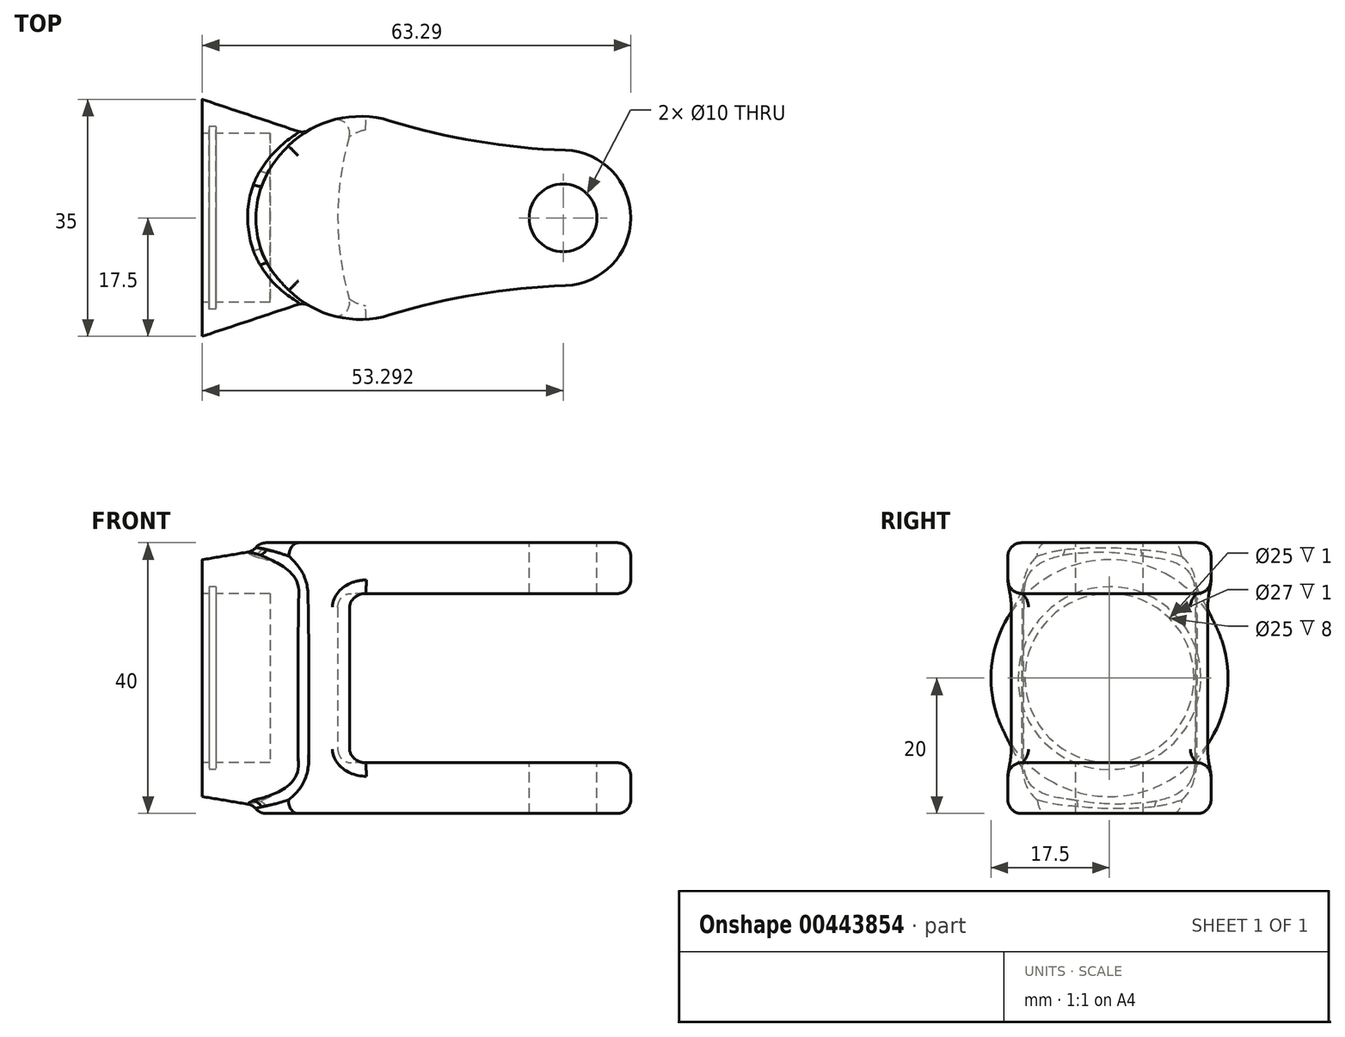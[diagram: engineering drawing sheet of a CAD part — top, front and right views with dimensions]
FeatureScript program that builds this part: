
annotation { "Feature Type Name" : "Feature", "Feature Type Description" : "" }
export const myFeature = defineFeature(function(context is Context, id is Id, definition is map)
    precondition{}
    {
        {
            var Q0;
            Q0=qCreatedBy(makeId("Right.planeOp"),FACE);
            var sketch = newSketch(context, id + "F0", { "sketchPlane" : qUnion([Q0])});
            skCircle(sketch, "E0", {"center": v(0, 0) * mm, "radius": 17.5 * mm});
            skSolve(sketch);
        }
        {
            var Q0;
            Q0=qCreatedBy(makeId("Right.planeOp"),FACE);
            cPlane(context, id + "F1", {"entities" : qUnion([Q0]), "cplaneType" : CPlaneType.OFFSET, "offset" : 15 * mm, "width" : 150 * mm, "height" : 150 * mm});
        }
        {
            var Q0;
            Q0=qCreatedBy(id+"F1.planeOp",FACE);
            var sketch = newSketch(context, id + "F2", { "sketchPlane" : qUnion([Q0])});
            skLineSegment(sketch, "E1.bottom", {"start": v(5, -20) * mm, "end": v(-5, -20) * mm});
            skLineSegment(sketch, "E1.top", {"start": v(5, 20) * mm, "end": v(-5, 20) * mm});
            skLineSegment(sketch, "E1.left", {"start": v(12.5, -12.5) * mm, "end": v(12.5, 12.5) * mm});
            skLineSegment(sketch, "E1.right", {"start": v(-12.5, -12.5) * mm, "end": v(-12.5, 12.5) * mm});
            skPoint(sketch, "E1.middle", {"position": v(0, 0) * mm});
            skPoint(sketch, "E2.visualSharp", {"position": v(-12.5, 20) * mm});
            skArc(sketch, "E2.filletArc", {"start": v(-5, 20) * mm, "mid": v(-10.3, 17.8) * mm, "end": v(-12.5, 12.5) * mm});
            skPoint(sketch, "E3.visualSharp", {"position": v(12.5, 20) * mm});
            skArc(sketch, "E3.filletArc", {"start": v(12.5, 12.5) * mm, "mid": v(10.3, 17.8) * mm, "end": v(5, 20) * mm});
            skPoint(sketch, "E4.visualSharp", {"position": v(12.5, -20) * mm});
            skArc(sketch, "E4.filletArc", {"start": v(5, -20) * mm, "mid": v(10.3, -17.8) * mm, "end": v(12.5, -12.5) * mm});
            skPoint(sketch, "E5.visualSharp", {"position": v(-12.5, -20) * mm});
            skArc(sketch, "E5.filletArc", {"start": v(-12.5, -12.5) * mm, "mid": v(-10.3, -17.8) * mm, "end": v(-5, -20) * mm});
            skSolve(sketch);
        }
        {
            var Q0;
            Q0 = qSketchRegion(id + "F2", true);
            var Q1;
            Q1=makeQuery(id+"F0.imprint","IMPRINT",FACE,{"disambiguationData":[TD([[makeQuery(id+"F0.imprint","IMPRINT",EDGE,{"derivedFrom":sQuery(id+"F0.wireOp",EDGE,"E0")}),1.0]])]});
            loft(context, id + "F3", {"sheetProfilesArray" : [{ "sheetProfileEntities" : qUnion([Q0]) }, { "sheetProfileEntities" : qUnion([Q1]) }]});
        }
        {
            var Q0;
            Q0=qCreatedBy(makeId("Top.planeOp"),FACE);
            var sketch = newSketch(context, id + "F4", { "sketchPlane" : qUnion([Q0])});
            skCircle(sketch, "E6", {"center": v(23.3, 0) * mm, "radius": 15 * mm});
            skCircle(sketch, "E7", {"center": v(53.3, 0) * mm, "radius": 10 * mm});
            skArc(sketch, "E8", {"start": v(27.7, 14.34) * mm, "mid": v(40.52, 11.31) * mm, "end": v(53.63, 10) * mm});
            skArc(sketch, "E9", {"start": v(53.63, -10) * mm, "mid": v(40.52, -11.31) * mm, "end": v(27.7, -14.34) * mm});
            skSolve(sketch);
        }
        {
            var Q0;
            Q0 = qSketchRegion(id + "F4", true);
            extrude(context, id + "F5", {"entities" : qUnion([Q0]), "operationType" : NewBodyOperationType.ADD, "endBound" : BoundingType.SYMMETRIC, "depth" : 40 * mm});
        }
        {
            var Q0;
            Q0=qCreatedBy(makeId("Front.planeOp"),FACE);
            var sketch = newSketch(context, id + "F6", { "sketchPlane" : qUnion([Q0])});
            skLineSegment(sketch, "E10", {"start": v(63.3, -12.5) * mm, "end": v(20, -12.5) * mm});
            skLineSegment(sketch, "E11", {"start": v(20, -12.5) * mm, "end": v(20, 12.5) * mm});
            skLineSegment(sketch, "E12", {"start": v(20, 12.5) * mm, "end": v(63.3, 12.5) * mm});
            skLineSegment(sketch, "E13", {"start": v(63.3, 12.5) * mm, "end": v(63.3, -12.5) * mm});
            skSolve(sketch);
        }
        {
            var Q0;
            Q0 = qSketchRegion(id + "F6", true);
            var Q1;
            Q1=sQuery(id+"F6.wireOp",EDGE,"E13");
            revolve(context, id + "F7", {"operationType" : NewBodyOperationType.REMOVE, "entities" : qUnion([Q0]), "axis" : qUnion([Q1]), "revolveType" : RevolveType.FULL, "oppositeDirection" : true});
        }
        {
            var Q0;
            Q0=makeQuery(id+"F3.opLoft","CAP_FACE",FACE,{"disambiguationData":[OSD([makeQuery(id+"F0.imprint","IMPRINT",FACE,{"disambiguationData":[TD([[makeQuery(id+"F0.imprint","IMPRINT",EDGE,{"derivedFrom":sQuery(id+"F0.wireOp",EDGE,"E0")}),1.0]])]})])],"isStart":true});
            var sketch = newSketch(context, id + "F8", { "sketchPlane" : qUnion([Q0])});
            skCircle(sketch, "E14", {"center": v(0, 0) * mm, "radius": 12.5 * mm});
            skSolve(sketch);
        }
        {
            var Q0;
            Q0 = qSketchRegion(id + "F8", true);
            extrude(context, id + "F9", {"entities" : qUnion([Q0]), "operationType" : NewBodyOperationType.REMOVE, "oppositeDirection" : true, "depth" : 10 * mm});
        }
        {
            var Q0;
            Q0=makeQuery(id+"F3.opLoft","CAP_FACE",FACE,{"disambiguationData":[OSD([makeQuery(id+"F0.imprint","IMPRINT",FACE,{"disambiguationData":[TD([[makeQuery(id+"F0.imprint","IMPRINT",EDGE,{"derivedFrom":sQuery(id+"F0.wireOp",EDGE,"E0")}),1.0]])]})])],"isStart":true});
            cPlane(context, id + "F10", {"entities" : qUnion([Q0]), "cplaneType" : CPlaneType.OFFSET, "offset" : 1 * mm, "oppositeDirection" : true, "width" : 150 * mm, "height" : 150 * mm});
        }
        {
            var Q0;
            Q0=qCreatedBy(id+"F10.planeOp",FACE);
            var sketch = newSketch(context, id + "F11", { "sketchPlane" : qUnion([Q0])});
            skCircle(sketch, "E15.0", {"center": v(0, 0) * mm, "radius": 12.5 * mm});
            skCircle(sketch, "E16.0", {"center": v(0, 0) * mm, "radius": 13.5 * mm});
            skSolve(sketch);
        }
        {
            var Q0;
            Q0 = qSketchRegion(id + "F11", true);
            extrude(context, id + "F12", {"entities" : qUnion([Q0]), "operationType" : NewBodyOperationType.REMOVE, "oppositeDirection" : true, "depth" : 1 * mm});
        }
        {
            var Q0;
            Q0=makeQuery(id+"F5.opExtrude","CAP_FACE",FACE,{"disambiguationData":[OSD([sQuery(id+"F4.wireOp",EDGE,"E6"),sQuery(id+"F4.wireOp",EDGE,"E7"),sQuery(id+"F4.wireOp",EDGE,"E8"),sQuery(id+"F4.wireOp",EDGE,"E9")])],"isStart":false});
            var sketch = newSketch(context, id + "F13", { "sketchPlane" : qUnion([Q0])});
            skCircle(sketch, "E17", {"center": v(53.3, 0) * mm, "radius": 5 * mm});
            skSolve(sketch);
        }
        {
            var Q0;
            Q0=makeQuery(id+"F13.imprint","IMPRINT",FACE,{"disambiguationData":[TD([[makeQuery(id+"F13.imprint","IMPRINT",EDGE,{"derivedFrom":sQuery(id+"F13.wireOp",EDGE,"E17")}),1.0]])]});
            var Q1;
            Q1=sQuery(id+"F13.wireOp",EDGE,"E17");
            extrude(context, id + "F14", {"entities" : qUnion([Q0]), "operationType" : NewBodyOperationType.REMOVE, "surfaceEntities" : qUnion([Q1]), "endBound" : BoundingType.THROUGH_ALL, "oppositeDirection" : true, "depth" : 25 * mm});
        }
        {
            var Q0;
            Q0=makeQuery(id+"F7.boolean.opBoolean","COPY",EDGE,{"derivedFrom":makeQuery(id+"F7.opRevolve","SWEPT_EDGE",EDGE,{"disambiguationData":[OSD([sQuery(id+"F6.wireOp",EDGE,"E11"),sQuery(id+"F6.wireOp",EDGE,"E12")])]})});
            var Q1;
            Q1=makeQuery(id+"F7.boolean.opBoolean","COPY",EDGE,{"derivedFrom":makeQuery(id+"F7.opRevolve","SWEPT_EDGE",EDGE,{"disambiguationData":[OSD([sQuery(id+"F6.wireOp",EDGE,"E10"),sQuery(id+"F6.wireOp",EDGE,"E11")])]})});
            fillet(context, id + "F15", {"entities" : qUnion([Q0, Q1]), "radius" : 2 * mm, "tangentPropagation" : true, "allowEdgeOverflow" : false});
        }
        {
            var Q0;
            Q0=makeQuery(id+"F5.boolean.opBoolean","INTERSECT",EDGE,{"disambiguationData":[OD(0.0)],"derivedFrom":[makeQuery(id+"F3.opLoft","SWEPT_FACE",FACE,{"disambiguationData":[OSD([sQuery(id+"F0.wireOp",EDGE,"E0"),sQuery(id+"F2.wireOp",EDGE,"E1.bottom"),sQuery(id+"F2.wireOp",EDGE,"E4.filletArc"),sQuery(id+"F2.wireOp",EDGE,"E5.filletArc")])]}),makeQuery(id+"F5.opExtrude","SWEPT_FACE",FACE,{"disambiguationData":[OSD([sQuery(id+"F4.wireOp",EDGE,"E6")])]})]});
            var Q1;
            Q1=makeQuery(id+"F5.boolean.opBoolean","INTERSECT",EDGE,{"disambiguationData":[OD(1.0)],"derivedFrom":[makeQuery(id+"F3.opLoft","SWEPT_FACE",FACE,{"disambiguationData":[OSD([sQuery(id+"F0.wireOp",EDGE,"E0"),sQuery(id+"F2.wireOp",EDGE,"E1.bottom"),sQuery(id+"F2.wireOp",EDGE,"E4.filletArc"),sQuery(id+"F2.wireOp",EDGE,"E5.filletArc")])]}),makeQuery(id+"F5.opExtrude","SWEPT_FACE",FACE,{"disambiguationData":[OSD([sQuery(id+"F4.wireOp",EDGE,"E6")])]})]});
            fillet(context, id + "F16", {"entities" : qUnion([Q0, Q1]), "radius" : 2 * mm, "tangentPropagation" : true, "allowEdgeOverflow" : false});
        }
        {
            var Q0;
            Q0=makeQuery(id+"F5.opExtrude","CAP_EDGE",EDGE,{"disambiguationData":[OSD([sQuery(id+"F4.wireOp",EDGE,"E6")])],"isStart":true});
            var Q1;
            Q1=makeQuery(id+"F5.opExtrude","CAP_EDGE",EDGE,{"disambiguationData":[OSD([sQuery(id+"F4.wireOp",EDGE,"E6")])],"isStart":true});
            var Q2;
            Q2=makeQuery(id+"F5.opExtrude","CAP_EDGE",EDGE,{"disambiguationData":[OSD([sQuery(id+"F4.wireOp",EDGE,"E6")])],"isStart":true});
            var Q3;
            Q3=makeQuery(id+"F5.opExtrude","CAP_EDGE",EDGE,{"disambiguationData":[OSD([sQuery(id+"F4.wireOp",EDGE,"E6")])],"isStart":true});
            var Q4;
            Q4=makeQuery(id+"F5.opExtrude","CAP_EDGE",EDGE,{"disambiguationData":[OSD([sQuery(id+"F4.wireOp",EDGE,"E6")])],"isStart":true});
            var Q5;
            Q5=makeQuery(id+"F5.opExtrude","CAP_EDGE",EDGE,{"disambiguationData":[OSD([sQuery(id+"F4.wireOp",EDGE,"E6")])],"isStart":true});
            var Q6;
            Q6=makeQuery(id+"F5.opExtrude","CAP_EDGE",EDGE,{"disambiguationData":[OSD([sQuery(id+"F4.wireOp",EDGE,"E6")])],"isStart":true});
            var Q7;
            Q7=makeQuery(id+"F5.opExtrude","CAP_EDGE",EDGE,{"disambiguationData":[OSD([sQuery(id+"F4.wireOp",EDGE,"E6")])],"isStart":true});
            var Q8;
            Q8=makeQuery(id+"F5.opExtrude","CAP_EDGE",EDGE,{"disambiguationData":[OSD([sQuery(id+"F4.wireOp",EDGE,"E6")])],"isStart":true});
            var Q9;
            Q9=makeQuery(id+"F5.opExtrude","CAP_EDGE",EDGE,{"disambiguationData":[OSD([sQuery(id+"F4.wireOp",EDGE,"E6")])],"isStart":true});
            var Q10;
            Q10=makeQuery(id+"F5.opExtrude","CAP_EDGE",EDGE,{"disambiguationData":[OSD([sQuery(id+"F4.wireOp",EDGE,"E6")])],"isStart":true});
            var Q11;
            Q11=makeQuery(id+"F5.opExtrude","CAP_EDGE",EDGE,{"disambiguationData":[OSD([sQuery(id+"F4.wireOp",EDGE,"E6")])],"isStart":true});
            var Q12;
            Q12=makeQuery(id+"F5.opExtrude","CAP_EDGE",EDGE,{"disambiguationData":[OSD([sQuery(id+"F4.wireOp",EDGE,"E6")])],"isStart":true});
            var Q13;
            Q13=makeQuery(id+"F5.opExtrude","CAP_EDGE",EDGE,{"disambiguationData":[OSD([sQuery(id+"F4.wireOp",EDGE,"E6")])],"isStart":true});
            var Q14;
            Q14=makeQuery(id+"F5.opExtrude","CAP_EDGE",EDGE,{"disambiguationData":[OSD([sQuery(id+"F4.wireOp",EDGE,"E6")])],"isStart":true});
            var Q15;
            Q15=makeQuery(id+"F5.opExtrude","CAP_EDGE",EDGE,{"disambiguationData":[OSD([sQuery(id+"F4.wireOp",EDGE,"E6")])],"isStart":true});
            var Q16;
            Q16=makeQuery(id+"F5.opExtrude","CAP_EDGE",EDGE,{"disambiguationData":[OSD([sQuery(id+"F4.wireOp",EDGE,"E6")])],"isStart":true});
            var Q17;
            Q17=makeQuery(id+"F5.opExtrude","CAP_EDGE",EDGE,{"disambiguationData":[OSD([sQuery(id+"F4.wireOp",EDGE,"E6")])],"isStart":true});
            var Q18;
            Q18=makeQuery(id+"F5.opExtrude","CAP_EDGE",EDGE,{"disambiguationData":[OSD([sQuery(id+"F4.wireOp",EDGE,"E6")])],"isStart":true});
            var Q19;
            Q19=makeQuery(id+"F5.opExtrude","CAP_EDGE",EDGE,{"disambiguationData":[OSD([sQuery(id+"F4.wireOp",EDGE,"E6")])],"isStart":true});
            var Q20;
            Q20=makeQuery(id+"F5.opExtrude","CAP_EDGE",EDGE,{"disambiguationData":[OSD([sQuery(id+"F4.wireOp",EDGE,"E6")])],"isStart":true});
            var Q21;
            Q21=makeQuery(id+"F5.opExtrude","CAP_EDGE",EDGE,{"disambiguationData":[OSD([sQuery(id+"F4.wireOp",EDGE,"E6")])],"isStart":true});
            var Q22;
            Q22=makeQuery(id+"F5.opExtrude","CAP_EDGE",EDGE,{"disambiguationData":[OSD([sQuery(id+"F4.wireOp",EDGE,"E6")])],"isStart":true});
            var Q23;
            Q23=makeQuery(id+"F5.opExtrude","CAP_EDGE",EDGE,{"disambiguationData":[OSD([sQuery(id+"F4.wireOp",EDGE,"E6")])],"isStart":true});
            var Q24;
            Q24=makeQuery(id+"F5.opExtrude","CAP_EDGE",EDGE,{"disambiguationData":[OSD([sQuery(id+"F4.wireOp",EDGE,"E6")])],"isStart":true});
            var Q25;
            Q25=makeQuery(id+"F5.opExtrude","CAP_EDGE",EDGE,{"disambiguationData":[OSD([sQuery(id+"F4.wireOp",EDGE,"E6")])],"isStart":true});
            var Q26;
            Q26=makeQuery(id+"F5.opExtrude","CAP_EDGE",EDGE,{"disambiguationData":[OSD([sQuery(id+"F4.wireOp",EDGE,"E6")])],"isStart":true});
            var Q27;
            Q27=makeQuery(id+"F5.opExtrude","CAP_EDGE",EDGE,{"disambiguationData":[OSD([sQuery(id+"F4.wireOp",EDGE,"E6")])],"isStart":true});
            var Q28;
            Q28=makeQuery(id+"F5.opExtrude","CAP_EDGE",EDGE,{"disambiguationData":[OSD([sQuery(id+"F4.wireOp",EDGE,"E6")])],"isStart":true});
            var Q29;
            Q29=makeQuery(id+"F5.opExtrude","CAP_EDGE",EDGE,{"disambiguationData":[OSD([sQuery(id+"F4.wireOp",EDGE,"E6")])],"isStart":true});
            var Q30;
            Q30=makeQuery(id+"F5.opExtrude","CAP_EDGE",EDGE,{"disambiguationData":[OSD([sQuery(id+"F4.wireOp",EDGE,"E6")])],"isStart":true});
            var Q31;
            Q31=makeQuery(id+"F5.opExtrude","CAP_EDGE",EDGE,{"disambiguationData":[OSD([sQuery(id+"F4.wireOp",EDGE,"E6")])],"isStart":true});
            var Q32;
            Q32=makeQuery(id+"F5.opExtrude","CAP_EDGE",EDGE,{"disambiguationData":[OSD([sQuery(id+"F4.wireOp",EDGE,"E6")])],"isStart":true});
            var Q33;
            Q33=makeQuery(id+"F5.opExtrude","CAP_EDGE",EDGE,{"disambiguationData":[OSD([sQuery(id+"F4.wireOp",EDGE,"E6")])],"isStart":true});
            var Q34;
            Q34=makeQuery(id+"F5.opExtrude","CAP_EDGE",EDGE,{"disambiguationData":[OSD([sQuery(id+"F4.wireOp",EDGE,"E6")])],"isStart":true});
            var Q35;
            Q35=makeQuery(id+"F5.opExtrude","CAP_EDGE",EDGE,{"disambiguationData":[OSD([sQuery(id+"F4.wireOp",EDGE,"E6")])],"isStart":true});
            var Q36;
            Q36=makeQuery(id+"F5.opExtrude","CAP_EDGE",EDGE,{"disambiguationData":[OSD([sQuery(id+"F4.wireOp",EDGE,"E6")])],"isStart":true});
            var Q37;
            Q37=makeQuery(id+"F5.opExtrude","CAP_EDGE",EDGE,{"disambiguationData":[OSD([sQuery(id+"F4.wireOp",EDGE,"E6")])],"isStart":true});
            var Q38;
            Q38=makeQuery(id+"F5.opExtrude","CAP_EDGE",EDGE,{"disambiguationData":[OSD([sQuery(id+"F4.wireOp",EDGE,"E6")])],"isStart":true});
            var Q39;
            Q39=makeQuery(id+"F5.opExtrude","CAP_EDGE",EDGE,{"disambiguationData":[OSD([sQuery(id+"F4.wireOp",EDGE,"E6")])],"isStart":true});
            var Q40;
            Q40=makeQuery(id+"F5.opExtrude","CAP_EDGE",EDGE,{"disambiguationData":[OSD([sQuery(id+"F4.wireOp",EDGE,"E6")])],"isStart":true});
            var Q41;
            Q41=makeQuery(id+"F5.opExtrude","CAP_EDGE",EDGE,{"disambiguationData":[OSD([sQuery(id+"F4.wireOp",EDGE,"E6")])],"isStart":true});
            var Q42;
            Q42=makeQuery(id+"F5.opExtrude","CAP_EDGE",EDGE,{"disambiguationData":[OSD([sQuery(id+"F4.wireOp",EDGE,"E6")])],"isStart":true});
            var Q43;
            Q43=makeQuery(id+"F5.opExtrude","CAP_EDGE",EDGE,{"disambiguationData":[OSD([sQuery(id+"F4.wireOp",EDGE,"E6")])],"isStart":true});
            var Q44;
            Q44=makeQuery(id+"F5.opExtrude","CAP_EDGE",EDGE,{"disambiguationData":[OSD([sQuery(id+"F4.wireOp",EDGE,"E6")])],"isStart":true});
            var Q45;
            Q45=makeQuery(id+"F5.opExtrude","CAP_EDGE",EDGE,{"disambiguationData":[OSD([sQuery(id+"F4.wireOp",EDGE,"E6")])],"isStart":true});
            var Q46;
            Q46=makeQuery(id+"F5.opExtrude","CAP_EDGE",EDGE,{"disambiguationData":[OSD([sQuery(id+"F4.wireOp",EDGE,"E6")])],"isStart":true});
            var Q47;
            Q47=makeQuery(id+"F5.opExtrude","CAP_EDGE",EDGE,{"disambiguationData":[OSD([sQuery(id+"F4.wireOp",EDGE,"E6")])],"isStart":true});
            var Q48;
            Q48=makeQuery(id+"F5.opExtrude","CAP_EDGE",EDGE,{"disambiguationData":[OSD([sQuery(id+"F4.wireOp",EDGE,"E6")])],"isStart":true});
            var Q49;
            Q49=makeQuery(id+"F5.opExtrude","CAP_EDGE",EDGE,{"disambiguationData":[OSD([sQuery(id+"F4.wireOp",EDGE,"E6")])],"isStart":true});
            var Q50;
            Q50=makeQuery(id+"F5.opExtrude","CAP_EDGE",EDGE,{"disambiguationData":[OSD([sQuery(id+"F4.wireOp",EDGE,"E6")])],"isStart":true});
            var Q51;
            Q51=makeQuery(id+"F5.opExtrude","CAP_EDGE",EDGE,{"disambiguationData":[OSD([sQuery(id+"F4.wireOp",EDGE,"E6")])],"isStart":true});
            var Q52;
            Q52=makeQuery(id+"F5.opExtrude","CAP_EDGE",EDGE,{"disambiguationData":[OSD([sQuery(id+"F4.wireOp",EDGE,"E6")])],"isStart":true});
            var Q53;
            Q53=makeQuery(id+"F5.opExtrude","CAP_EDGE",EDGE,{"disambiguationData":[OSD([sQuery(id+"F4.wireOp",EDGE,"E6")])],"isStart":true});
            var Q54;
            Q54=makeQuery(id+"F5.opExtrude","CAP_EDGE",EDGE,{"disambiguationData":[OSD([sQuery(id+"F4.wireOp",EDGE,"E6")])],"isStart":true});
            var Q55;
            Q55=makeQuery(id+"F5.opExtrude","CAP_EDGE",EDGE,{"disambiguationData":[OSD([sQuery(id+"F4.wireOp",EDGE,"E6")])],"isStart":true});
            var Q56;
            Q56=makeQuery(id+"F5.opExtrude","CAP_EDGE",EDGE,{"disambiguationData":[OSD([sQuery(id+"F4.wireOp",EDGE,"E6")])],"isStart":true});
            var Q57;
            Q57=makeQuery(id+"F5.opExtrude","CAP_EDGE",EDGE,{"disambiguationData":[OSD([sQuery(id+"F4.wireOp",EDGE,"E6")])],"isStart":true});
            var Q58;
            Q58=makeQuery(id+"F5.opExtrude","CAP_EDGE",EDGE,{"disambiguationData":[OSD([sQuery(id+"F4.wireOp",EDGE,"E6")])],"isStart":true});
            var Q59;
            Q59=makeQuery(id+"F5.opExtrude","CAP_EDGE",EDGE,{"disambiguationData":[OSD([sQuery(id+"F4.wireOp",EDGE,"E6")])],"isStart":true});
            var Q60;
            Q60=makeQuery(id+"F5.opExtrude","CAP_EDGE",EDGE,{"disambiguationData":[OSD([sQuery(id+"F4.wireOp",EDGE,"E6")])],"isStart":true});
            var Q61;
            Q61=makeQuery(id+"F5.opExtrude","CAP_EDGE",EDGE,{"disambiguationData":[OSD([sQuery(id+"F4.wireOp",EDGE,"E6")])],"isStart":true});
            var Q62;
            Q62=makeQuery(id+"F5.opExtrude","CAP_EDGE",EDGE,{"disambiguationData":[OSD([sQuery(id+"F4.wireOp",EDGE,"E6")])],"isStart":true});
            var Q63;
            Q63=makeQuery(id+"F5.opExtrude","CAP_EDGE",EDGE,{"disambiguationData":[OSD([sQuery(id+"F4.wireOp",EDGE,"E6")])],"isStart":true});
            var Q64;
            Q64=makeQuery(id+"F5.opExtrude","CAP_EDGE",EDGE,{"disambiguationData":[OSD([sQuery(id+"F4.wireOp",EDGE,"E6")])],"isStart":true});
            var Q65;
            Q65=makeQuery(id+"F5.opExtrude","CAP_EDGE",EDGE,{"disambiguationData":[OSD([sQuery(id+"F4.wireOp",EDGE,"E6")])],"isStart":true});
            var Q66;
            Q66=makeQuery(id+"F5.opExtrude","CAP_EDGE",EDGE,{"disambiguationData":[OSD([sQuery(id+"F4.wireOp",EDGE,"E6")])],"isStart":true});
            var Q67;
            Q67=makeQuery(id+"F5.opExtrude","CAP_EDGE",EDGE,{"disambiguationData":[OSD([sQuery(id+"F4.wireOp",EDGE,"E6")])],"isStart":true});
            var Q68;
            Q68=makeQuery(id+"F5.opExtrude","CAP_EDGE",EDGE,{"disambiguationData":[OSD([sQuery(id+"F4.wireOp",EDGE,"E6")])],"isStart":true});
            var Q69;
            Q69=makeQuery(id+"F5.opExtrude","CAP_EDGE",EDGE,{"disambiguationData":[OSD([sQuery(id+"F4.wireOp",EDGE,"E6")])],"isStart":true});
            var Q70;
            Q70=makeQuery(id+"F5.opExtrude","CAP_EDGE",EDGE,{"disambiguationData":[OSD([sQuery(id+"F4.wireOp",EDGE,"E6")])],"isStart":true});
            var Q71;
            Q71=makeQuery(id+"F5.opExtrude","CAP_EDGE",EDGE,{"disambiguationData":[OSD([sQuery(id+"F4.wireOp",EDGE,"E6")])],"isStart":true});
            var Q72;
            Q72=makeQuery(id+"F5.opExtrude","CAP_EDGE",EDGE,{"disambiguationData":[OSD([sQuery(id+"F4.wireOp",EDGE,"E6")])],"isStart":true});
            var Q73;
            Q73=makeQuery(id+"F5.opExtrude","CAP_EDGE",EDGE,{"disambiguationData":[OSD([sQuery(id+"F4.wireOp",EDGE,"E6")])],"isStart":true});
            var Q74;
            Q74=makeQuery(id+"F5.opExtrude","CAP_EDGE",EDGE,{"disambiguationData":[OSD([sQuery(id+"F4.wireOp",EDGE,"E6")])],"isStart":true});
            var Q75;
            Q75=makeQuery(id+"F5.opExtrude","CAP_EDGE",EDGE,{"disambiguationData":[OSD([sQuery(id+"F4.wireOp",EDGE,"E6")])],"isStart":true});
            var Q76;
            Q76=makeQuery(id+"F5.opExtrude","CAP_EDGE",EDGE,{"disambiguationData":[OSD([sQuery(id+"F4.wireOp",EDGE,"E6")])],"isStart":true});
            var Q77;
            Q77=makeQuery(id+"F5.opExtrude","CAP_EDGE",EDGE,{"disambiguationData":[OSD([sQuery(id+"F4.wireOp",EDGE,"E6")])],"isStart":true});
            var Q78;
            Q78=makeQuery(id+"F5.opExtrude","CAP_EDGE",EDGE,{"disambiguationData":[OSD([sQuery(id+"F4.wireOp",EDGE,"E6")])],"isStart":true});
            var Q79;
            Q79=makeQuery(id+"F5.opExtrude","CAP_EDGE",EDGE,{"disambiguationData":[OSD([sQuery(id+"F4.wireOp",EDGE,"E6")])],"isStart":true});
            var Q80;
            Q80=makeQuery(id+"F5.opExtrude","CAP_EDGE",EDGE,{"disambiguationData":[OSD([sQuery(id+"F4.wireOp",EDGE,"E6")])],"isStart":true});
            var Q81;
            Q81=makeQuery(id+"F5.opExtrude","CAP_EDGE",EDGE,{"disambiguationData":[OSD([sQuery(id+"F4.wireOp",EDGE,"E6")])],"isStart":true});
            var Q82;
            Q82=makeQuery(id+"F5.opExtrude","CAP_EDGE",EDGE,{"disambiguationData":[OSD([sQuery(id+"F4.wireOp",EDGE,"E6")])],"isStart":true});
            var Q83;
            Q83=makeQuery(id+"F5.opExtrude","CAP_EDGE",EDGE,{"disambiguationData":[OSD([sQuery(id+"F4.wireOp",EDGE,"E6")])],"isStart":true});
            var Q84;
            Q84=makeQuery(id+"F5.opExtrude","CAP_EDGE",EDGE,{"disambiguationData":[OSD([sQuery(id+"F4.wireOp",EDGE,"E6")])],"isStart":true});
            var Q85;
            Q85=makeQuery(id+"F5.opExtrude","CAP_EDGE",EDGE,{"disambiguationData":[OSD([sQuery(id+"F4.wireOp",EDGE,"E6")])],"isStart":true});
            var Q86;
            Q86=makeQuery(id+"F5.opExtrude","CAP_EDGE",EDGE,{"disambiguationData":[OSD([sQuery(id+"F4.wireOp",EDGE,"E6")])],"isStart":true});
            var Q87;
            Q87=makeQuery(id+"F5.opExtrude","CAP_EDGE",EDGE,{"disambiguationData":[OSD([sQuery(id+"F4.wireOp",EDGE,"E6")])],"isStart":true});
            var Q88;
            Q88=makeQuery(id+"F5.opExtrude","CAP_EDGE",EDGE,{"disambiguationData":[OSD([sQuery(id+"F4.wireOp",EDGE,"E6")])],"isStart":true});
            var Q89;
            Q89=makeQuery(id+"F5.opExtrude","CAP_EDGE",EDGE,{"disambiguationData":[OSD([sQuery(id+"F4.wireOp",EDGE,"E6")])],"isStart":true});
            var Q90;
            Q90=makeQuery(id+"F5.opExtrude","CAP_EDGE",EDGE,{"disambiguationData":[OSD([sQuery(id+"F4.wireOp",EDGE,"E6")])],"isStart":true});
            var Q91;
            Q91=makeQuery(id+"F5.opExtrude","CAP_EDGE",EDGE,{"disambiguationData":[OSD([sQuery(id+"F4.wireOp",EDGE,"E6")])],"isStart":true});
            var Q92;
            Q92=makeQuery(id+"F5.opExtrude","CAP_EDGE",EDGE,{"disambiguationData":[OSD([sQuery(id+"F4.wireOp",EDGE,"E6")])],"isStart":true});
            var Q93;
            Q93=makeQuery(id+"F5.opExtrude","CAP_EDGE",EDGE,{"disambiguationData":[OSD([sQuery(id+"F4.wireOp",EDGE,"E6")])],"isStart":true});
            var Q94;
            Q94=makeQuery(id+"F5.opExtrude","CAP_EDGE",EDGE,{"disambiguationData":[OSD([sQuery(id+"F4.wireOp",EDGE,"E6")])],"isStart":true});
            var Q95;
            Q95=makeQuery(id+"F5.opExtrude","CAP_EDGE",EDGE,{"disambiguationData":[OSD([sQuery(id+"F4.wireOp",EDGE,"E6")])],"isStart":true});
            var Q96;
            Q96=makeQuery(id+"F5.opExtrude","CAP_EDGE",EDGE,{"disambiguationData":[OSD([sQuery(id+"F4.wireOp",EDGE,"E6")])],"isStart":true});
            var Q97;
            Q97=makeQuery(id+"F5.opExtrude","CAP_EDGE",EDGE,{"disambiguationData":[OSD([sQuery(id+"F4.wireOp",EDGE,"E6")])],"isStart":true});
            var Q98;
            Q98=makeQuery(id+"F5.opExtrude","CAP_EDGE",EDGE,{"disambiguationData":[OSD([sQuery(id+"F4.wireOp",EDGE,"E6")])],"isStart":true});
            var Q99;
            Q99=makeQuery(id+"F5.opExtrude","CAP_EDGE",EDGE,{"disambiguationData":[OSD([sQuery(id+"F4.wireOp",EDGE,"E6")])],"isStart":true});
            var Q100;
            Q100=makeQuery(id+"F5.opExtrude","CAP_EDGE",EDGE,{"disambiguationData":[OSD([sQuery(id+"F4.wireOp",EDGE,"E6")])],"isStart":true});
            var Q101;
            Q101=makeQuery(id+"F5.opExtrude","CAP_EDGE",EDGE,{"disambiguationData":[OSD([sQuery(id+"F4.wireOp",EDGE,"E6")])],"isStart":true});
            var Q102;
            Q102=makeQuery(id+"F5.opExtrude","CAP_EDGE",EDGE,{"disambiguationData":[OSD([sQuery(id+"F4.wireOp",EDGE,"E6")])],"isStart":true});
            var Q103;
            Q103=makeQuery(id+"F5.opExtrude","CAP_EDGE",EDGE,{"disambiguationData":[OSD([sQuery(id+"F4.wireOp",EDGE,"E6")])],"isStart":true});
            var Q104;
            Q104=makeQuery(id+"F5.opExtrude","CAP_EDGE",EDGE,{"disambiguationData":[OSD([sQuery(id+"F4.wireOp",EDGE,"E6")])],"isStart":true});
            var Q105;
            Q105=makeQuery(id+"F5.opExtrude","CAP_EDGE",EDGE,{"disambiguationData":[OSD([sQuery(id+"F4.wireOp",EDGE,"E6")])],"isStart":true});
            var Q106;
            Q106=makeQuery(id+"F5.opExtrude","CAP_EDGE",EDGE,{"disambiguationData":[OSD([sQuery(id+"F4.wireOp",EDGE,"E6")])],"isStart":true});
            var Q107;
            Q107=makeQuery(id+"F5.opExtrude","CAP_EDGE",EDGE,{"disambiguationData":[OSD([sQuery(id+"F4.wireOp",EDGE,"E6")])],"isStart":true});
            var Q108;
            Q108=makeQuery(id+"F5.opExtrude","CAP_EDGE",EDGE,{"disambiguationData":[OSD([sQuery(id+"F4.wireOp",EDGE,"E6")])],"isStart":true});
            var Q109;
            Q109=makeQuery(id+"F5.opExtrude","CAP_EDGE",EDGE,{"disambiguationData":[OSD([sQuery(id+"F4.wireOp",EDGE,"E6")])],"isStart":true});
            var Q110;
            Q110=makeQuery(id+"F5.opExtrude","CAP_EDGE",EDGE,{"disambiguationData":[OSD([sQuery(id+"F4.wireOp",EDGE,"E6")])],"isStart":true});
            var Q111;
            Q111=makeQuery(id+"F5.opExtrude","CAP_EDGE",EDGE,{"disambiguationData":[OSD([sQuery(id+"F4.wireOp",EDGE,"E6")])],"isStart":true});
            var Q112;
            Q112=makeQuery(id+"F5.opExtrude","CAP_EDGE",EDGE,{"disambiguationData":[OSD([sQuery(id+"F4.wireOp",EDGE,"E6")])],"isStart":true});
            var Q113;
            Q113=makeQuery(id+"F5.opExtrude","CAP_EDGE",EDGE,{"disambiguationData":[OSD([sQuery(id+"F4.wireOp",EDGE,"E6")])],"isStart":true});
            var Q114;
            Q114=makeQuery(id+"F5.opExtrude","CAP_EDGE",EDGE,{"disambiguationData":[OSD([sQuery(id+"F4.wireOp",EDGE,"E6")])],"isStart":true});
            var Q115;
            Q115=makeQuery(id+"F5.opExtrude","CAP_EDGE",EDGE,{"disambiguationData":[OSD([sQuery(id+"F4.wireOp",EDGE,"E6")])],"isStart":true});
            var Q116;
            Q116=makeQuery(id+"F5.opExtrude","CAP_EDGE",EDGE,{"disambiguationData":[OSD([sQuery(id+"F4.wireOp",EDGE,"E6")])],"isStart":true});
            var Q117;
            Q117=makeQuery(id+"F5.opExtrude","CAP_EDGE",EDGE,{"disambiguationData":[OSD([sQuery(id+"F4.wireOp",EDGE,"E6")])],"isStart":true});
            var Q118;
            Q118=makeQuery(id+"F5.opExtrude","CAP_EDGE",EDGE,{"disambiguationData":[OSD([sQuery(id+"F4.wireOp",EDGE,"E6")])],"isStart":true});
            var Q119;
            Q119=makeQuery(id+"F5.opExtrude","CAP_EDGE",EDGE,{"disambiguationData":[OSD([sQuery(id+"F4.wireOp",EDGE,"E6")])],"isStart":true});
            var Q120;
            Q120=makeQuery(id+"F5.opExtrude","CAP_EDGE",EDGE,{"disambiguationData":[OSD([sQuery(id+"F4.wireOp",EDGE,"E6")])],"isStart":true});
            var Q121;
            Q121=makeQuery(id+"F5.opExtrude","CAP_EDGE",EDGE,{"disambiguationData":[OSD([sQuery(id+"F4.wireOp",EDGE,"E6")])],"isStart":true});
            var Q122;
            Q122=makeQuery(id+"F5.opExtrude","CAP_EDGE",EDGE,{"disambiguationData":[OSD([sQuery(id+"F4.wireOp",EDGE,"E6")])],"isStart":true});
            var Q123;
            Q123=makeQuery(id+"F5.opExtrude","CAP_EDGE",EDGE,{"disambiguationData":[OSD([sQuery(id+"F4.wireOp",EDGE,"E6")])],"isStart":true});
            var Q124;
            Q124=makeQuery(id+"F5.opExtrude","CAP_EDGE",EDGE,{"disambiguationData":[OSD([sQuery(id+"F4.wireOp",EDGE,"E6")])],"isStart":true});
            var Q125;
            Q125=makeQuery(id+"F5.opExtrude","CAP_EDGE",EDGE,{"disambiguationData":[OSD([sQuery(id+"F4.wireOp",EDGE,"E6")])],"isStart":true});
            var Q126;
            Q126=makeQuery(id+"F5.opExtrude","CAP_EDGE",EDGE,{"disambiguationData":[OSD([sQuery(id+"F4.wireOp",EDGE,"E6")])],"isStart":true});
            var Q127;
            Q127=makeQuery(id+"F5.opExtrude","CAP_EDGE",EDGE,{"disambiguationData":[OSD([sQuery(id+"F4.wireOp",EDGE,"E6")])],"isStart":true});
            var Q128;
            Q128=makeQuery(id+"F5.opExtrude","CAP_EDGE",EDGE,{"disambiguationData":[OSD([sQuery(id+"F4.wireOp",EDGE,"E6")])],"isStart":true});
            var Q129;
            Q129=makeQuery(id+"F5.opExtrude","CAP_EDGE",EDGE,{"disambiguationData":[OSD([sQuery(id+"F4.wireOp",EDGE,"E6")])],"isStart":true});
            var Q130;
            Q130=makeQuery(id+"F5.opExtrude","CAP_EDGE",EDGE,{"disambiguationData":[OSD([sQuery(id+"F4.wireOp",EDGE,"E6")])],"isStart":true});
            var Q131;
            Q131=makeQuery(id+"F5.opExtrude","CAP_EDGE",EDGE,{"disambiguationData":[OSD([sQuery(id+"F4.wireOp",EDGE,"E6")])],"isStart":true});
            var Q132;
            Q132=makeQuery(id+"F5.opExtrude","CAP_EDGE",EDGE,{"disambiguationData":[OSD([sQuery(id+"F4.wireOp",EDGE,"E6")])],"isStart":true});
            var Q133;
            Q133=makeQuery(id+"F5.opExtrude","CAP_EDGE",EDGE,{"disambiguationData":[OSD([sQuery(id+"F4.wireOp",EDGE,"E6")])],"isStart":true});
            var Q134;
            Q134=makeQuery(id+"F5.opExtrude","CAP_EDGE",EDGE,{"disambiguationData":[OSD([sQuery(id+"F4.wireOp",EDGE,"E6")])],"isStart":true});
            var Q135;
            Q135=makeQuery(id+"F5.opExtrude","CAP_EDGE",EDGE,{"disambiguationData":[OSD([sQuery(id+"F4.wireOp",EDGE,"E6")])],"isStart":true});
            var Q136;
            Q136=makeQuery(id+"F5.opExtrude","CAP_EDGE",EDGE,{"disambiguationData":[OSD([sQuery(id+"F4.wireOp",EDGE,"E6")])],"isStart":true});
            var Q137;
            Q137=makeQuery(id+"F5.opExtrude","CAP_EDGE",EDGE,{"disambiguationData":[OSD([sQuery(id+"F4.wireOp",EDGE,"E6")])],"isStart":true});
            var Q138;
            Q138=makeQuery(id+"F5.opExtrude","CAP_EDGE",EDGE,{"disambiguationData":[OSD([sQuery(id+"F4.wireOp",EDGE,"E6")])],"isStart":true});
            var Q139;
            Q139=makeQuery(id+"F5.opExtrude","CAP_EDGE",EDGE,{"disambiguationData":[OSD([sQuery(id+"F4.wireOp",EDGE,"E6")])],"isStart":true});
            var Q140;
            Q140=makeQuery(id+"F5.opExtrude","CAP_EDGE",EDGE,{"disambiguationData":[OSD([sQuery(id+"F4.wireOp",EDGE,"E6")])],"isStart":true});
            var Q141;
            Q141=makeQuery(id+"F5.opExtrude","CAP_EDGE",EDGE,{"disambiguationData":[OSD([sQuery(id+"F4.wireOp",EDGE,"E6")])],"isStart":true});
            var Q142;
            Q142=makeQuery(id+"F5.opExtrude","CAP_EDGE",EDGE,{"disambiguationData":[OSD([sQuery(id+"F4.wireOp",EDGE,"E6")])],"isStart":true});
            var Q143;
            Q143=makeQuery(id+"F5.opExtrude","CAP_EDGE",EDGE,{"disambiguationData":[OSD([sQuery(id+"F4.wireOp",EDGE,"E6")])],"isStart":true});
            var Q144;
            Q144=makeQuery(id+"F5.opExtrude","CAP_EDGE",EDGE,{"disambiguationData":[OSD([sQuery(id+"F4.wireOp",EDGE,"E6")])],"isStart":true});
            var Q145;
            Q145=makeQuery(id+"F5.opExtrude","CAP_EDGE",EDGE,{"disambiguationData":[OSD([sQuery(id+"F4.wireOp",EDGE,"E6")])],"isStart":true});
            var Q146;
            Q146=makeQuery(id+"F5.opExtrude","CAP_EDGE",EDGE,{"disambiguationData":[OSD([sQuery(id+"F4.wireOp",EDGE,"E6")])],"isStart":true});
            var Q147;
            Q147=makeQuery(id+"F5.opExtrude","CAP_EDGE",EDGE,{"disambiguationData":[OSD([sQuery(id+"F4.wireOp",EDGE,"E6")])],"isStart":true});
            var Q148;
            Q148=makeQuery(id+"F5.opExtrude","CAP_EDGE",EDGE,{"disambiguationData":[OSD([sQuery(id+"F4.wireOp",EDGE,"E6")])],"isStart":true});
            var Q149;
            Q149=makeQuery(id+"F5.opExtrude","CAP_EDGE",EDGE,{"disambiguationData":[OSD([sQuery(id+"F4.wireOp",EDGE,"E6")])],"isStart":true});
            var Q150;
            Q150=makeQuery(id+"F5.opExtrude","CAP_EDGE",EDGE,{"disambiguationData":[OSD([sQuery(id+"F4.wireOp",EDGE,"E6")])],"isStart":true});
            var Q151;
            Q151=makeQuery(id+"F5.opExtrude","CAP_EDGE",EDGE,{"disambiguationData":[OSD([sQuery(id+"F4.wireOp",EDGE,"E6")])],"isStart":true});
            var Q152;
            Q152=makeQuery(id+"F5.opExtrude","CAP_EDGE",EDGE,{"disambiguationData":[OSD([sQuery(id+"F4.wireOp",EDGE,"E6")])],"isStart":true});
            var Q153;
            Q153=makeQuery(id+"F5.opExtrude","CAP_EDGE",EDGE,{"disambiguationData":[OSD([sQuery(id+"F4.wireOp",EDGE,"E6")])],"isStart":true});
            var Q154;
            Q154=makeQuery(id+"F5.opExtrude","CAP_EDGE",EDGE,{"disambiguationData":[OSD([sQuery(id+"F4.wireOp",EDGE,"E6")])],"isStart":true});
            var Q155;
            Q155=makeQuery(id+"F5.opExtrude","CAP_EDGE",EDGE,{"disambiguationData":[OSD([sQuery(id+"F4.wireOp",EDGE,"E6")])],"isStart":true});
            var Q156;
            Q156=makeQuery(id+"F5.opExtrude","CAP_EDGE",EDGE,{"disambiguationData":[OSD([sQuery(id+"F4.wireOp",EDGE,"E6")])],"isStart":true});
            var Q157;
            Q157=makeQuery(id+"F5.opExtrude","CAP_EDGE",EDGE,{"disambiguationData":[OSD([sQuery(id+"F4.wireOp",EDGE,"E6")])],"isStart":true});
            var Q158;
            Q158=makeQuery(id+"F5.opExtrude","CAP_EDGE",EDGE,{"disambiguationData":[OSD([sQuery(id+"F4.wireOp",EDGE,"E6")])],"isStart":true});
            var Q159;
            Q159=makeQuery(id+"F5.opExtrude","CAP_EDGE",EDGE,{"disambiguationData":[OSD([sQuery(id+"F4.wireOp",EDGE,"E6")])],"isStart":true});
            var Q160;
            Q160=makeQuery(id+"F5.opExtrude","CAP_EDGE",EDGE,{"disambiguationData":[OSD([sQuery(id+"F4.wireOp",EDGE,"E6")])],"isStart":true});
            var Q161;
            Q161=makeQuery(id+"F5.opExtrude","CAP_EDGE",EDGE,{"disambiguationData":[OSD([sQuery(id+"F4.wireOp",EDGE,"E6")])],"isStart":true});
            var Q162;
            Q162=makeQuery(id+"F5.opExtrude","CAP_EDGE",EDGE,{"disambiguationData":[OSD([sQuery(id+"F4.wireOp",EDGE,"E6")])],"isStart":true});
            var Q163;
            Q163=makeQuery(id+"F5.opExtrude","CAP_EDGE",EDGE,{"disambiguationData":[OSD([sQuery(id+"F4.wireOp",EDGE,"E6")])],"isStart":true});
            var Q164;
            Q164=makeQuery(id+"F5.opExtrude","CAP_EDGE",EDGE,{"disambiguationData":[OSD([sQuery(id+"F4.wireOp",EDGE,"E6")])],"isStart":true});
            var Q165;
            Q165=makeQuery(id+"F5.opExtrude","CAP_EDGE",EDGE,{"disambiguationData":[OSD([sQuery(id+"F4.wireOp",EDGE,"E6")])],"isStart":true});
            var Q166;
            Q166=makeQuery(id+"F5.opExtrude","CAP_EDGE",EDGE,{"disambiguationData":[OSD([sQuery(id+"F4.wireOp",EDGE,"E6")])],"isStart":true});
            var Q167;
            Q167=makeQuery(id+"F5.opExtrude","CAP_EDGE",EDGE,{"disambiguationData":[OSD([sQuery(id+"F4.wireOp",EDGE,"E6")])],"isStart":true});
            var Q168;
            Q168=makeQuery(id+"F5.opExtrude","CAP_EDGE",EDGE,{"disambiguationData":[OSD([sQuery(id+"F4.wireOp",EDGE,"E6")])],"isStart":true});
            var Q169;
            Q169=makeQuery(id+"F5.opExtrude","CAP_EDGE",EDGE,{"disambiguationData":[OSD([sQuery(id+"F4.wireOp",EDGE,"E6")])],"isStart":true});
            var Q170;
            Q170=makeQuery(id+"F5.opExtrude","CAP_EDGE",EDGE,{"disambiguationData":[OSD([sQuery(id+"F4.wireOp",EDGE,"E6")])],"isStart":true});
            var Q171;
            Q171=makeQuery(id+"F5.opExtrude","CAP_EDGE",EDGE,{"disambiguationData":[OSD([sQuery(id+"F4.wireOp",EDGE,"E6")])],"isStart":true});
            var Q172;
            Q172=makeQuery(id+"F5.opExtrude","CAP_EDGE",EDGE,{"disambiguationData":[OSD([sQuery(id+"F4.wireOp",EDGE,"E6")])],"isStart":true});
            var Q173;
            Q173=makeQuery(id+"F5.opExtrude","CAP_EDGE",EDGE,{"disambiguationData":[OSD([sQuery(id+"F4.wireOp",EDGE,"E6")])],"isStart":true});
            var Q174;
            Q174=makeQuery(id+"F5.opExtrude","CAP_EDGE",EDGE,{"disambiguationData":[OSD([sQuery(id+"F4.wireOp",EDGE,"E6")])],"isStart":true});
            var Q175;
            Q175=makeQuery(id+"F5.opExtrude","CAP_EDGE",EDGE,{"disambiguationData":[OSD([sQuery(id+"F4.wireOp",EDGE,"E6")])],"isStart":true});
            var Q176;
            Q176=makeQuery(id+"F5.opExtrude","CAP_EDGE",EDGE,{"disambiguationData":[OSD([sQuery(id+"F4.wireOp",EDGE,"E6")])],"isStart":true});
            var Q177;
            Q177=makeQuery(id+"F5.opExtrude","CAP_EDGE",EDGE,{"disambiguationData":[OSD([sQuery(id+"F4.wireOp",EDGE,"E6")])],"isStart":true});
            var Q178;
            Q178=makeQuery(id+"F5.opExtrude","CAP_EDGE",EDGE,{"disambiguationData":[OSD([sQuery(id+"F4.wireOp",EDGE,"E6")])],"isStart":true});
            var Q179;
            Q179=makeQuery(id+"F5.opExtrude","CAP_EDGE",EDGE,{"disambiguationData":[OSD([sQuery(id+"F4.wireOp",EDGE,"E6")])],"isStart":true});
            var Q180;
            Q180=makeQuery(id+"F5.opExtrude","CAP_EDGE",EDGE,{"disambiguationData":[OSD([sQuery(id+"F4.wireOp",EDGE,"E6")])],"isStart":true});
            var Q181;
            Q181=makeQuery(id+"F5.opExtrude","CAP_EDGE",EDGE,{"disambiguationData":[OSD([sQuery(id+"F4.wireOp",EDGE,"E6")])],"isStart":true});
            var Q182;
            Q182=makeQuery(id+"F5.opExtrude","CAP_EDGE",EDGE,{"disambiguationData":[OSD([sQuery(id+"F4.wireOp",EDGE,"E6")])],"isStart":true});
            var Q183;
            Q183=makeQuery(id+"F5.opExtrude","CAP_EDGE",EDGE,{"disambiguationData":[OSD([sQuery(id+"F4.wireOp",EDGE,"E6")])],"isStart":true});
            var Q184;
            Q184=makeQuery(id+"F5.opExtrude","CAP_EDGE",EDGE,{"disambiguationData":[OSD([sQuery(id+"F4.wireOp",EDGE,"E6")])],"isStart":true});
            var Q185;
            Q185=makeQuery(id+"F5.opExtrude","CAP_EDGE",EDGE,{"disambiguationData":[OSD([sQuery(id+"F4.wireOp",EDGE,"E6")])],"isStart":true});
            var Q186;
            Q186=makeQuery(id+"F5.opExtrude","CAP_EDGE",EDGE,{"disambiguationData":[OSD([sQuery(id+"F4.wireOp",EDGE,"E6")])],"isStart":true});
            var Q187;
            Q187=makeQuery(id+"F5.opExtrude","CAP_EDGE",EDGE,{"disambiguationData":[OSD([sQuery(id+"F4.wireOp",EDGE,"E6")])],"isStart":true});
            var Q188;
            Q188=makeQuery(id+"F5.opExtrude","CAP_EDGE",EDGE,{"disambiguationData":[OSD([sQuery(id+"F4.wireOp",EDGE,"E6")])],"isStart":true});
            var Q189;
            Q189=makeQuery(id+"F5.opExtrude","CAP_EDGE",EDGE,{"disambiguationData":[OSD([sQuery(id+"F4.wireOp",EDGE,"E6")])],"isStart":true});
            var Q190;
            Q190=makeQuery(id+"F5.opExtrude","CAP_EDGE",EDGE,{"disambiguationData":[OSD([sQuery(id+"F4.wireOp",EDGE,"E6")])],"isStart":true});
            var Q191;
            Q191=makeQuery(id+"F5.opExtrude","CAP_EDGE",EDGE,{"disambiguationData":[OSD([sQuery(id+"F4.wireOp",EDGE,"E6")])],"isStart":true});
            var Q192;
            Q192=makeQuery(id+"F5.opExtrude","CAP_EDGE",EDGE,{"disambiguationData":[OSD([sQuery(id+"F4.wireOp",EDGE,"E6")])],"isStart":true});
            var Q193;
            Q193=makeQuery(id+"F5.opExtrude","CAP_EDGE",EDGE,{"disambiguationData":[OSD([sQuery(id+"F4.wireOp",EDGE,"E6")])],"isStart":true});
            var Q194;
            Q194=makeQuery(id+"F5.opExtrude","CAP_EDGE",EDGE,{"disambiguationData":[OSD([sQuery(id+"F4.wireOp",EDGE,"E6")])],"isStart":true});
            var Q195;
            Q195=makeQuery(id+"F5.opExtrude","CAP_EDGE",EDGE,{"disambiguationData":[OSD([sQuery(id+"F4.wireOp",EDGE,"E6")])],"isStart":true});
            var Q196;
            Q196=makeQuery(id+"F5.opExtrude","CAP_EDGE",EDGE,{"disambiguationData":[OSD([sQuery(id+"F4.wireOp",EDGE,"E6")])],"isStart":true});
            var Q197;
            Q197=makeQuery(id+"F5.opExtrude","CAP_EDGE",EDGE,{"disambiguationData":[OSD([sQuery(id+"F4.wireOp",EDGE,"E6")])],"isStart":true});
            var Q198;
            Q198=makeQuery(id+"F5.opExtrude","CAP_EDGE",EDGE,{"disambiguationData":[OSD([sQuery(id+"F4.wireOp",EDGE,"E6")])],"isStart":true});
            var Q199;
            Q199=makeQuery(id+"F5.opExtrude","CAP_EDGE",EDGE,{"disambiguationData":[OSD([sQuery(id+"F4.wireOp",EDGE,"E6")])],"isStart":true});
            var Q200;
            Q200=makeQuery(id+"F5.opExtrude","CAP_EDGE",EDGE,{"disambiguationData":[OSD([sQuery(id+"F4.wireOp",EDGE,"E6")])],"isStart":true});
            var Q201;
            Q201=makeQuery(id+"F5.opExtrude","CAP_EDGE",EDGE,{"disambiguationData":[OSD([sQuery(id+"F4.wireOp",EDGE,"E6")])],"isStart":true});
            var Q202;
            Q202=makeQuery(id+"F5.opExtrude","CAP_EDGE",EDGE,{"disambiguationData":[OSD([sQuery(id+"F4.wireOp",EDGE,"E6")])],"isStart":true});
            var Q203;
            Q203=makeQuery(id+"F5.opExtrude","CAP_EDGE",EDGE,{"disambiguationData":[OSD([sQuery(id+"F4.wireOp",EDGE,"E6")])],"isStart":true});
            var Q204;
            Q204=makeQuery(id+"F5.opExtrude","CAP_EDGE",EDGE,{"disambiguationData":[OSD([sQuery(id+"F4.wireOp",EDGE,"E6")])],"isStart":true});
            var Q205;
            Q205=makeQuery(id+"F5.opExtrude","CAP_EDGE",EDGE,{"disambiguationData":[OSD([sQuery(id+"F4.wireOp",EDGE,"E6")])],"isStart":true});
            var Q206;
            Q206=makeQuery(id+"F5.opExtrude","CAP_EDGE",EDGE,{"disambiguationData":[OSD([sQuery(id+"F4.wireOp",EDGE,"E6")])],"isStart":true});
            var Q207;
            Q207=makeQuery(id+"F5.opExtrude","CAP_EDGE",EDGE,{"disambiguationData":[OSD([sQuery(id+"F4.wireOp",EDGE,"E6")])],"isStart":true});
            var Q208;
            Q208=makeQuery(id+"F5.opExtrude","CAP_EDGE",EDGE,{"disambiguationData":[OSD([sQuery(id+"F4.wireOp",EDGE,"E6")])],"isStart":true});
            var Q209;
            Q209=makeQuery(id+"F5.opExtrude","CAP_EDGE",EDGE,{"disambiguationData":[OSD([sQuery(id+"F4.wireOp",EDGE,"E6")])],"isStart":true});
            var Q210;
            Q210=makeQuery(id+"F5.opExtrude","CAP_EDGE",EDGE,{"disambiguationData":[OSD([sQuery(id+"F4.wireOp",EDGE,"E6")])],"isStart":true});
            var Q211;
            Q211=makeQuery(id+"F5.opExtrude","CAP_EDGE",EDGE,{"disambiguationData":[OSD([sQuery(id+"F4.wireOp",EDGE,"E6")])],"isStart":true});
            var Q212;
            Q212=makeQuery(id+"F5.opExtrude","CAP_EDGE",EDGE,{"disambiguationData":[OSD([sQuery(id+"F4.wireOp",EDGE,"E6")])],"isStart":true});
            var Q213;
            Q213=makeQuery(id+"F5.opExtrude","CAP_EDGE",EDGE,{"disambiguationData":[OSD([sQuery(id+"F4.wireOp",EDGE,"E6")])],"isStart":true});
            var Q214;
            Q214=makeQuery(id+"F5.opExtrude","CAP_EDGE",EDGE,{"disambiguationData":[OSD([sQuery(id+"F4.wireOp",EDGE,"E6")])],"isStart":true});
            var Q215;
            Q215=makeQuery(id+"F5.opExtrude","CAP_EDGE",EDGE,{"disambiguationData":[OSD([sQuery(id+"F4.wireOp",EDGE,"E6")])],"isStart":true});
            var Q216;
            Q216=makeQuery(id+"F5.opExtrude","CAP_EDGE",EDGE,{"disambiguationData":[OSD([sQuery(id+"F4.wireOp",EDGE,"E6")])],"isStart":true});
            var Q217;
            Q217=makeQuery(id+"F5.opExtrude","CAP_EDGE",EDGE,{"disambiguationData":[OSD([sQuery(id+"F4.wireOp",EDGE,"E6")])],"isStart":true});
            var Q218;
            Q218=makeQuery(id+"F5.opExtrude","CAP_EDGE",EDGE,{"disambiguationData":[OSD([sQuery(id+"F4.wireOp",EDGE,"E6")])],"isStart":true});
            var Q219;
            Q219=makeQuery(id+"F5.opExtrude","CAP_EDGE",EDGE,{"disambiguationData":[OSD([sQuery(id+"F4.wireOp",EDGE,"E6")])],"isStart":true});
            var Q220;
            Q220=makeQuery(id+"F5.opExtrude","CAP_EDGE",EDGE,{"disambiguationData":[OSD([sQuery(id+"F4.wireOp",EDGE,"E6")])],"isStart":true});
            var Q221;
            Q221=makeQuery(id+"F5.opExtrude","CAP_EDGE",EDGE,{"disambiguationData":[OSD([sQuery(id+"F4.wireOp",EDGE,"E6")])],"isStart":true});
            var Q222;
            Q222=makeQuery(id+"F5.opExtrude","CAP_EDGE",EDGE,{"disambiguationData":[OSD([sQuery(id+"F4.wireOp",EDGE,"E6")])],"isStart":true});
            var Q223;
            Q223=makeQuery(id+"F5.opExtrude","CAP_EDGE",EDGE,{"disambiguationData":[OSD([sQuery(id+"F4.wireOp",EDGE,"E6")])],"isStart":true});
            var Q224;
            Q224=makeQuery(id+"F5.opExtrude","CAP_EDGE",EDGE,{"disambiguationData":[OSD([sQuery(id+"F4.wireOp",EDGE,"E6")])],"isStart":true});
            var Q225;
            Q225=makeQuery(id+"F5.opExtrude","CAP_EDGE",EDGE,{"disambiguationData":[OSD([sQuery(id+"F4.wireOp",EDGE,"E6")])],"isStart":true});
            var Q226;
            Q226=makeQuery(id+"F5.opExtrude","CAP_EDGE",EDGE,{"disambiguationData":[OSD([sQuery(id+"F4.wireOp",EDGE,"E6")])],"isStart":true});
            var Q227;
            Q227=makeQuery(id+"F5.opExtrude","CAP_EDGE",EDGE,{"disambiguationData":[OSD([sQuery(id+"F4.wireOp",EDGE,"E6")])],"isStart":true});
            var Q228;
            Q228=makeQuery(id+"F5.opExtrude","CAP_EDGE",EDGE,{"disambiguationData":[OSD([sQuery(id+"F4.wireOp",EDGE,"E6")])],"isStart":true});
            var Q229;
            Q229=makeQuery(id+"F5.opExtrude","CAP_EDGE",EDGE,{"disambiguationData":[OSD([sQuery(id+"F4.wireOp",EDGE,"E6")])],"isStart":true});
            var Q230;
            Q230=makeQuery(id+"F5.opExtrude","CAP_EDGE",EDGE,{"disambiguationData":[OSD([sQuery(id+"F4.wireOp",EDGE,"E6")])],"isStart":true});
            var Q231;
            Q231=makeQuery(id+"F5.opExtrude","CAP_EDGE",EDGE,{"disambiguationData":[OSD([sQuery(id+"F4.wireOp",EDGE,"E6")])],"isStart":true});
            var Q232;
            Q232=makeQuery(id+"F5.opExtrude","CAP_EDGE",EDGE,{"disambiguationData":[OSD([sQuery(id+"F4.wireOp",EDGE,"E6")])],"isStart":true});
            var Q233;
            Q233=makeQuery(id+"F5.opExtrude","CAP_EDGE",EDGE,{"disambiguationData":[OSD([sQuery(id+"F4.wireOp",EDGE,"E6")])],"isStart":true});
            var Q234;
            Q234=makeQuery(id+"F5.opExtrude","CAP_EDGE",EDGE,{"disambiguationData":[OSD([sQuery(id+"F4.wireOp",EDGE,"E6")])],"isStart":true});
            var Q235;
            Q235=makeQuery(id+"F5.opExtrude","CAP_EDGE",EDGE,{"disambiguationData":[OSD([sQuery(id+"F4.wireOp",EDGE,"E6")])],"isStart":true});
            var Q236;
            Q236=makeQuery(id+"F5.opExtrude","CAP_EDGE",EDGE,{"disambiguationData":[OSD([sQuery(id+"F4.wireOp",EDGE,"E6")])],"isStart":true});
            var Q237;
            Q237=makeQuery(id+"F5.opExtrude","CAP_EDGE",EDGE,{"disambiguationData":[OSD([sQuery(id+"F4.wireOp",EDGE,"E6")])],"isStart":true});
            var Q238;
            Q238=makeQuery(id+"F5.opExtrude","CAP_EDGE",EDGE,{"disambiguationData":[OSD([sQuery(id+"F4.wireOp",EDGE,"E6")])],"isStart":true});
            var Q239;
            Q239=makeQuery(id+"F5.opExtrude","CAP_EDGE",EDGE,{"disambiguationData":[OSD([sQuery(id+"F4.wireOp",EDGE,"E6")])],"isStart":true});
            var Q240;
            Q240=makeQuery(id+"F5.opExtrude","CAP_EDGE",EDGE,{"disambiguationData":[OSD([sQuery(id+"F4.wireOp",EDGE,"E6")])],"isStart":true});
            var Q241;
            Q241=makeQuery(id+"F5.opExtrude","CAP_EDGE",EDGE,{"disambiguationData":[OSD([sQuery(id+"F4.wireOp",EDGE,"E6")])],"isStart":true});
            var Q242;
            Q242=makeQuery(id+"F5.opExtrude","CAP_EDGE",EDGE,{"disambiguationData":[OSD([sQuery(id+"F4.wireOp",EDGE,"E6")])],"isStart":true});
            var Q243;
            Q243=makeQuery(id+"F5.opExtrude","CAP_EDGE",EDGE,{"disambiguationData":[OSD([sQuery(id+"F4.wireOp",EDGE,"E6")])],"isStart":true});
            var Q244;
            Q244=makeQuery(id+"F5.opExtrude","CAP_EDGE",EDGE,{"disambiguationData":[OSD([sQuery(id+"F4.wireOp",EDGE,"E6")])],"isStart":true});
            var Q245;
            Q245=makeQuery(id+"F5.opExtrude","CAP_EDGE",EDGE,{"disambiguationData":[OSD([sQuery(id+"F4.wireOp",EDGE,"E6")])],"isStart":true});
            var Q246;
            Q246=makeQuery(id+"F5.opExtrude","CAP_EDGE",EDGE,{"disambiguationData":[OSD([sQuery(id+"F4.wireOp",EDGE,"E6")])],"isStart":true});
            var Q247;
            Q247=makeQuery(id+"F5.opExtrude","CAP_EDGE",EDGE,{"disambiguationData":[OSD([sQuery(id+"F4.wireOp",EDGE,"E6")])],"isStart":true});
            var Q248;
            Q248=makeQuery(id+"F5.opExtrude","CAP_EDGE",EDGE,{"disambiguationData":[OSD([sQuery(id+"F4.wireOp",EDGE,"E6")])],"isStart":true});
            var Q249;
            Q249=makeQuery(id+"F5.opExtrude","CAP_EDGE",EDGE,{"disambiguationData":[OSD([sQuery(id+"F4.wireOp",EDGE,"E6")])],"isStart":true});
            var Q250;
            Q250=makeQuery(id+"F5.opExtrude","CAP_EDGE",EDGE,{"disambiguationData":[OSD([sQuery(id+"F4.wireOp",EDGE,"E6")])],"isStart":true});
            var Q251;
            Q251=makeQuery(id+"F5.opExtrude","CAP_EDGE",EDGE,{"disambiguationData":[OSD([sQuery(id+"F4.wireOp",EDGE,"E6")])],"isStart":true});
            var Q252;
            Q252=makeQuery(id+"F5.opExtrude","CAP_EDGE",EDGE,{"disambiguationData":[OSD([sQuery(id+"F4.wireOp",EDGE,"E6")])],"isStart":true});
            var Q253;
            Q253=makeQuery(id+"F5.opExtrude","CAP_EDGE",EDGE,{"disambiguationData":[OSD([sQuery(id+"F4.wireOp",EDGE,"E6")])],"isStart":true});
            var Q254;
            Q254=makeQuery(id+"F5.opExtrude","CAP_EDGE",EDGE,{"disambiguationData":[OSD([sQuery(id+"F4.wireOp",EDGE,"E6")])],"isStart":true});
            var Q255;
            Q255=makeQuery(id+"F5.opExtrude","CAP_EDGE",EDGE,{"disambiguationData":[OSD([sQuery(id+"F4.wireOp",EDGE,"E6")])],"isStart":true});
            var Q256;
            Q256=makeQuery(id+"F5.opExtrude","CAP_EDGE",EDGE,{"disambiguationData":[OSD([sQuery(id+"F4.wireOp",EDGE,"E6")])],"isStart":true});
            var Q257;
            Q257=makeQuery(id+"F5.opExtrude","CAP_EDGE",EDGE,{"disambiguationData":[OSD([sQuery(id+"F4.wireOp",EDGE,"E6")])],"isStart":true});
            var Q258;
            Q258=makeQuery(id+"F5.opExtrude","CAP_EDGE",EDGE,{"disambiguationData":[OSD([sQuery(id+"F4.wireOp",EDGE,"E6")])],"isStart":true});
            var Q259;
            Q259=makeQuery(id+"F5.opExtrude","CAP_EDGE",EDGE,{"disambiguationData":[OSD([sQuery(id+"F4.wireOp",EDGE,"E6")])],"isStart":true});
            var Q260;
            Q260=makeQuery(id+"F5.opExtrude","CAP_EDGE",EDGE,{"disambiguationData":[OSD([sQuery(id+"F4.wireOp",EDGE,"E6")])],"isStart":true});
            var Q261;
            Q261=makeQuery(id+"F5.opExtrude","CAP_EDGE",EDGE,{"disambiguationData":[OSD([sQuery(id+"F4.wireOp",EDGE,"E6")])],"isStart":true});
            var Q262;
            Q262=makeQuery(id+"F5.opExtrude","CAP_EDGE",EDGE,{"disambiguationData":[OSD([sQuery(id+"F4.wireOp",EDGE,"E6")])],"isStart":true});
            var Q263;
            Q263=makeQuery(id+"F5.opExtrude","CAP_EDGE",EDGE,{"disambiguationData":[OSD([sQuery(id+"F4.wireOp",EDGE,"E6")])],"isStart":true});
            var Q264;
            Q264=makeQuery(id+"F5.opExtrude","CAP_EDGE",EDGE,{"disambiguationData":[OSD([sQuery(id+"F4.wireOp",EDGE,"E6")])],"isStart":true});
            var Q265;
            Q265=makeQuery(id+"F5.opExtrude","CAP_EDGE",EDGE,{"disambiguationData":[OSD([sQuery(id+"F4.wireOp",EDGE,"E6")])],"isStart":true});
            var Q266;
            Q266=makeQuery(id+"F5.opExtrude","CAP_EDGE",EDGE,{"disambiguationData":[OSD([sQuery(id+"F4.wireOp",EDGE,"E6")])],"isStart":true});
            var Q267;
            Q267=makeQuery(id+"F5.opExtrude","CAP_EDGE",EDGE,{"disambiguationData":[OSD([sQuery(id+"F4.wireOp",EDGE,"E6")])],"isStart":true});
            var Q268;
            Q268=makeQuery(id+"F5.opExtrude","CAP_EDGE",EDGE,{"disambiguationData":[OSD([sQuery(id+"F4.wireOp",EDGE,"E6")])],"isStart":true});
            var Q269;
            Q269=makeQuery(id+"F5.opExtrude","CAP_EDGE",EDGE,{"disambiguationData":[OSD([sQuery(id+"F4.wireOp",EDGE,"E6")])],"isStart":true});
            var Q270;
            Q270=makeQuery(id+"F5.opExtrude","CAP_EDGE",EDGE,{"disambiguationData":[OSD([sQuery(id+"F4.wireOp",EDGE,"E6")])],"isStart":true});
            var Q271;
            Q271=makeQuery(id+"F5.opExtrude","CAP_EDGE",EDGE,{"disambiguationData":[OSD([sQuery(id+"F4.wireOp",EDGE,"E6")])],"isStart":true});
            var Q272;
            Q272=makeQuery(id+"F5.opExtrude","CAP_EDGE",EDGE,{"disambiguationData":[OSD([sQuery(id+"F4.wireOp",EDGE,"E6")])],"isStart":true});
            var Q273;
            Q273=makeQuery(id+"F5.opExtrude","CAP_EDGE",EDGE,{"disambiguationData":[OSD([sQuery(id+"F4.wireOp",EDGE,"E6")])],"isStart":true});
            var Q274;
            Q274=makeQuery(id+"F5.opExtrude","CAP_EDGE",EDGE,{"disambiguationData":[OSD([sQuery(id+"F4.wireOp",EDGE,"E6")])],"isStart":true});
            var Q275;
            Q275=makeQuery(id+"F5.opExtrude","CAP_EDGE",EDGE,{"disambiguationData":[OSD([sQuery(id+"F4.wireOp",EDGE,"E6")])],"isStart":true});
            var Q276;
            Q276=makeQuery(id+"F5.opExtrude","CAP_EDGE",EDGE,{"disambiguationData":[OSD([sQuery(id+"F4.wireOp",EDGE,"E6")])],"isStart":true});
            var Q277;
            Q277=makeQuery(id+"F5.opExtrude","CAP_EDGE",EDGE,{"disambiguationData":[OSD([sQuery(id+"F4.wireOp",EDGE,"E6")])],"isStart":true});
            var Q278;
            Q278=makeQuery(id+"F5.opExtrude","CAP_EDGE",EDGE,{"disambiguationData":[OSD([sQuery(id+"F4.wireOp",EDGE,"E6")])],"isStart":true});
            var Q279;
            Q279=makeQuery(id+"F5.opExtrude","CAP_EDGE",EDGE,{"disambiguationData":[OSD([sQuery(id+"F4.wireOp",EDGE,"E6")])],"isStart":true});
            var Q280;
            Q280=makeQuery(id+"F5.opExtrude","CAP_EDGE",EDGE,{"disambiguationData":[OSD([sQuery(id+"F4.wireOp",EDGE,"E6")])],"isStart":true});
            var Q281;
            Q281=makeQuery(id+"F5.opExtrude","CAP_EDGE",EDGE,{"disambiguationData":[OSD([sQuery(id+"F4.wireOp",EDGE,"E6")])],"isStart":true});
            var Q282;
            Q282=makeQuery(id+"F5.opExtrude","CAP_EDGE",EDGE,{"disambiguationData":[OSD([sQuery(id+"F4.wireOp",EDGE,"E6")])],"isStart":true});
            var Q283;
            Q283=makeQuery(id+"F5.opExtrude","CAP_EDGE",EDGE,{"disambiguationData":[OSD([sQuery(id+"F4.wireOp",EDGE,"E6")])],"isStart":true});
            var Q284;
            Q284=makeQuery(id+"F5.opExtrude","CAP_EDGE",EDGE,{"disambiguationData":[OSD([sQuery(id+"F4.wireOp",EDGE,"E6")])],"isStart":true});
            var Q285;
            Q285=makeQuery(id+"F5.opExtrude","CAP_EDGE",EDGE,{"disambiguationData":[OSD([sQuery(id+"F4.wireOp",EDGE,"E6")])],"isStart":true});
            var Q286;
            Q286=makeQuery(id+"F5.opExtrude","CAP_EDGE",EDGE,{"disambiguationData":[OSD([sQuery(id+"F4.wireOp",EDGE,"E6")])],"isStart":true});
            var Q287;
            Q287=makeQuery(id+"F5.opExtrude","CAP_EDGE",EDGE,{"disambiguationData":[OSD([sQuery(id+"F4.wireOp",EDGE,"E6")])],"isStart":true});
            var Q288;
            Q288=makeQuery(id+"F5.opExtrude","CAP_EDGE",EDGE,{"disambiguationData":[OSD([sQuery(id+"F4.wireOp",EDGE,"E6")])],"isStart":true});
            var Q289;
            Q289=makeQuery(id+"F5.opExtrude","CAP_EDGE",EDGE,{"disambiguationData":[OSD([sQuery(id+"F4.wireOp",EDGE,"E6")])],"isStart":true});
            var Q290;
            Q290=makeQuery(id+"F5.opExtrude","CAP_EDGE",EDGE,{"disambiguationData":[OSD([sQuery(id+"F4.wireOp",EDGE,"E6")])],"isStart":true});
            var Q291;
            Q291=makeQuery(id+"F5.opExtrude","CAP_EDGE",EDGE,{"disambiguationData":[OSD([sQuery(id+"F4.wireOp",EDGE,"E6")])],"isStart":true});
            var Q292;
            Q292=makeQuery(id+"F5.opExtrude","CAP_EDGE",EDGE,{"disambiguationData":[OSD([sQuery(id+"F4.wireOp",EDGE,"E6")])],"isStart":true});
            var Q293;
            Q293=makeQuery(id+"F5.opExtrude","CAP_EDGE",EDGE,{"disambiguationData":[OSD([sQuery(id+"F4.wireOp",EDGE,"E6")])],"isStart":true});
            var Q294;
            Q294=makeQuery(id+"F5.opExtrude","CAP_EDGE",EDGE,{"disambiguationData":[OSD([sQuery(id+"F4.wireOp",EDGE,"E6")])],"isStart":true});
            var Q295;
            Q295=makeQuery(id+"F5.opExtrude","CAP_EDGE",EDGE,{"disambiguationData":[OSD([sQuery(id+"F4.wireOp",EDGE,"E6")])],"isStart":true});
            var Q296;
            Q296=makeQuery(id+"F5.opExtrude","CAP_EDGE",EDGE,{"disambiguationData":[OSD([sQuery(id+"F4.wireOp",EDGE,"E6")])],"isStart":true});
            var Q297;
            Q297=makeQuery(id+"F5.opExtrude","CAP_EDGE",EDGE,{"disambiguationData":[OSD([sQuery(id+"F4.wireOp",EDGE,"E6")])],"isStart":true});
            var Q298;
            Q298=makeQuery(id+"F5.opExtrude","CAP_EDGE",EDGE,{"disambiguationData":[OSD([sQuery(id+"F4.wireOp",EDGE,"E6")])],"isStart":true});
            var Q299;
            Q299=makeQuery(id+"F5.opExtrude","CAP_EDGE",EDGE,{"disambiguationData":[OSD([sQuery(id+"F4.wireOp",EDGE,"E6")])],"isStart":true});
            var Q300;
            Q300=makeQuery(id+"F5.opExtrude","CAP_EDGE",EDGE,{"disambiguationData":[OSD([sQuery(id+"F4.wireOp",EDGE,"E6")])],"isStart":true});
            var Q301;
            Q301=makeQuery(id+"F5.opExtrude","CAP_EDGE",EDGE,{"disambiguationData":[OSD([sQuery(id+"F4.wireOp",EDGE,"E6")])],"isStart":true});
            var Q302;
            Q302=makeQuery(id+"F5.opExtrude","CAP_EDGE",EDGE,{"disambiguationData":[OSD([sQuery(id+"F4.wireOp",EDGE,"E6")])],"isStart":true});
            var Q303;
            Q303=makeQuery(id+"F5.opExtrude","CAP_EDGE",EDGE,{"disambiguationData":[OSD([sQuery(id+"F4.wireOp",EDGE,"E6")])],"isStart":true});
            var Q304;
            Q304=makeQuery(id+"F5.opExtrude","CAP_EDGE",EDGE,{"disambiguationData":[OSD([sQuery(id+"F4.wireOp",EDGE,"E6")])],"isStart":true});
            var Q305;
            Q305=makeQuery(id+"F5.opExtrude","CAP_EDGE",EDGE,{"disambiguationData":[OSD([sQuery(id+"F4.wireOp",EDGE,"E6")])],"isStart":true});
            var Q306;
            Q306=makeQuery(id+"F5.opExtrude","CAP_EDGE",EDGE,{"disambiguationData":[OSD([sQuery(id+"F4.wireOp",EDGE,"E6")])],"isStart":true});
            var Q307;
            Q307=makeQuery(id+"F5.opExtrude","CAP_EDGE",EDGE,{"disambiguationData":[OSD([sQuery(id+"F4.wireOp",EDGE,"E6")])],"isStart":true});
            var Q308;
            Q308=makeQuery(id+"F5.opExtrude","CAP_EDGE",EDGE,{"disambiguationData":[OSD([sQuery(id+"F4.wireOp",EDGE,"E6")])],"isStart":true});
            var Q309;
            Q309=makeQuery(id+"F5.opExtrude","CAP_EDGE",EDGE,{"disambiguationData":[OSD([sQuery(id+"F4.wireOp",EDGE,"E6")])],"isStart":true});
            var Q310;
            Q310=makeQuery(id+"F5.opExtrude","CAP_EDGE",EDGE,{"disambiguationData":[OSD([sQuery(id+"F4.wireOp",EDGE,"E6")])],"isStart":true});
            var Q311;
            Q311=makeQuery(id+"F5.opExtrude","CAP_EDGE",EDGE,{"disambiguationData":[OSD([sQuery(id+"F4.wireOp",EDGE,"E6")])],"isStart":true});
            var Q312;
            Q312=makeQuery(id+"F5.opExtrude","CAP_EDGE",EDGE,{"disambiguationData":[OSD([sQuery(id+"F4.wireOp",EDGE,"E6")])],"isStart":true});
            var Q313;
            Q313=makeQuery(id+"F5.opExtrude","CAP_EDGE",EDGE,{"disambiguationData":[OSD([sQuery(id+"F4.wireOp",EDGE,"E6")])],"isStart":true});
            var Q314;
            Q314=makeQuery(id+"F5.opExtrude","CAP_EDGE",EDGE,{"disambiguationData":[OSD([sQuery(id+"F4.wireOp",EDGE,"E6")])],"isStart":true});
            var Q315;
            Q315=makeQuery(id+"F5.opExtrude","CAP_EDGE",EDGE,{"disambiguationData":[OSD([sQuery(id+"F4.wireOp",EDGE,"E6")])],"isStart":true});
            var Q316;
            Q316=makeQuery(id+"F5.opExtrude","CAP_EDGE",EDGE,{"disambiguationData":[OSD([sQuery(id+"F4.wireOp",EDGE,"E6")])],"isStart":true});
            var Q317;
            Q317=makeQuery(id+"F5.opExtrude","CAP_EDGE",EDGE,{"disambiguationData":[OSD([sQuery(id+"F4.wireOp",EDGE,"E6")])],"isStart":true});
            var Q318;
            Q318=makeQuery(id+"F5.opExtrude","CAP_EDGE",EDGE,{"disambiguationData":[OSD([sQuery(id+"F4.wireOp",EDGE,"E6")])],"isStart":true});
            var Q319;
            Q319=makeQuery(id+"F5.opExtrude","CAP_EDGE",EDGE,{"disambiguationData":[OSD([sQuery(id+"F4.wireOp",EDGE,"E6")])],"isStart":true});
            var Q320;
            Q320=makeQuery(id+"F5.opExtrude","CAP_EDGE",EDGE,{"disambiguationData":[OSD([sQuery(id+"F4.wireOp",EDGE,"E6")])],"isStart":true});
            var Q321;
            Q321=makeQuery(id+"F5.opExtrude","CAP_EDGE",EDGE,{"disambiguationData":[OSD([sQuery(id+"F4.wireOp",EDGE,"E6")])],"isStart":true});
            var Q322;
            Q322=makeQuery(id+"F5.opExtrude","CAP_EDGE",EDGE,{"disambiguationData":[OSD([sQuery(id+"F4.wireOp",EDGE,"E6")])],"isStart":true});
            var Q323;
            Q323=makeQuery(id+"F5.opExtrude","CAP_EDGE",EDGE,{"disambiguationData":[OSD([sQuery(id+"F4.wireOp",EDGE,"E6")])],"isStart":true});
            var Q324;
            Q324=makeQuery(id+"F5.opExtrude","CAP_EDGE",EDGE,{"disambiguationData":[OSD([sQuery(id+"F4.wireOp",EDGE,"E6")])],"isStart":true});
            var Q325;
            Q325=makeQuery(id+"F5.opExtrude","CAP_EDGE",EDGE,{"disambiguationData":[OSD([sQuery(id+"F4.wireOp",EDGE,"E6")])],"isStart":true});
            var Q326;
            Q326=makeQuery(id+"F5.opExtrude","CAP_EDGE",EDGE,{"disambiguationData":[OSD([sQuery(id+"F4.wireOp",EDGE,"E6")])],"isStart":true});
            var Q327;
            Q327=makeQuery(id+"F5.opExtrude","CAP_EDGE",EDGE,{"disambiguationData":[OSD([sQuery(id+"F4.wireOp",EDGE,"E6")])],"isStart":true});
            var Q328;
            Q328=makeQuery(id+"F5.opExtrude","CAP_EDGE",EDGE,{"disambiguationData":[OSD([sQuery(id+"F4.wireOp",EDGE,"E6")])],"isStart":true});
            var Q329;
            Q329=makeQuery(id+"F5.opExtrude","CAP_EDGE",EDGE,{"disambiguationData":[OSD([sQuery(id+"F4.wireOp",EDGE,"E6")])],"isStart":true});
            var Q330;
            Q330=makeQuery(id+"F5.opExtrude","CAP_EDGE",EDGE,{"disambiguationData":[OSD([sQuery(id+"F4.wireOp",EDGE,"E6")])],"isStart":true});
            var Q331;
            Q331=makeQuery(id+"F5.opExtrude","CAP_EDGE",EDGE,{"disambiguationData":[OSD([sQuery(id+"F4.wireOp",EDGE,"E6")])],"isStart":true});
            var Q332;
            Q332=makeQuery(id+"F5.opExtrude","CAP_EDGE",EDGE,{"disambiguationData":[OSD([sQuery(id+"F4.wireOp",EDGE,"E6")])],"isStart":true});
            var Q333;
            Q333=makeQuery(id+"F5.opExtrude","CAP_EDGE",EDGE,{"disambiguationData":[OSD([sQuery(id+"F4.wireOp",EDGE,"E6")])],"isStart":true});
            var Q334;
            Q334=makeQuery(id+"F5.opExtrude","CAP_EDGE",EDGE,{"disambiguationData":[OSD([sQuery(id+"F4.wireOp",EDGE,"E6")])],"isStart":true});
            var Q335;
            Q335=makeQuery(id+"F5.opExtrude","CAP_EDGE",EDGE,{"disambiguationData":[OSD([sQuery(id+"F4.wireOp",EDGE,"E6")])],"isStart":true});
            var Q336;
            Q336=makeQuery(id+"F5.opExtrude","CAP_EDGE",EDGE,{"disambiguationData":[OSD([sQuery(id+"F4.wireOp",EDGE,"E6")])],"isStart":true});
            var Q337;
            Q337=makeQuery(id+"F5.opExtrude","CAP_EDGE",EDGE,{"disambiguationData":[OSD([sQuery(id+"F4.wireOp",EDGE,"E6")])],"isStart":true});
            var Q338;
            Q338=makeQuery(id+"F5.opExtrude","CAP_EDGE",EDGE,{"disambiguationData":[OSD([sQuery(id+"F4.wireOp",EDGE,"E6")])],"isStart":true});
            var Q339;
            Q339=makeQuery(id+"F5.opExtrude","CAP_EDGE",EDGE,{"disambiguationData":[OSD([sQuery(id+"F4.wireOp",EDGE,"E6")])],"isStart":true});
            var Q340;
            Q340=makeQuery(id+"F5.opExtrude","CAP_EDGE",EDGE,{"disambiguationData":[OSD([sQuery(id+"F4.wireOp",EDGE,"E6")])],"isStart":true});
            var Q341;
            Q341=makeQuery(id+"F5.opExtrude","CAP_EDGE",EDGE,{"disambiguationData":[OSD([sQuery(id+"F4.wireOp",EDGE,"E6")])],"isStart":true});
            var Q342;
            Q342=makeQuery(id+"F5.opExtrude","CAP_EDGE",EDGE,{"disambiguationData":[OSD([sQuery(id+"F4.wireOp",EDGE,"E6")])],"isStart":true});
            var Q343;
            Q343=makeQuery(id+"F5.opExtrude","CAP_EDGE",EDGE,{"disambiguationData":[OSD([sQuery(id+"F4.wireOp",EDGE,"E6")])],"isStart":true});
            var Q344;
            Q344=makeQuery(id+"F5.opExtrude","CAP_EDGE",EDGE,{"disambiguationData":[OSD([sQuery(id+"F4.wireOp",EDGE,"E6")])],"isStart":true});
            var Q345;
            Q345=makeQuery(id+"F5.opExtrude","CAP_EDGE",EDGE,{"disambiguationData":[OSD([sQuery(id+"F4.wireOp",EDGE,"E6")])],"isStart":true});
            var Q346;
            Q346=makeQuery(id+"F5.opExtrude","CAP_EDGE",EDGE,{"disambiguationData":[OSD([sQuery(id+"F4.wireOp",EDGE,"E6")])],"isStart":true});
            var Q347;
            Q347=makeQuery(id+"F5.opExtrude","CAP_EDGE",EDGE,{"disambiguationData":[OSD([sQuery(id+"F4.wireOp",EDGE,"E6")])],"isStart":true});
            var Q348;
            Q348=makeQuery(id+"F5.opExtrude","CAP_EDGE",EDGE,{"disambiguationData":[OSD([sQuery(id+"F4.wireOp",EDGE,"E6")])],"isStart":true});
            var Q349;
            Q349=makeQuery(id+"F5.opExtrude","CAP_EDGE",EDGE,{"disambiguationData":[OSD([sQuery(id+"F4.wireOp",EDGE,"E6")])],"isStart":true});
            var Q350;
            Q350=makeQuery(id+"F5.opExtrude","CAP_EDGE",EDGE,{"disambiguationData":[OSD([sQuery(id+"F4.wireOp",EDGE,"E6")])],"isStart":true});
            var Q351;
            Q351=makeQuery(id+"F5.opExtrude","CAP_EDGE",EDGE,{"disambiguationData":[OSD([sQuery(id+"F4.wireOp",EDGE,"E6")])],"isStart":true});
            var Q352;
            Q352=makeQuery(id+"F5.opExtrude","CAP_EDGE",EDGE,{"disambiguationData":[OSD([sQuery(id+"F4.wireOp",EDGE,"E6")])],"isStart":true});
            var Q353;
            Q353=makeQuery(id+"F5.opExtrude","CAP_EDGE",EDGE,{"disambiguationData":[OSD([sQuery(id+"F4.wireOp",EDGE,"E6")])],"isStart":true});
            var Q354;
            Q354=makeQuery(id+"F5.opExtrude","CAP_EDGE",EDGE,{"disambiguationData":[OSD([sQuery(id+"F4.wireOp",EDGE,"E6")])],"isStart":true});
            var Q355;
            Q355=makeQuery(id+"F5.opExtrude","CAP_EDGE",EDGE,{"disambiguationData":[OSD([sQuery(id+"F4.wireOp",EDGE,"E6")])],"isStart":true});
            var Q356;
            Q356=makeQuery(id+"F5.opExtrude","CAP_EDGE",EDGE,{"disambiguationData":[OSD([sQuery(id+"F4.wireOp",EDGE,"E6")])],"isStart":true});
            var Q357;
            Q357=makeQuery(id+"F5.opExtrude","CAP_EDGE",EDGE,{"disambiguationData":[OSD([sQuery(id+"F4.wireOp",EDGE,"E6")])],"isStart":true});
            var Q358;
            Q358=makeQuery(id+"F5.opExtrude","CAP_EDGE",EDGE,{"disambiguationData":[OSD([sQuery(id+"F4.wireOp",EDGE,"E6")])],"isStart":true});
            var Q359;
            Q359=makeQuery(id+"F5.opExtrude","CAP_EDGE",EDGE,{"disambiguationData":[OSD([sQuery(id+"F4.wireOp",EDGE,"E6")])],"isStart":true});
            var Q360;
            Q360=makeQuery(id+"F5.opExtrude","CAP_EDGE",EDGE,{"disambiguationData":[OSD([sQuery(id+"F4.wireOp",EDGE,"E6")])],"isStart":true});
            var Q361;
            Q361=makeQuery(id+"F5.opExtrude","CAP_EDGE",EDGE,{"disambiguationData":[OSD([sQuery(id+"F4.wireOp",EDGE,"E6")])],"isStart":true});
            var Q362;
            Q362=makeQuery(id+"F5.opExtrude","CAP_EDGE",EDGE,{"disambiguationData":[OSD([sQuery(id+"F4.wireOp",EDGE,"E6")])],"isStart":true});
            var Q363;
            Q363=makeQuery(id+"F5.opExtrude","CAP_EDGE",EDGE,{"disambiguationData":[OSD([sQuery(id+"F4.wireOp",EDGE,"E6")])],"isStart":true});
            var Q364;
            Q364=makeQuery(id+"F5.opExtrude","CAP_EDGE",EDGE,{"disambiguationData":[OSD([sQuery(id+"F4.wireOp",EDGE,"E6")])],"isStart":true});
            var Q365;
            Q365=makeQuery(id+"F5.opExtrude","CAP_EDGE",EDGE,{"disambiguationData":[OSD([sQuery(id+"F4.wireOp",EDGE,"E6")])],"isStart":true});
            var Q366;
            Q366=makeQuery(id+"F5.opExtrude","CAP_EDGE",EDGE,{"disambiguationData":[OSD([sQuery(id+"F4.wireOp",EDGE,"E6")])],"isStart":true});
            var Q367;
            Q367=makeQuery(id+"F5.opExtrude","CAP_EDGE",EDGE,{"disambiguationData":[OSD([sQuery(id+"F4.wireOp",EDGE,"E6")])],"isStart":true});
            var Q368;
            Q368=makeQuery(id+"F5.opExtrude","CAP_EDGE",EDGE,{"disambiguationData":[OSD([sQuery(id+"F4.wireOp",EDGE,"E6")])],"isStart":true});
            var Q369;
            Q369=makeQuery(id+"F5.opExtrude","CAP_EDGE",EDGE,{"disambiguationData":[OSD([sQuery(id+"F4.wireOp",EDGE,"E6")])],"isStart":true});
            var Q370;
            Q370=makeQuery(id+"F5.opExtrude","CAP_EDGE",EDGE,{"disambiguationData":[OSD([sQuery(id+"F4.wireOp",EDGE,"E6")])],"isStart":true});
            var Q371;
            Q371=makeQuery(id+"F5.opExtrude","CAP_EDGE",EDGE,{"disambiguationData":[OSD([sQuery(id+"F4.wireOp",EDGE,"E6")])],"isStart":true});
            var Q372;
            Q372=makeQuery(id+"F5.opExtrude","CAP_EDGE",EDGE,{"disambiguationData":[OSD([sQuery(id+"F4.wireOp",EDGE,"E6")])],"isStart":true});
            var Q373;
            Q373=makeQuery(id+"F5.opExtrude","CAP_EDGE",EDGE,{"disambiguationData":[OSD([sQuery(id+"F4.wireOp",EDGE,"E6")])],"isStart":true});
            var Q374;
            Q374=makeQuery(id+"F5.opExtrude","CAP_EDGE",EDGE,{"disambiguationData":[OSD([sQuery(id+"F4.wireOp",EDGE,"E6")])],"isStart":true});
            var Q375;
            Q375=makeQuery(id+"F5.opExtrude","CAP_EDGE",EDGE,{"disambiguationData":[OSD([sQuery(id+"F4.wireOp",EDGE,"E6")])],"isStart":true});
            var Q376;
            Q376=makeQuery(id+"F5.opExtrude","CAP_EDGE",EDGE,{"disambiguationData":[OSD([sQuery(id+"F4.wireOp",EDGE,"E6")])],"isStart":true});
            var Q377;
            Q377=makeQuery(id+"F5.opExtrude","CAP_EDGE",EDGE,{"disambiguationData":[OSD([sQuery(id+"F4.wireOp",EDGE,"E6")])],"isStart":true});
            var Q378;
            Q378=makeQuery(id+"F5.opExtrude","CAP_EDGE",EDGE,{"disambiguationData":[OSD([sQuery(id+"F4.wireOp",EDGE,"E6")])],"isStart":true});
            var Q379;
            Q379=makeQuery(id+"F5.opExtrude","CAP_EDGE",EDGE,{"disambiguationData":[OSD([sQuery(id+"F4.wireOp",EDGE,"E6")])],"isStart":true});
            var Q380;
            Q380=makeQuery(id+"F5.opExtrude","CAP_EDGE",EDGE,{"disambiguationData":[OSD([sQuery(id+"F4.wireOp",EDGE,"E6")])],"isStart":true});
            var Q381;
            Q381=makeQuery(id+"F5.opExtrude","CAP_EDGE",EDGE,{"disambiguationData":[OSD([sQuery(id+"F4.wireOp",EDGE,"E6")])],"isStart":true});
            var Q382;
            Q382=makeQuery(id+"F5.opExtrude","CAP_EDGE",EDGE,{"disambiguationData":[OSD([sQuery(id+"F4.wireOp",EDGE,"E6")])],"isStart":true});
            var Q383;
            Q383=makeQuery(id+"F5.opExtrude","CAP_EDGE",EDGE,{"disambiguationData":[OSD([sQuery(id+"F4.wireOp",EDGE,"E6")])],"isStart":true});
            var Q384;
            Q384=makeQuery(id+"F5.opExtrude","CAP_EDGE",EDGE,{"disambiguationData":[OSD([sQuery(id+"F4.wireOp",EDGE,"E6")])],"isStart":true});
            var Q385;
            Q385=makeQuery(id+"F5.opExtrude","CAP_EDGE",EDGE,{"disambiguationData":[OSD([sQuery(id+"F4.wireOp",EDGE,"E6")])],"isStart":true});
            var Q386;
            Q386=makeQuery(id+"F5.opExtrude","CAP_EDGE",EDGE,{"disambiguationData":[OSD([sQuery(id+"F4.wireOp",EDGE,"E6")])],"isStart":true});
            var Q387;
            Q387=makeQuery(id+"F5.opExtrude","CAP_EDGE",EDGE,{"disambiguationData":[OSD([sQuery(id+"F4.wireOp",EDGE,"E6")])],"isStart":true});
            var Q388;
            Q388=makeQuery(id+"F5.opExtrude","CAP_EDGE",EDGE,{"disambiguationData":[OSD([sQuery(id+"F4.wireOp",EDGE,"E6")])],"isStart":true});
            var Q389;
            Q389=makeQuery(id+"F5.opExtrude","CAP_EDGE",EDGE,{"disambiguationData":[OSD([sQuery(id+"F4.wireOp",EDGE,"E6")])],"isStart":true});
            var Q390;
            Q390=makeQuery(id+"F5.opExtrude","CAP_EDGE",EDGE,{"disambiguationData":[OSD([sQuery(id+"F4.wireOp",EDGE,"E6")])],"isStart":true});
            var Q391;
            Q391=makeQuery(id+"F5.opExtrude","CAP_EDGE",EDGE,{"disambiguationData":[OSD([sQuery(id+"F4.wireOp",EDGE,"E6")])],"isStart":true});
            var Q392;
            Q392=makeQuery(id+"F5.opExtrude","CAP_EDGE",EDGE,{"disambiguationData":[OSD([sQuery(id+"F4.wireOp",EDGE,"E6")])],"isStart":true});
            var Q393;
            Q393=makeQuery(id+"F5.opExtrude","CAP_EDGE",EDGE,{"disambiguationData":[OSD([sQuery(id+"F4.wireOp",EDGE,"E6")])],"isStart":true});
            var Q394;
            Q394=makeQuery(id+"F5.opExtrude","CAP_EDGE",EDGE,{"disambiguationData":[OSD([sQuery(id+"F4.wireOp",EDGE,"E6")])],"isStart":true});
            var Q395;
            Q395=makeQuery(id+"F5.opExtrude","CAP_EDGE",EDGE,{"disambiguationData":[OSD([sQuery(id+"F4.wireOp",EDGE,"E6")])],"isStart":true});
            var Q396;
            Q396=makeQuery(id+"F5.opExtrude","CAP_EDGE",EDGE,{"disambiguationData":[OSD([sQuery(id+"F4.wireOp",EDGE,"E6")])],"isStart":true});
            var Q397;
            Q397=makeQuery(id+"F5.opExtrude","CAP_EDGE",EDGE,{"disambiguationData":[OSD([sQuery(id+"F4.wireOp",EDGE,"E6")])],"isStart":true});
            var Q398;
            Q398=makeQuery(id+"F5.opExtrude","CAP_EDGE",EDGE,{"disambiguationData":[OSD([sQuery(id+"F4.wireOp",EDGE,"E6")])],"isStart":true});
            var Q399;
            Q399=makeQuery(id+"F5.opExtrude","CAP_EDGE",EDGE,{"disambiguationData":[OSD([sQuery(id+"F4.wireOp",EDGE,"E6")])],"isStart":true});
            var Q400;
            Q400=makeQuery(id+"F5.opExtrude","CAP_EDGE",EDGE,{"disambiguationData":[OSD([sQuery(id+"F4.wireOp",EDGE,"E6")])],"isStart":true});
            var Q401;
            Q401=makeQuery(id+"F5.opExtrude","CAP_EDGE",EDGE,{"disambiguationData":[OSD([sQuery(id+"F4.wireOp",EDGE,"E6")])],"isStart":true});
            var Q402;
            Q402=makeQuery(id+"F5.opExtrude","CAP_EDGE",EDGE,{"disambiguationData":[OSD([sQuery(id+"F4.wireOp",EDGE,"E6")])],"isStart":true});
            var Q403;
            Q403=makeQuery(id+"F5.opExtrude","CAP_EDGE",EDGE,{"disambiguationData":[OSD([sQuery(id+"F4.wireOp",EDGE,"E6")])],"isStart":true});
            var Q404;
            Q404=makeQuery(id+"F5.opExtrude","CAP_EDGE",EDGE,{"disambiguationData":[OSD([sQuery(id+"F4.wireOp",EDGE,"E6")])],"isStart":true});
            var Q405;
            Q405=makeQuery(id+"F5.opExtrude","CAP_EDGE",EDGE,{"disambiguationData":[OSD([sQuery(id+"F4.wireOp",EDGE,"E6")])],"isStart":true});
            var Q406;
            Q406=makeQuery(id+"F5.opExtrude","CAP_EDGE",EDGE,{"disambiguationData":[OSD([sQuery(id+"F4.wireOp",EDGE,"E6")])],"isStart":true});
            var Q407;
            Q407=makeQuery(id+"F5.opExtrude","CAP_EDGE",EDGE,{"disambiguationData":[OSD([sQuery(id+"F4.wireOp",EDGE,"E6")])],"isStart":true});
            var Q408;
            Q408=makeQuery(id+"F5.opExtrude","CAP_EDGE",EDGE,{"disambiguationData":[OSD([sQuery(id+"F4.wireOp",EDGE,"E6")])],"isStart":true});
            var Q409;
            Q409=makeQuery(id+"F5.opExtrude","CAP_EDGE",EDGE,{"disambiguationData":[OSD([sQuery(id+"F4.wireOp",EDGE,"E6")])],"isStart":true});
            var Q410;
            Q410=makeQuery(id+"F5.opExtrude","CAP_EDGE",EDGE,{"disambiguationData":[OSD([sQuery(id+"F4.wireOp",EDGE,"E6")])],"isStart":true});
            var Q411;
            Q411=makeQuery(id+"F5.opExtrude","CAP_EDGE",EDGE,{"disambiguationData":[OSD([sQuery(id+"F4.wireOp",EDGE,"E6")])],"isStart":true});
            var Q412;
            Q412=makeQuery(id+"F5.opExtrude","CAP_EDGE",EDGE,{"disambiguationData":[OSD([sQuery(id+"F4.wireOp",EDGE,"E6")])],"isStart":true});
            var Q413;
            Q413=makeQuery(id+"F5.opExtrude","CAP_EDGE",EDGE,{"disambiguationData":[OSD([sQuery(id+"F4.wireOp",EDGE,"E6")])],"isStart":true});
            var Q414;
            Q414=makeQuery(id+"F5.opExtrude","CAP_EDGE",EDGE,{"disambiguationData":[OSD([sQuery(id+"F4.wireOp",EDGE,"E6")])],"isStart":true});
            var Q415;
            Q415=makeQuery(id+"F5.opExtrude","CAP_EDGE",EDGE,{"disambiguationData":[OSD([sQuery(id+"F4.wireOp",EDGE,"E6")])],"isStart":true});
            var Q416;
            Q416=makeQuery(id+"F5.opExtrude","CAP_EDGE",EDGE,{"disambiguationData":[OSD([sQuery(id+"F4.wireOp",EDGE,"E6")])],"isStart":true});
            var Q417;
            Q417=makeQuery(id+"F5.opExtrude","CAP_EDGE",EDGE,{"disambiguationData":[OSD([sQuery(id+"F4.wireOp",EDGE,"E6")])],"isStart":true});
            var Q418;
            Q418=makeQuery(id+"F5.opExtrude","CAP_EDGE",EDGE,{"disambiguationData":[OSD([sQuery(id+"F4.wireOp",EDGE,"E6")])],"isStart":true});
            var Q419;
            Q419=makeQuery(id+"F5.opExtrude","CAP_EDGE",EDGE,{"disambiguationData":[OSD([sQuery(id+"F4.wireOp",EDGE,"E6")])],"isStart":true});
            var Q420;
            Q420=makeQuery(id+"F5.opExtrude","CAP_EDGE",EDGE,{"disambiguationData":[OSD([sQuery(id+"F4.wireOp",EDGE,"E6")])],"isStart":true});
            var Q421;
            Q421=makeQuery(id+"F5.opExtrude","CAP_EDGE",EDGE,{"disambiguationData":[OSD([sQuery(id+"F4.wireOp",EDGE,"E6")])],"isStart":true});
            var Q422;
            Q422=makeQuery(id+"F5.opExtrude","CAP_EDGE",EDGE,{"disambiguationData":[OSD([sQuery(id+"F4.wireOp",EDGE,"E6")])],"isStart":true});
            var Q423;
            Q423=makeQuery(id+"F5.opExtrude","CAP_EDGE",EDGE,{"disambiguationData":[OSD([sQuery(id+"F4.wireOp",EDGE,"E6")])],"isStart":true});
            var Q424;
            Q424=makeQuery(id+"F5.opExtrude","CAP_EDGE",EDGE,{"disambiguationData":[OSD([sQuery(id+"F4.wireOp",EDGE,"E6")])],"isStart":true});
            var Q425;
            Q425=makeQuery(id+"F5.opExtrude","CAP_EDGE",EDGE,{"disambiguationData":[OSD([sQuery(id+"F4.wireOp",EDGE,"E6")])],"isStart":true});
            var Q426;
            Q426=makeQuery(id+"F5.opExtrude","CAP_EDGE",EDGE,{"disambiguationData":[OSD([sQuery(id+"F4.wireOp",EDGE,"E6")])],"isStart":true});
            var Q427;
            Q427=makeQuery(id+"F5.opExtrude","CAP_EDGE",EDGE,{"disambiguationData":[OSD([sQuery(id+"F4.wireOp",EDGE,"E6")])],"isStart":true});
            var Q428;
            Q428=makeQuery(id+"F5.opExtrude","CAP_EDGE",EDGE,{"disambiguationData":[OSD([sQuery(id+"F4.wireOp",EDGE,"E6")])],"isStart":true});
            var Q429;
            Q429=makeQuery(id+"F5.opExtrude","CAP_EDGE",EDGE,{"disambiguationData":[OSD([sQuery(id+"F4.wireOp",EDGE,"E6")])],"isStart":true});
            var Q430;
            Q430=makeQuery(id+"F5.opExtrude","CAP_EDGE",EDGE,{"disambiguationData":[OSD([sQuery(id+"F4.wireOp",EDGE,"E6")])],"isStart":true});
            var Q431;
            Q431=makeQuery(id+"F5.opExtrude","CAP_EDGE",EDGE,{"disambiguationData":[OSD([sQuery(id+"F4.wireOp",EDGE,"E6")])],"isStart":true});
            var Q432;
            Q432=makeQuery(id+"F5.opExtrude","CAP_EDGE",EDGE,{"disambiguationData":[OSD([sQuery(id+"F4.wireOp",EDGE,"E6")])],"isStart":true});
            var Q433;
            Q433=makeQuery(id+"F5.opExtrude","CAP_EDGE",EDGE,{"disambiguationData":[OSD([sQuery(id+"F4.wireOp",EDGE,"E6")])],"isStart":true});
            var Q434;
            Q434=makeQuery(id+"F5.opExtrude","CAP_EDGE",EDGE,{"disambiguationData":[OSD([sQuery(id+"F4.wireOp",EDGE,"E6")])],"isStart":true});
            var Q435;
            Q435=makeQuery(id+"F5.opExtrude","CAP_EDGE",EDGE,{"disambiguationData":[OSD([sQuery(id+"F4.wireOp",EDGE,"E6")])],"isStart":true});
            var Q436;
            Q436=makeQuery(id+"F5.opExtrude","CAP_EDGE",EDGE,{"disambiguationData":[OSD([sQuery(id+"F4.wireOp",EDGE,"E6")])],"isStart":true});
            var Q437;
            Q437=makeQuery(id+"F5.opExtrude","CAP_EDGE",EDGE,{"disambiguationData":[OSD([sQuery(id+"F4.wireOp",EDGE,"E6")])],"isStart":true});
            var Q438;
            Q438=makeQuery(id+"F5.opExtrude","CAP_EDGE",EDGE,{"disambiguationData":[OSD([sQuery(id+"F4.wireOp",EDGE,"E6")])],"isStart":true});
            var Q439;
            Q439=makeQuery(id+"F5.opExtrude","CAP_EDGE",EDGE,{"disambiguationData":[OSD([sQuery(id+"F4.wireOp",EDGE,"E6")])],"isStart":true});
            var Q440;
            Q440=makeQuery(id+"F5.opExtrude","CAP_EDGE",EDGE,{"disambiguationData":[OSD([sQuery(id+"F4.wireOp",EDGE,"E6")])],"isStart":true});
            var Q441;
            Q441=makeQuery(id+"F5.opExtrude","CAP_EDGE",EDGE,{"disambiguationData":[OSD([sQuery(id+"F4.wireOp",EDGE,"E6")])],"isStart":true});
            var Q442;
            Q442=makeQuery(id+"F5.opExtrude","CAP_EDGE",EDGE,{"disambiguationData":[OSD([sQuery(id+"F4.wireOp",EDGE,"E6")])],"isStart":true});
            var Q443;
            Q443=makeQuery(id+"F5.opExtrude","CAP_EDGE",EDGE,{"disambiguationData":[OSD([sQuery(id+"F4.wireOp",EDGE,"E6")])],"isStart":true});
            var Q444;
            Q444=makeQuery(id+"F5.opExtrude","CAP_EDGE",EDGE,{"disambiguationData":[OSD([sQuery(id+"F4.wireOp",EDGE,"E6")])],"isStart":true});
            var Q445;
            Q445=makeQuery(id+"F5.opExtrude","CAP_EDGE",EDGE,{"disambiguationData":[OSD([sQuery(id+"F4.wireOp",EDGE,"E6")])],"isStart":true});
            var Q446;
            Q446=makeQuery(id+"F5.opExtrude","CAP_EDGE",EDGE,{"disambiguationData":[OSD([sQuery(id+"F4.wireOp",EDGE,"E6")])],"isStart":true});
            var Q447;
            Q447=makeQuery(id+"F5.opExtrude","CAP_EDGE",EDGE,{"disambiguationData":[OSD([sQuery(id+"F4.wireOp",EDGE,"E6")])],"isStart":true});
            var Q448;
            Q448=makeQuery(id+"F5.opExtrude","CAP_EDGE",EDGE,{"disambiguationData":[OSD([sQuery(id+"F4.wireOp",EDGE,"E6")])],"isStart":true});
            var Q449;
            Q449=makeQuery(id+"F5.opExtrude","CAP_EDGE",EDGE,{"disambiguationData":[OSD([sQuery(id+"F4.wireOp",EDGE,"E6")])],"isStart":true});
            var Q450;
            Q450=makeQuery(id+"F5.opExtrude","CAP_EDGE",EDGE,{"disambiguationData":[OSD([sQuery(id+"F4.wireOp",EDGE,"E6")])],"isStart":true});
            var Q451;
            Q451=makeQuery(id+"F5.opExtrude","CAP_EDGE",EDGE,{"disambiguationData":[OSD([sQuery(id+"F4.wireOp",EDGE,"E6")])],"isStart":true});
            var Q452;
            Q452=makeQuery(id+"F5.opExtrude","CAP_EDGE",EDGE,{"disambiguationData":[OSD([sQuery(id+"F4.wireOp",EDGE,"E6")])],"isStart":true});
            var Q453;
            Q453=makeQuery(id+"F5.opExtrude","CAP_EDGE",EDGE,{"disambiguationData":[OSD([sQuery(id+"F4.wireOp",EDGE,"E6")])],"isStart":true});
            var Q454;
            Q454=makeQuery(id+"F5.opExtrude","CAP_EDGE",EDGE,{"disambiguationData":[OSD([sQuery(id+"F4.wireOp",EDGE,"E6")])],"isStart":true});
            var Q455;
            Q455=makeQuery(id+"F5.opExtrude","CAP_EDGE",EDGE,{"disambiguationData":[OSD([sQuery(id+"F4.wireOp",EDGE,"E6")])],"isStart":true});
            var Q456;
            Q456=makeQuery(id+"F5.opExtrude","CAP_EDGE",EDGE,{"disambiguationData":[OSD([sQuery(id+"F4.wireOp",EDGE,"E6")])],"isStart":true});
            var Q457;
            Q457=makeQuery(id+"F5.opExtrude","CAP_EDGE",EDGE,{"disambiguationData":[OSD([sQuery(id+"F4.wireOp",EDGE,"E6")])],"isStart":true});
            var Q458;
            Q458=makeQuery(id+"F5.opExtrude","CAP_EDGE",EDGE,{"disambiguationData":[OSD([sQuery(id+"F4.wireOp",EDGE,"E6")])],"isStart":true});
            var Q459;
            Q459=makeQuery(id+"F5.opExtrude","CAP_EDGE",EDGE,{"disambiguationData":[OSD([sQuery(id+"F4.wireOp",EDGE,"E6")])],"isStart":true});
            var Q460;
            Q460=makeQuery(id+"F5.opExtrude","CAP_EDGE",EDGE,{"disambiguationData":[OSD([sQuery(id+"F4.wireOp",EDGE,"E6")])],"isStart":true});
            var Q461;
            Q461=makeQuery(id+"F5.opExtrude","CAP_EDGE",EDGE,{"disambiguationData":[OSD([sQuery(id+"F4.wireOp",EDGE,"E6")])],"isStart":true});
            var Q462;
            Q462=makeQuery(id+"F5.opExtrude","CAP_EDGE",EDGE,{"disambiguationData":[OSD([sQuery(id+"F4.wireOp",EDGE,"E6")])],"isStart":true});
            var Q463;
            Q463=makeQuery(id+"F5.opExtrude","CAP_EDGE",EDGE,{"disambiguationData":[OSD([sQuery(id+"F4.wireOp",EDGE,"E6")])],"isStart":true});
            var Q464;
            Q464=makeQuery(id+"F5.opExtrude","CAP_EDGE",EDGE,{"disambiguationData":[OSD([sQuery(id+"F4.wireOp",EDGE,"E6")])],"isStart":true});
            var Q465;
            Q465=makeQuery(id+"F5.opExtrude","CAP_EDGE",EDGE,{"disambiguationData":[OSD([sQuery(id+"F4.wireOp",EDGE,"E6")])],"isStart":true});
            var Q466;
            Q466=makeQuery(id+"F5.opExtrude","CAP_EDGE",EDGE,{"disambiguationData":[OSD([sQuery(id+"F4.wireOp",EDGE,"E6")])],"isStart":true});
            var Q467;
            Q467=makeQuery(id+"F5.opExtrude","CAP_EDGE",EDGE,{"disambiguationData":[OSD([sQuery(id+"F4.wireOp",EDGE,"E6")])],"isStart":true});
            var Q468;
            Q468=makeQuery(id+"F5.opExtrude","CAP_EDGE",EDGE,{"disambiguationData":[OSD([sQuery(id+"F4.wireOp",EDGE,"E6")])],"isStart":true});
            var Q469;
            Q469=makeQuery(id+"F5.opExtrude","CAP_EDGE",EDGE,{"disambiguationData":[OSD([sQuery(id+"F4.wireOp",EDGE,"E6")])],"isStart":true});
            var Q470;
            Q470=makeQuery(id+"F5.opExtrude","CAP_EDGE",EDGE,{"disambiguationData":[OSD([sQuery(id+"F4.wireOp",EDGE,"E6")])],"isStart":true});
            var Q471;
            Q471=makeQuery(id+"F5.opExtrude","CAP_EDGE",EDGE,{"disambiguationData":[OSD([sQuery(id+"F4.wireOp",EDGE,"E6")])],"isStart":true});
            var Q472;
            Q472=makeQuery(id+"F5.opExtrude","CAP_EDGE",EDGE,{"disambiguationData":[OSD([sQuery(id+"F4.wireOp",EDGE,"E6")])],"isStart":true});
            var Q473;
            Q473=makeQuery(id+"F5.opExtrude","CAP_EDGE",EDGE,{"disambiguationData":[OSD([sQuery(id+"F4.wireOp",EDGE,"E6")])],"isStart":true});
            var Q474;
            Q474=makeQuery(id+"F5.opExtrude","CAP_EDGE",EDGE,{"disambiguationData":[OSD([sQuery(id+"F4.wireOp",EDGE,"E6")])],"isStart":true});
            var Q475;
            Q475=makeQuery(id+"F5.opExtrude","CAP_EDGE",EDGE,{"disambiguationData":[OSD([sQuery(id+"F4.wireOp",EDGE,"E6")])],"isStart":true});
            var Q476;
            Q476=makeQuery(id+"F5.opExtrude","CAP_EDGE",EDGE,{"disambiguationData":[OSD([sQuery(id+"F4.wireOp",EDGE,"E6")])],"isStart":true});
            var Q477;
            Q477=makeQuery(id+"F5.opExtrude","CAP_EDGE",EDGE,{"disambiguationData":[OSD([sQuery(id+"F4.wireOp",EDGE,"E6")])],"isStart":true});
            var Q478;
            Q478=makeQuery(id+"F5.opExtrude","CAP_EDGE",EDGE,{"disambiguationData":[OSD([sQuery(id+"F4.wireOp",EDGE,"E6")])],"isStart":true});
            var Q479;
            Q479=makeQuery(id+"F5.opExtrude","CAP_EDGE",EDGE,{"disambiguationData":[OSD([sQuery(id+"F4.wireOp",EDGE,"E6")])],"isStart":true});
            var Q480;
            Q480=makeQuery(id+"F5.opExtrude","CAP_EDGE",EDGE,{"disambiguationData":[OSD([sQuery(id+"F4.wireOp",EDGE,"E6")])],"isStart":true});
            var Q481;
            Q481=makeQuery(id+"F5.opExtrude","CAP_EDGE",EDGE,{"disambiguationData":[OSD([sQuery(id+"F4.wireOp",EDGE,"E6")])],"isStart":true});
            var Q482;
            Q482=makeQuery(id+"F5.opExtrude","CAP_EDGE",EDGE,{"disambiguationData":[OSD([sQuery(id+"F4.wireOp",EDGE,"E6")])],"isStart":true});
            var Q483;
            Q483=makeQuery(id+"F5.opExtrude","CAP_EDGE",EDGE,{"disambiguationData":[OSD([sQuery(id+"F4.wireOp",EDGE,"E6")])],"isStart":true});
            var Q484;
            Q484=makeQuery(id+"F5.opExtrude","CAP_EDGE",EDGE,{"disambiguationData":[OSD([sQuery(id+"F4.wireOp",EDGE,"E6")])],"isStart":true});
            var Q485;
            Q485=makeQuery(id+"F5.opExtrude","CAP_EDGE",EDGE,{"disambiguationData":[OSD([sQuery(id+"F4.wireOp",EDGE,"E6")])],"isStart":true});
            var Q486;
            Q486=makeQuery(id+"F5.opExtrude","CAP_EDGE",EDGE,{"disambiguationData":[OSD([sQuery(id+"F4.wireOp",EDGE,"E6")])],"isStart":true});
            var Q487;
            Q487=makeQuery(id+"F5.opExtrude","CAP_EDGE",EDGE,{"disambiguationData":[OSD([sQuery(id+"F4.wireOp",EDGE,"E6")])],"isStart":true});
            var Q488;
            Q488=makeQuery(id+"F5.opExtrude","CAP_EDGE",EDGE,{"disambiguationData":[OSD([sQuery(id+"F4.wireOp",EDGE,"E6")])],"isStart":true});
            var Q489;
            Q489=makeQuery(id+"F5.opExtrude","CAP_EDGE",EDGE,{"disambiguationData":[OSD([sQuery(id+"F4.wireOp",EDGE,"E6")])],"isStart":true});
            var Q490;
            Q490=makeQuery(id+"F5.opExtrude","CAP_EDGE",EDGE,{"disambiguationData":[OSD([sQuery(id+"F4.wireOp",EDGE,"E6")])],"isStart":true});
            var Q491;
            Q491=makeQuery(id+"F5.opExtrude","CAP_EDGE",EDGE,{"disambiguationData":[OSD([sQuery(id+"F4.wireOp",EDGE,"E6")])],"isStart":true});
            var Q492;
            Q492=makeQuery(id+"F5.opExtrude","CAP_EDGE",EDGE,{"disambiguationData":[OSD([sQuery(id+"F4.wireOp",EDGE,"E6")])],"isStart":true});
            var Q493;
            Q493=makeQuery(id+"F5.opExtrude","CAP_EDGE",EDGE,{"disambiguationData":[OSD([sQuery(id+"F4.wireOp",EDGE,"E6")])],"isStart":true});
            var Q494;
            Q494=makeQuery(id+"F5.opExtrude","CAP_EDGE",EDGE,{"disambiguationData":[OSD([sQuery(id+"F4.wireOp",EDGE,"E6")])],"isStart":true});
            var Q495;
            Q495=makeQuery(id+"F5.opExtrude","CAP_EDGE",EDGE,{"disambiguationData":[OSD([sQuery(id+"F4.wireOp",EDGE,"E6")])],"isStart":true});
            var Q496;
            Q496=makeQuery(id+"F5.opExtrude","CAP_EDGE",EDGE,{"disambiguationData":[OSD([sQuery(id+"F4.wireOp",EDGE,"E6")])],"isStart":true});
            var Q497;
            Q497=makeQuery(id+"F5.opExtrude","CAP_EDGE",EDGE,{"disambiguationData":[OSD([sQuery(id+"F4.wireOp",EDGE,"E6")])],"isStart":true});
            var Q498;
            Q498=makeQuery(id+"F5.opExtrude","CAP_EDGE",EDGE,{"disambiguationData":[OSD([sQuery(id+"F4.wireOp",EDGE,"E6")])],"isStart":true});
            var Q499;
            Q499=makeQuery(id+"F5.opExtrude","CAP_EDGE",EDGE,{"disambiguationData":[OSD([sQuery(id+"F4.wireOp",EDGE,"E6")])],"isStart":true});
            var Q500;
            Q500=makeQuery(id+"F5.opExtrude","CAP_EDGE",EDGE,{"disambiguationData":[OSD([sQuery(id+"F4.wireOp",EDGE,"E6")])],"isStart":true});
            var Q501;
            Q501=makeQuery(id+"F5.opExtrude","CAP_EDGE",EDGE,{"disambiguationData":[OSD([sQuery(id+"F4.wireOp",EDGE,"E6")])],"isStart":true});
            var Q502;
            Q502=makeQuery(id+"F5.opExtrude","CAP_EDGE",EDGE,{"disambiguationData":[OSD([sQuery(id+"F4.wireOp",EDGE,"E6")])],"isStart":true});
            var Q503;
            Q503=makeQuery(id+"F5.opExtrude","CAP_EDGE",EDGE,{"disambiguationData":[OSD([sQuery(id+"F4.wireOp",EDGE,"E6")])],"isStart":true});
            var Q504;
            Q504=makeQuery(id+"F5.opExtrude","CAP_EDGE",EDGE,{"disambiguationData":[OSD([sQuery(id+"F4.wireOp",EDGE,"E6")])],"isStart":true});
            var Q505;
            Q505=makeQuery(id+"F5.opExtrude","CAP_EDGE",EDGE,{"disambiguationData":[OSD([sQuery(id+"F4.wireOp",EDGE,"E6")])],"isStart":true});
            var Q506;
            Q506=makeQuery(id+"F5.opExtrude","CAP_EDGE",EDGE,{"disambiguationData":[OSD([sQuery(id+"F4.wireOp",EDGE,"E6")])],"isStart":true});
            var Q507;
            Q507=makeQuery(id+"F5.opExtrude","CAP_EDGE",EDGE,{"disambiguationData":[OSD([sQuery(id+"F4.wireOp",EDGE,"E6")])],"isStart":true});
            var Q508;
            Q508=makeQuery(id+"F5.opExtrude","CAP_EDGE",EDGE,{"disambiguationData":[OSD([sQuery(id+"F4.wireOp",EDGE,"E6")])],"isStart":true});
            var Q509;
            Q509=makeQuery(id+"F5.opExtrude","CAP_EDGE",EDGE,{"disambiguationData":[OSD([sQuery(id+"F4.wireOp",EDGE,"E6")])],"isStart":true});
            var Q510;
            Q510=makeQuery(id+"F5.opExtrude","CAP_EDGE",EDGE,{"disambiguationData":[OSD([sQuery(id+"F4.wireOp",EDGE,"E6")])],"isStart":true});
            var Q511;
            Q511=makeQuery(id+"F5.opExtrude","CAP_EDGE",EDGE,{"disambiguationData":[OSD([sQuery(id+"F4.wireOp",EDGE,"E6")])],"isStart":true});
            var Q512;
            Q512=makeQuery(id+"F5.opExtrude","CAP_EDGE",EDGE,{"disambiguationData":[OSD([sQuery(id+"F4.wireOp",EDGE,"E6")])],"isStart":true});
            var Q513;
            Q513=makeQuery(id+"F5.opExtrude","CAP_EDGE",EDGE,{"disambiguationData":[OSD([sQuery(id+"F4.wireOp",EDGE,"E6")])],"isStart":true});
            var Q514;
            Q514=makeQuery(id+"F5.opExtrude","CAP_EDGE",EDGE,{"disambiguationData":[OSD([sQuery(id+"F4.wireOp",EDGE,"E6")])],"isStart":true});
            var Q515;
            Q515=makeQuery(id+"F5.opExtrude","CAP_EDGE",EDGE,{"disambiguationData":[OSD([sQuery(id+"F4.wireOp",EDGE,"E6")])],"isStart":true});
            var Q516;
            Q516=makeQuery(id+"F5.opExtrude","CAP_EDGE",EDGE,{"disambiguationData":[OSD([sQuery(id+"F4.wireOp",EDGE,"E6")])],"isStart":true});
            var Q517;
            Q517=makeQuery(id+"F5.opExtrude","CAP_EDGE",EDGE,{"disambiguationData":[OSD([sQuery(id+"F4.wireOp",EDGE,"E6")])],"isStart":true});
            var Q518;
            Q518=makeQuery(id+"F5.opExtrude","CAP_EDGE",EDGE,{"disambiguationData":[OSD([sQuery(id+"F4.wireOp",EDGE,"E6")])],"isStart":true});
            var Q519;
            Q519=makeQuery(id+"F5.opExtrude","CAP_EDGE",EDGE,{"disambiguationData":[OSD([sQuery(id+"F4.wireOp",EDGE,"E6")])],"isStart":true});
            var Q520;
            Q520=makeQuery(id+"F5.opExtrude","CAP_EDGE",EDGE,{"disambiguationData":[OSD([sQuery(id+"F4.wireOp",EDGE,"E6")])],"isStart":true});
            var Q521;
            Q521=makeQuery(id+"F5.opExtrude","CAP_EDGE",EDGE,{"disambiguationData":[OSD([sQuery(id+"F4.wireOp",EDGE,"E6")])],"isStart":true});
            var Q522;
            Q522=makeQuery(id+"F5.opExtrude","CAP_EDGE",EDGE,{"disambiguationData":[OSD([sQuery(id+"F4.wireOp",EDGE,"E6")])],"isStart":true});
            var Q523;
            Q523=makeQuery(id+"F5.opExtrude","CAP_EDGE",EDGE,{"disambiguationData":[OSD([sQuery(id+"F4.wireOp",EDGE,"E6")])],"isStart":true});
            var Q524;
            Q524=makeQuery(id+"F5.opExtrude","CAP_EDGE",EDGE,{"disambiguationData":[OSD([sQuery(id+"F4.wireOp",EDGE,"E6")])],"isStart":true});
            var Q525;
            Q525=makeQuery(id+"F5.opExtrude","CAP_EDGE",EDGE,{"disambiguationData":[OSD([sQuery(id+"F4.wireOp",EDGE,"E6")])],"isStart":true});
            var Q526;
            Q526=makeQuery(id+"F5.opExtrude","CAP_EDGE",EDGE,{"disambiguationData":[OSD([sQuery(id+"F4.wireOp",EDGE,"E6")])],"isStart":true});
            var Q527;
            Q527=makeQuery(id+"F5.opExtrude","CAP_EDGE",EDGE,{"disambiguationData":[OSD([sQuery(id+"F4.wireOp",EDGE,"E6")])],"isStart":true});
            var Q528;
            Q528=makeQuery(id+"F5.opExtrude","CAP_EDGE",EDGE,{"disambiguationData":[OSD([sQuery(id+"F4.wireOp",EDGE,"E6")])],"isStart":true});
            var Q529;
            Q529=makeQuery(id+"F5.opExtrude","CAP_EDGE",EDGE,{"disambiguationData":[OSD([sQuery(id+"F4.wireOp",EDGE,"E6")])],"isStart":true});
            var Q530;
            Q530=makeQuery(id+"F5.opExtrude","CAP_EDGE",EDGE,{"disambiguationData":[OSD([sQuery(id+"F4.wireOp",EDGE,"E6")])],"isStart":true});
            var Q531;
            Q531=makeQuery(id+"F5.opExtrude","CAP_EDGE",EDGE,{"disambiguationData":[OSD([sQuery(id+"F4.wireOp",EDGE,"E6")])],"isStart":true});
            var Q532;
            Q532=makeQuery(id+"F5.opExtrude","CAP_EDGE",EDGE,{"disambiguationData":[OSD([sQuery(id+"F4.wireOp",EDGE,"E6")])],"isStart":true});
            var Q533;
            Q533=makeQuery(id+"F5.opExtrude","CAP_EDGE",EDGE,{"disambiguationData":[OSD([sQuery(id+"F4.wireOp",EDGE,"E6")])],"isStart":true});
            var Q534;
            Q534=makeQuery(id+"F5.opExtrude","CAP_EDGE",EDGE,{"disambiguationData":[OSD([sQuery(id+"F4.wireOp",EDGE,"E6")])],"isStart":true});
            var Q535;
            Q535=makeQuery(id+"F5.opExtrude","CAP_EDGE",EDGE,{"disambiguationData":[OSD([sQuery(id+"F4.wireOp",EDGE,"E6")])],"isStart":true});
            var Q536;
            Q536=makeQuery(id+"F5.opExtrude","CAP_EDGE",EDGE,{"disambiguationData":[OSD([sQuery(id+"F4.wireOp",EDGE,"E6")])],"isStart":true});
            var Q537;
            Q537=makeQuery(id+"F5.opExtrude","CAP_EDGE",EDGE,{"disambiguationData":[OSD([sQuery(id+"F4.wireOp",EDGE,"E6")])],"isStart":true});
            var Q538;
            Q538=makeQuery(id+"F5.opExtrude","CAP_EDGE",EDGE,{"disambiguationData":[OSD([sQuery(id+"F4.wireOp",EDGE,"E6")])],"isStart":true});
            var Q539;
            Q539=makeQuery(id+"F5.opExtrude","CAP_EDGE",EDGE,{"disambiguationData":[OSD([sQuery(id+"F4.wireOp",EDGE,"E6")])],"isStart":true});
            var Q540;
            Q540=makeQuery(id+"F5.opExtrude","CAP_EDGE",EDGE,{"disambiguationData":[OSD([sQuery(id+"F4.wireOp",EDGE,"E6")])],"isStart":true});
            var Q541;
            Q541=makeQuery(id+"F5.opExtrude","CAP_EDGE",EDGE,{"disambiguationData":[OSD([sQuery(id+"F4.wireOp",EDGE,"E6")])],"isStart":true});
            var Q542;
            Q542=makeQuery(id+"F5.opExtrude","CAP_EDGE",EDGE,{"disambiguationData":[OSD([sQuery(id+"F4.wireOp",EDGE,"E6")])],"isStart":true});
            var Q543;
            Q543=makeQuery(id+"F5.opExtrude","CAP_EDGE",EDGE,{"disambiguationData":[OSD([sQuery(id+"F4.wireOp",EDGE,"E6")])],"isStart":true});
            var Q544;
            Q544=makeQuery(id+"F5.opExtrude","CAP_EDGE",EDGE,{"disambiguationData":[OSD([sQuery(id+"F4.wireOp",EDGE,"E6")])],"isStart":true});
            var Q545;
            Q545=makeQuery(id+"F5.opExtrude","CAP_EDGE",EDGE,{"disambiguationData":[OSD([sQuery(id+"F4.wireOp",EDGE,"E6")])],"isStart":true});
            var Q546;
            Q546=makeQuery(id+"F5.opExtrude","CAP_EDGE",EDGE,{"disambiguationData":[OSD([sQuery(id+"F4.wireOp",EDGE,"E6")])],"isStart":true});
            var Q547;
            Q547=makeQuery(id+"F5.opExtrude","CAP_EDGE",EDGE,{"disambiguationData":[OSD([sQuery(id+"F4.wireOp",EDGE,"E6")])],"isStart":true});
            var Q548;
            Q548=makeQuery(id+"F5.opExtrude","CAP_EDGE",EDGE,{"disambiguationData":[OSD([sQuery(id+"F4.wireOp",EDGE,"E6")])],"isStart":true});
            var Q549;
            Q549=makeQuery(id+"F5.opExtrude","CAP_EDGE",EDGE,{"disambiguationData":[OSD([sQuery(id+"F4.wireOp",EDGE,"E6")])],"isStart":true});
            var Q550;
            Q550=makeQuery(id+"F5.opExtrude","CAP_EDGE",EDGE,{"disambiguationData":[OSD([sQuery(id+"F4.wireOp",EDGE,"E6")])],"isStart":true});
            var Q551;
            Q551=makeQuery(id+"F5.opExtrude","CAP_EDGE",EDGE,{"disambiguationData":[OSD([sQuery(id+"F4.wireOp",EDGE,"E6")])],"isStart":true});
            var Q552;
            Q552=makeQuery(id+"F5.opExtrude","CAP_EDGE",EDGE,{"disambiguationData":[OSD([sQuery(id+"F4.wireOp",EDGE,"E6")])],"isStart":true});
            var Q553;
            Q553=makeQuery(id+"F5.opExtrude","CAP_EDGE",EDGE,{"disambiguationData":[OSD([sQuery(id+"F4.wireOp",EDGE,"E6")])],"isStart":true});
            var Q554;
            Q554=makeQuery(id+"F5.opExtrude","CAP_EDGE",EDGE,{"disambiguationData":[OSD([sQuery(id+"F4.wireOp",EDGE,"E6")])],"isStart":true});
            var Q555;
            Q555=makeQuery(id+"F5.opExtrude","CAP_EDGE",EDGE,{"disambiguationData":[OSD([sQuery(id+"F4.wireOp",EDGE,"E6")])],"isStart":true});
            var Q556;
            Q556=makeQuery(id+"F5.opExtrude","CAP_EDGE",EDGE,{"disambiguationData":[OSD([sQuery(id+"F4.wireOp",EDGE,"E6")])],"isStart":true});
            var Q557;
            Q557=makeQuery(id+"F5.opExtrude","CAP_EDGE",EDGE,{"disambiguationData":[OSD([sQuery(id+"F4.wireOp",EDGE,"E6")])],"isStart":true});
            var Q558;
            Q558=makeQuery(id+"F5.opExtrude","CAP_EDGE",EDGE,{"disambiguationData":[OSD([sQuery(id+"F4.wireOp",EDGE,"E6")])],"isStart":false});
            var Q559;
            Q559=makeQuery(id+"F5.opExtrude","CAP_EDGE",EDGE,{"disambiguationData":[OSD([sQuery(id+"F4.wireOp",EDGE,"E6")])],"isStart":false});
            var Q560;
            Q560=makeQuery(id+"F5.opExtrude","CAP_EDGE",EDGE,{"disambiguationData":[OSD([sQuery(id+"F4.wireOp",EDGE,"E6")])],"isStart":false});
            var Q561;
            Q561=makeQuery(id+"F5.opExtrude","CAP_EDGE",EDGE,{"disambiguationData":[OSD([sQuery(id+"F4.wireOp",EDGE,"E6")])],"isStart":false});
            var Q562;
            Q562=makeQuery(id+"F5.opExtrude","CAP_EDGE",EDGE,{"disambiguationData":[OSD([sQuery(id+"F4.wireOp",EDGE,"E6")])],"isStart":false});
            var Q563;
            Q563=makeQuery(id+"F5.opExtrude","CAP_EDGE",EDGE,{"disambiguationData":[OSD([sQuery(id+"F4.wireOp",EDGE,"E6")])],"isStart":false});
            var Q564;
            Q564=makeQuery(id+"F5.opExtrude","CAP_EDGE",EDGE,{"disambiguationData":[OSD([sQuery(id+"F4.wireOp",EDGE,"E6")])],"isStart":false});
            var Q565;
            Q565=makeQuery(id+"F5.opExtrude","CAP_EDGE",EDGE,{"disambiguationData":[OSD([sQuery(id+"F4.wireOp",EDGE,"E6")])],"isStart":false});
            var Q566;
            Q566=makeQuery(id+"F5.opExtrude","CAP_EDGE",EDGE,{"disambiguationData":[OSD([sQuery(id+"F4.wireOp",EDGE,"E6")])],"isStart":false});
            var Q567;
            Q567=makeQuery(id+"F5.opExtrude","CAP_EDGE",EDGE,{"disambiguationData":[OSD([sQuery(id+"F4.wireOp",EDGE,"E6")])],"isStart":false});
            var Q568;
            Q568=makeQuery(id+"F5.opExtrude","CAP_EDGE",EDGE,{"disambiguationData":[OSD([sQuery(id+"F4.wireOp",EDGE,"E6")])],"isStart":false});
            var Q569;
            Q569=makeQuery(id+"F5.opExtrude","CAP_EDGE",EDGE,{"disambiguationData":[OSD([sQuery(id+"F4.wireOp",EDGE,"E6")])],"isStart":false});
            var Q570;
            Q570=makeQuery(id+"F5.opExtrude","CAP_EDGE",EDGE,{"disambiguationData":[OSD([sQuery(id+"F4.wireOp",EDGE,"E6")])],"isStart":false});
            var Q571;
            Q571=makeQuery(id+"F5.opExtrude","CAP_EDGE",EDGE,{"disambiguationData":[OSD([sQuery(id+"F4.wireOp",EDGE,"E6")])],"isStart":false});
            var Q572;
            Q572=makeQuery(id+"F5.opExtrude","CAP_EDGE",EDGE,{"disambiguationData":[OSD([sQuery(id+"F4.wireOp",EDGE,"E6")])],"isStart":false});
            var Q573;
            Q573=makeQuery(id+"F5.opExtrude","CAP_EDGE",EDGE,{"disambiguationData":[OSD([sQuery(id+"F4.wireOp",EDGE,"E6")])],"isStart":false});
            var Q574;
            Q574=makeQuery(id+"F5.opExtrude","CAP_EDGE",EDGE,{"disambiguationData":[OSD([sQuery(id+"F4.wireOp",EDGE,"E6")])],"isStart":false});
            var Q575;
            Q575=makeQuery(id+"F5.opExtrude","CAP_EDGE",EDGE,{"disambiguationData":[OSD([sQuery(id+"F4.wireOp",EDGE,"E6")])],"isStart":false});
            var Q576;
            Q576=makeQuery(id+"F5.opExtrude","CAP_EDGE",EDGE,{"disambiguationData":[OSD([sQuery(id+"F4.wireOp",EDGE,"E6")])],"isStart":false});
            var Q577;
            Q577=makeQuery(id+"F5.opExtrude","CAP_EDGE",EDGE,{"disambiguationData":[OSD([sQuery(id+"F4.wireOp",EDGE,"E6")])],"isStart":false});
            var Q578;
            Q578=makeQuery(id+"F5.opExtrude","CAP_EDGE",EDGE,{"disambiguationData":[OSD([sQuery(id+"F4.wireOp",EDGE,"E6")])],"isStart":false});
            var Q579;
            Q579=makeQuery(id+"F5.opExtrude","CAP_EDGE",EDGE,{"disambiguationData":[OSD([sQuery(id+"F4.wireOp",EDGE,"E6")])],"isStart":false});
            var Q580;
            Q580=makeQuery(id+"F5.opExtrude","CAP_EDGE",EDGE,{"disambiguationData":[OSD([sQuery(id+"F4.wireOp",EDGE,"E6")])],"isStart":false});
            var Q581;
            Q581=makeQuery(id+"F5.opExtrude","CAP_EDGE",EDGE,{"disambiguationData":[OSD([sQuery(id+"F4.wireOp",EDGE,"E6")])],"isStart":false});
            var Q582;
            Q582=makeQuery(id+"F5.opExtrude","CAP_EDGE",EDGE,{"disambiguationData":[OSD([sQuery(id+"F4.wireOp",EDGE,"E6")])],"isStart":false});
            var Q583;
            Q583=makeQuery(id+"F5.opExtrude","CAP_EDGE",EDGE,{"disambiguationData":[OSD([sQuery(id+"F4.wireOp",EDGE,"E6")])],"isStart":false});
            var Q584;
            Q584=makeQuery(id+"F5.opExtrude","CAP_EDGE",EDGE,{"disambiguationData":[OSD([sQuery(id+"F4.wireOp",EDGE,"E6")])],"isStart":false});
            var Q585;
            Q585=makeQuery(id+"F5.opExtrude","CAP_EDGE",EDGE,{"disambiguationData":[OSD([sQuery(id+"F4.wireOp",EDGE,"E6")])],"isStart":false});
            var Q586;
            Q586=makeQuery(id+"F5.opExtrude","CAP_EDGE",EDGE,{"disambiguationData":[OSD([sQuery(id+"F4.wireOp",EDGE,"E6")])],"isStart":false});
            var Q587;
            Q587=makeQuery(id+"F5.opExtrude","CAP_EDGE",EDGE,{"disambiguationData":[OSD([sQuery(id+"F4.wireOp",EDGE,"E6")])],"isStart":false});
            var Q588;
            Q588=makeQuery(id+"F5.opExtrude","CAP_EDGE",EDGE,{"disambiguationData":[OSD([sQuery(id+"F4.wireOp",EDGE,"E6")])],"isStart":false});
            var Q589;
            Q589=makeQuery(id+"F5.opExtrude","CAP_EDGE",EDGE,{"disambiguationData":[OSD([sQuery(id+"F4.wireOp",EDGE,"E6")])],"isStart":false});
            var Q590;
            Q590=makeQuery(id+"F5.opExtrude","CAP_EDGE",EDGE,{"disambiguationData":[OSD([sQuery(id+"F4.wireOp",EDGE,"E6")])],"isStart":false});
            var Q591;
            Q591=makeQuery(id+"F5.opExtrude","CAP_EDGE",EDGE,{"disambiguationData":[OSD([sQuery(id+"F4.wireOp",EDGE,"E6")])],"isStart":false});
            var Q592;
            Q592=makeQuery(id+"F5.opExtrude","CAP_EDGE",EDGE,{"disambiguationData":[OSD([sQuery(id+"F4.wireOp",EDGE,"E6")])],"isStart":false});
            var Q593;
            Q593=makeQuery(id+"F5.opExtrude","CAP_EDGE",EDGE,{"disambiguationData":[OSD([sQuery(id+"F4.wireOp",EDGE,"E6")])],"isStart":false});
            var Q594;
            Q594=makeQuery(id+"F5.opExtrude","CAP_EDGE",EDGE,{"disambiguationData":[OSD([sQuery(id+"F4.wireOp",EDGE,"E6")])],"isStart":false});
            var Q595;
            Q595=makeQuery(id+"F5.opExtrude","CAP_EDGE",EDGE,{"disambiguationData":[OSD([sQuery(id+"F4.wireOp",EDGE,"E6")])],"isStart":false});
            var Q596;
            Q596=makeQuery(id+"F5.opExtrude","CAP_EDGE",EDGE,{"disambiguationData":[OSD([sQuery(id+"F4.wireOp",EDGE,"E6")])],"isStart":false});
            var Q597;
            Q597=makeQuery(id+"F5.opExtrude","CAP_EDGE",EDGE,{"disambiguationData":[OSD([sQuery(id+"F4.wireOp",EDGE,"E6")])],"isStart":false});
            var Q598;
            Q598=makeQuery(id+"F5.opExtrude","CAP_EDGE",EDGE,{"disambiguationData":[OSD([sQuery(id+"F4.wireOp",EDGE,"E6")])],"isStart":false});
            var Q599;
            Q599=makeQuery(id+"F5.opExtrude","CAP_EDGE",EDGE,{"disambiguationData":[OSD([sQuery(id+"F4.wireOp",EDGE,"E6")])],"isStart":false});
            var Q600;
            Q600=makeQuery(id+"F5.opExtrude","CAP_EDGE",EDGE,{"disambiguationData":[OSD([sQuery(id+"F4.wireOp",EDGE,"E6")])],"isStart":false});
            var Q601;
            Q601=makeQuery(id+"F5.opExtrude","CAP_EDGE",EDGE,{"disambiguationData":[OSD([sQuery(id+"F4.wireOp",EDGE,"E6")])],"isStart":false});
            var Q602;
            Q602=makeQuery(id+"F5.opExtrude","CAP_EDGE",EDGE,{"disambiguationData":[OSD([sQuery(id+"F4.wireOp",EDGE,"E6")])],"isStart":false});
            var Q603;
            Q603=makeQuery(id+"F5.opExtrude","CAP_EDGE",EDGE,{"disambiguationData":[OSD([sQuery(id+"F4.wireOp",EDGE,"E6")])],"isStart":false});
            var Q604;
            Q604=makeQuery(id+"F5.opExtrude","CAP_EDGE",EDGE,{"disambiguationData":[OSD([sQuery(id+"F4.wireOp",EDGE,"E6")])],"isStart":false});
            var Q605;
            Q605=makeQuery(id+"F5.opExtrude","CAP_EDGE",EDGE,{"disambiguationData":[OSD([sQuery(id+"F4.wireOp",EDGE,"E6")])],"isStart":false});
            var Q606;
            Q606=makeQuery(id+"F5.opExtrude","CAP_EDGE",EDGE,{"disambiguationData":[OSD([sQuery(id+"F4.wireOp",EDGE,"E6")])],"isStart":false});
            var Q607;
            Q607=makeQuery(id+"F5.opExtrude","CAP_EDGE",EDGE,{"disambiguationData":[OSD([sQuery(id+"F4.wireOp",EDGE,"E6")])],"isStart":false});
            var Q608;
            Q608=makeQuery(id+"F5.opExtrude","CAP_EDGE",EDGE,{"disambiguationData":[OSD([sQuery(id+"F4.wireOp",EDGE,"E6")])],"isStart":false});
            var Q609;
            Q609=makeQuery(id+"F5.opExtrude","CAP_EDGE",EDGE,{"disambiguationData":[OSD([sQuery(id+"F4.wireOp",EDGE,"E6")])],"isStart":false});
            var Q610;
            Q610=makeQuery(id+"F5.opExtrude","CAP_EDGE",EDGE,{"disambiguationData":[OSD([sQuery(id+"F4.wireOp",EDGE,"E6")])],"isStart":false});
            var Q611;
            Q611=makeQuery(id+"F5.opExtrude","CAP_EDGE",EDGE,{"disambiguationData":[OSD([sQuery(id+"F4.wireOp",EDGE,"E6")])],"isStart":false});
            var Q612;
            Q612=makeQuery(id+"F5.opExtrude","CAP_EDGE",EDGE,{"disambiguationData":[OSD([sQuery(id+"F4.wireOp",EDGE,"E6")])],"isStart":false});
            var Q613;
            Q613=makeQuery(id+"F5.opExtrude","CAP_EDGE",EDGE,{"disambiguationData":[OSD([sQuery(id+"F4.wireOp",EDGE,"E6")])],"isStart":false});
            var Q614;
            Q614=makeQuery(id+"F5.opExtrude","CAP_EDGE",EDGE,{"disambiguationData":[OSD([sQuery(id+"F4.wireOp",EDGE,"E6")])],"isStart":false});
            var Q615;
            Q615=makeQuery(id+"F5.opExtrude","CAP_EDGE",EDGE,{"disambiguationData":[OSD([sQuery(id+"F4.wireOp",EDGE,"E6")])],"isStart":false});
            var Q616;
            Q616=makeQuery(id+"F5.opExtrude","CAP_EDGE",EDGE,{"disambiguationData":[OSD([sQuery(id+"F4.wireOp",EDGE,"E6")])],"isStart":false});
            var Q617;
            Q617=makeQuery(id+"F5.opExtrude","CAP_EDGE",EDGE,{"disambiguationData":[OSD([sQuery(id+"F4.wireOp",EDGE,"E6")])],"isStart":false});
            var Q618;
            Q618=makeQuery(id+"F5.opExtrude","CAP_EDGE",EDGE,{"disambiguationData":[OSD([sQuery(id+"F4.wireOp",EDGE,"E6")])],"isStart":false});
            var Q619;
            Q619=makeQuery(id+"F5.opExtrude","CAP_EDGE",EDGE,{"disambiguationData":[OSD([sQuery(id+"F4.wireOp",EDGE,"E6")])],"isStart":false});
            var Q620;
            Q620=makeQuery(id+"F5.opExtrude","CAP_EDGE",EDGE,{"disambiguationData":[OSD([sQuery(id+"F4.wireOp",EDGE,"E6")])],"isStart":false});
            var Q621;
            Q621=makeQuery(id+"F5.opExtrude","CAP_EDGE",EDGE,{"disambiguationData":[OSD([sQuery(id+"F4.wireOp",EDGE,"E6")])],"isStart":false});
            var Q622;
            Q622=makeQuery(id+"F5.opExtrude","CAP_EDGE",EDGE,{"disambiguationData":[OSD([sQuery(id+"F4.wireOp",EDGE,"E6")])],"isStart":false});
            var Q623;
            Q623=makeQuery(id+"F5.opExtrude","CAP_EDGE",EDGE,{"disambiguationData":[OSD([sQuery(id+"F4.wireOp",EDGE,"E6")])],"isStart":false});
            var Q624;
            Q624=makeQuery(id+"F5.opExtrude","CAP_EDGE",EDGE,{"disambiguationData":[OSD([sQuery(id+"F4.wireOp",EDGE,"E6")])],"isStart":false});
            var Q625;
            Q625=makeQuery(id+"F5.opExtrude","CAP_EDGE",EDGE,{"disambiguationData":[OSD([sQuery(id+"F4.wireOp",EDGE,"E6")])],"isStart":false});
            var Q626;
            Q626=makeQuery(id+"F5.opExtrude","CAP_EDGE",EDGE,{"disambiguationData":[OSD([sQuery(id+"F4.wireOp",EDGE,"E6")])],"isStart":false});
            var Q627;
            Q627=makeQuery(id+"F5.opExtrude","CAP_EDGE",EDGE,{"disambiguationData":[OSD([sQuery(id+"F4.wireOp",EDGE,"E6")])],"isStart":false});
            var Q628;
            Q628=makeQuery(id+"F5.opExtrude","CAP_EDGE",EDGE,{"disambiguationData":[OSD([sQuery(id+"F4.wireOp",EDGE,"E6")])],"isStart":false});
            var Q629;
            Q629=makeQuery(id+"F5.opExtrude","CAP_EDGE",EDGE,{"disambiguationData":[OSD([sQuery(id+"F4.wireOp",EDGE,"E6")])],"isStart":false});
            var Q630;
            Q630=makeQuery(id+"F5.opExtrude","CAP_EDGE",EDGE,{"disambiguationData":[OSD([sQuery(id+"F4.wireOp",EDGE,"E6")])],"isStart":false});
            var Q631;
            Q631=makeQuery(id+"F5.opExtrude","CAP_EDGE",EDGE,{"disambiguationData":[OSD([sQuery(id+"F4.wireOp",EDGE,"E6")])],"isStart":false});
            var Q632;
            Q632=makeQuery(id+"F5.opExtrude","CAP_EDGE",EDGE,{"disambiguationData":[OSD([sQuery(id+"F4.wireOp",EDGE,"E6")])],"isStart":false});
            var Q633;
            Q633=makeQuery(id+"F5.opExtrude","CAP_EDGE",EDGE,{"disambiguationData":[OSD([sQuery(id+"F4.wireOp",EDGE,"E6")])],"isStart":false});
            var Q634;
            Q634=makeQuery(id+"F5.opExtrude","CAP_EDGE",EDGE,{"disambiguationData":[OSD([sQuery(id+"F4.wireOp",EDGE,"E6")])],"isStart":false});
            var Q635;
            Q635=makeQuery(id+"F5.opExtrude","CAP_EDGE",EDGE,{"disambiguationData":[OSD([sQuery(id+"F4.wireOp",EDGE,"E6")])],"isStart":false});
            var Q636;
            Q636=makeQuery(id+"F5.opExtrude","CAP_EDGE",EDGE,{"disambiguationData":[OSD([sQuery(id+"F4.wireOp",EDGE,"E6")])],"isStart":false});
            var Q637;
            Q637=makeQuery(id+"F5.opExtrude","CAP_EDGE",EDGE,{"disambiguationData":[OSD([sQuery(id+"F4.wireOp",EDGE,"E6")])],"isStart":false});
            var Q638;
            Q638=makeQuery(id+"F5.opExtrude","CAP_EDGE",EDGE,{"disambiguationData":[OSD([sQuery(id+"F4.wireOp",EDGE,"E6")])],"isStart":false});
            var Q639;
            Q639=makeQuery(id+"F5.opExtrude","CAP_EDGE",EDGE,{"disambiguationData":[OSD([sQuery(id+"F4.wireOp",EDGE,"E6")])],"isStart":false});
            var Q640;
            Q640=makeQuery(id+"F5.opExtrude","CAP_EDGE",EDGE,{"disambiguationData":[OSD([sQuery(id+"F4.wireOp",EDGE,"E6")])],"isStart":false});
            var Q641;
            Q641=makeQuery(id+"F5.opExtrude","CAP_EDGE",EDGE,{"disambiguationData":[OSD([sQuery(id+"F4.wireOp",EDGE,"E6")])],"isStart":false});
            var Q642;
            Q642=makeQuery(id+"F5.opExtrude","CAP_EDGE",EDGE,{"disambiguationData":[OSD([sQuery(id+"F4.wireOp",EDGE,"E6")])],"isStart":false});
            var Q643;
            Q643=makeQuery(id+"F5.opExtrude","CAP_EDGE",EDGE,{"disambiguationData":[OSD([sQuery(id+"F4.wireOp",EDGE,"E6")])],"isStart":false});
            var Q644;
            Q644=makeQuery(id+"F5.opExtrude","CAP_EDGE",EDGE,{"disambiguationData":[OSD([sQuery(id+"F4.wireOp",EDGE,"E6")])],"isStart":false});
            var Q645;
            Q645=makeQuery(id+"F5.opExtrude","CAP_EDGE",EDGE,{"disambiguationData":[OSD([sQuery(id+"F4.wireOp",EDGE,"E6")])],"isStart":false});
            var Q646;
            Q646=makeQuery(id+"F5.opExtrude","CAP_EDGE",EDGE,{"disambiguationData":[OSD([sQuery(id+"F4.wireOp",EDGE,"E6")])],"isStart":false});
            var Q647;
            Q647=makeQuery(id+"F5.opExtrude","CAP_EDGE",EDGE,{"disambiguationData":[OSD([sQuery(id+"F4.wireOp",EDGE,"E6")])],"isStart":false});
            var Q648;
            Q648=makeQuery(id+"F5.opExtrude","CAP_EDGE",EDGE,{"disambiguationData":[OSD([sQuery(id+"F4.wireOp",EDGE,"E6")])],"isStart":false});
            var Q649;
            Q649=makeQuery(id+"F5.opExtrude","CAP_EDGE",EDGE,{"disambiguationData":[OSD([sQuery(id+"F4.wireOp",EDGE,"E6")])],"isStart":false});
            var Q650;
            Q650=makeQuery(id+"F5.opExtrude","CAP_EDGE",EDGE,{"disambiguationData":[OSD([sQuery(id+"F4.wireOp",EDGE,"E6")])],"isStart":false});
            var Q651;
            Q651=makeQuery(id+"F5.opExtrude","CAP_EDGE",EDGE,{"disambiguationData":[OSD([sQuery(id+"F4.wireOp",EDGE,"E6")])],"isStart":false});
            var Q652;
            Q652=makeQuery(id+"F5.opExtrude","CAP_EDGE",EDGE,{"disambiguationData":[OSD([sQuery(id+"F4.wireOp",EDGE,"E6")])],"isStart":false});
            var Q653;
            Q653=makeQuery(id+"F5.opExtrude","CAP_EDGE",EDGE,{"disambiguationData":[OSD([sQuery(id+"F4.wireOp",EDGE,"E6")])],"isStart":false});
            var Q654;
            Q654=makeQuery(id+"F5.opExtrude","CAP_EDGE",EDGE,{"disambiguationData":[OSD([sQuery(id+"F4.wireOp",EDGE,"E6")])],"isStart":false});
            var Q655;
            Q655=makeQuery(id+"F5.opExtrude","CAP_EDGE",EDGE,{"disambiguationData":[OSD([sQuery(id+"F4.wireOp",EDGE,"E6")])],"isStart":false});
            var Q656;
            Q656=makeQuery(id+"F5.opExtrude","CAP_EDGE",EDGE,{"disambiguationData":[OSD([sQuery(id+"F4.wireOp",EDGE,"E6")])],"isStart":false});
            var Q657;
            Q657=makeQuery(id+"F5.opExtrude","CAP_EDGE",EDGE,{"disambiguationData":[OSD([sQuery(id+"F4.wireOp",EDGE,"E6")])],"isStart":false});
            var Q658;
            Q658=makeQuery(id+"F5.opExtrude","CAP_EDGE",EDGE,{"disambiguationData":[OSD([sQuery(id+"F4.wireOp",EDGE,"E6")])],"isStart":false});
            var Q659;
            Q659=makeQuery(id+"F5.opExtrude","CAP_EDGE",EDGE,{"disambiguationData":[OSD([sQuery(id+"F4.wireOp",EDGE,"E6")])],"isStart":false});
            var Q660;
            Q660=makeQuery(id+"F5.opExtrude","CAP_EDGE",EDGE,{"disambiguationData":[OSD([sQuery(id+"F4.wireOp",EDGE,"E6")])],"isStart":false});
            var Q661;
            Q661=makeQuery(id+"F5.opExtrude","CAP_EDGE",EDGE,{"disambiguationData":[OSD([sQuery(id+"F4.wireOp",EDGE,"E6")])],"isStart":false});
            var Q662;
            Q662=makeQuery(id+"F5.opExtrude","CAP_EDGE",EDGE,{"disambiguationData":[OSD([sQuery(id+"F4.wireOp",EDGE,"E6")])],"isStart":false});
            var Q663;
            Q663=makeQuery(id+"F5.opExtrude","CAP_EDGE",EDGE,{"disambiguationData":[OSD([sQuery(id+"F4.wireOp",EDGE,"E6")])],"isStart":false});
            var Q664;
            Q664=makeQuery(id+"F5.opExtrude","CAP_EDGE",EDGE,{"disambiguationData":[OSD([sQuery(id+"F4.wireOp",EDGE,"E6")])],"isStart":false});
            var Q665;
            Q665=makeQuery(id+"F5.opExtrude","CAP_EDGE",EDGE,{"disambiguationData":[OSD([sQuery(id+"F4.wireOp",EDGE,"E6")])],"isStart":false});
            var Q666;
            Q666=makeQuery(id+"F5.opExtrude","CAP_EDGE",EDGE,{"disambiguationData":[OSD([sQuery(id+"F4.wireOp",EDGE,"E6")])],"isStart":false});
            var Q667;
            Q667=makeQuery(id+"F5.opExtrude","CAP_EDGE",EDGE,{"disambiguationData":[OSD([sQuery(id+"F4.wireOp",EDGE,"E6")])],"isStart":false});
            var Q668;
            Q668=makeQuery(id+"F5.opExtrude","CAP_EDGE",EDGE,{"disambiguationData":[OSD([sQuery(id+"F4.wireOp",EDGE,"E6")])],"isStart":false});
            var Q669;
            Q669=makeQuery(id+"F5.opExtrude","CAP_EDGE",EDGE,{"disambiguationData":[OSD([sQuery(id+"F4.wireOp",EDGE,"E6")])],"isStart":false});
            var Q670;
            Q670=makeQuery(id+"F5.opExtrude","CAP_EDGE",EDGE,{"disambiguationData":[OSD([sQuery(id+"F4.wireOp",EDGE,"E6")])],"isStart":false});
            var Q671;
            Q671=makeQuery(id+"F5.opExtrude","CAP_EDGE",EDGE,{"disambiguationData":[OSD([sQuery(id+"F4.wireOp",EDGE,"E6")])],"isStart":false});
            var Q672;
            Q672=makeQuery(id+"F5.opExtrude","CAP_EDGE",EDGE,{"disambiguationData":[OSD([sQuery(id+"F4.wireOp",EDGE,"E6")])],"isStart":false});
            var Q673;
            Q673=makeQuery(id+"F5.opExtrude","CAP_EDGE",EDGE,{"disambiguationData":[OSD([sQuery(id+"F4.wireOp",EDGE,"E6")])],"isStart":false});
            var Q674;
            Q674=makeQuery(id+"F5.opExtrude","CAP_EDGE",EDGE,{"disambiguationData":[OSD([sQuery(id+"F4.wireOp",EDGE,"E6")])],"isStart":false});
            var Q675;
            Q675=makeQuery(id+"F5.opExtrude","CAP_EDGE",EDGE,{"disambiguationData":[OSD([sQuery(id+"F4.wireOp",EDGE,"E6")])],"isStart":false});
            var Q676;
            Q676=makeQuery(id+"F5.opExtrude","CAP_EDGE",EDGE,{"disambiguationData":[OSD([sQuery(id+"F4.wireOp",EDGE,"E6")])],"isStart":false});
            var Q677;
            Q677=makeQuery(id+"F5.opExtrude","CAP_EDGE",EDGE,{"disambiguationData":[OSD([sQuery(id+"F4.wireOp",EDGE,"E6")])],"isStart":false});
            var Q678;
            Q678=makeQuery(id+"F5.opExtrude","CAP_EDGE",EDGE,{"disambiguationData":[OSD([sQuery(id+"F4.wireOp",EDGE,"E6")])],"isStart":false});
            var Q679;
            Q679=makeQuery(id+"F5.opExtrude","CAP_EDGE",EDGE,{"disambiguationData":[OSD([sQuery(id+"F4.wireOp",EDGE,"E6")])],"isStart":false});
            var Q680;
            Q680=makeQuery(id+"F5.opExtrude","CAP_EDGE",EDGE,{"disambiguationData":[OSD([sQuery(id+"F4.wireOp",EDGE,"E6")])],"isStart":false});
            var Q681;
            Q681=makeQuery(id+"F5.opExtrude","CAP_EDGE",EDGE,{"disambiguationData":[OSD([sQuery(id+"F4.wireOp",EDGE,"E6")])],"isStart":false});
            var Q682;
            Q682=makeQuery(id+"F5.opExtrude","CAP_EDGE",EDGE,{"disambiguationData":[OSD([sQuery(id+"F4.wireOp",EDGE,"E6")])],"isStart":true});
            var Q683;
            Q683=makeQuery(id+"F5.opExtrude","CAP_EDGE",EDGE,{"disambiguationData":[OSD([sQuery(id+"F4.wireOp",EDGE,"E6")])],"isStart":true});
            var Q684;
            Q684=makeQuery(id+"F5.opExtrude","CAP_EDGE",EDGE,{"disambiguationData":[OSD([sQuery(id+"F4.wireOp",EDGE,"E6")])],"isStart":true});
            var Q685;
            Q685=makeQuery(id+"F5.opExtrude","CAP_EDGE",EDGE,{"disambiguationData":[OSD([sQuery(id+"F4.wireOp",EDGE,"E6")])],"isStart":true});
            var Q686;
            Q686=makeQuery(id+"F5.opExtrude","CAP_EDGE",EDGE,{"disambiguationData":[OSD([sQuery(id+"F4.wireOp",EDGE,"E6")])],"isStart":true});
            var Q687;
            Q687=makeQuery(id+"F5.opExtrude","CAP_EDGE",EDGE,{"disambiguationData":[OSD([sQuery(id+"F4.wireOp",EDGE,"E6")])],"isStart":true});
            var Q688;
            Q688=makeQuery(id+"F5.opExtrude","CAP_EDGE",EDGE,{"disambiguationData":[OSD([sQuery(id+"F4.wireOp",EDGE,"E6")])],"isStart":true});
            var Q689;
            Q689=makeQuery(id+"F5.opExtrude","CAP_EDGE",EDGE,{"disambiguationData":[OSD([sQuery(id+"F4.wireOp",EDGE,"E6")])],"isStart":true});
            var Q690;
            Q690=makeQuery(id+"F5.opExtrude","CAP_EDGE",EDGE,{"disambiguationData":[OSD([sQuery(id+"F4.wireOp",EDGE,"E6")])],"isStart":true});
            var Q691;
            Q691=makeQuery(id+"F5.opExtrude","CAP_EDGE",EDGE,{"disambiguationData":[OSD([sQuery(id+"F4.wireOp",EDGE,"E6")])],"isStart":true});
            var Q692;
            Q692=makeQuery(id+"F5.opExtrude","CAP_EDGE",EDGE,{"disambiguationData":[OSD([sQuery(id+"F4.wireOp",EDGE,"E6")])],"isStart":true});
            var Q693;
            Q693=makeQuery(id+"F5.opExtrude","CAP_EDGE",EDGE,{"disambiguationData":[OSD([sQuery(id+"F4.wireOp",EDGE,"E6")])],"isStart":true});
            var Q694;
            Q694=makeQuery(id+"F5.opExtrude","CAP_EDGE",EDGE,{"disambiguationData":[OSD([sQuery(id+"F4.wireOp",EDGE,"E6")])],"isStart":true});
            var Q695;
            Q695=makeQuery(id+"F5.opExtrude","CAP_EDGE",EDGE,{"disambiguationData":[OSD([sQuery(id+"F4.wireOp",EDGE,"E6")])],"isStart":true});
            var Q696;
            Q696=makeQuery(id+"F5.opExtrude","CAP_EDGE",EDGE,{"disambiguationData":[OSD([sQuery(id+"F4.wireOp",EDGE,"E6")])],"isStart":true});
            var Q697;
            Q697=makeQuery(id+"F5.opExtrude","CAP_EDGE",EDGE,{"disambiguationData":[OSD([sQuery(id+"F4.wireOp",EDGE,"E6")])],"isStart":true});
            var Q698;
            Q698=makeQuery(id+"F5.opExtrude","CAP_EDGE",EDGE,{"disambiguationData":[OSD([sQuery(id+"F4.wireOp",EDGE,"E6")])],"isStart":true});
            var Q699;
            Q699=makeQuery(id+"F5.opExtrude","CAP_EDGE",EDGE,{"disambiguationData":[OSD([sQuery(id+"F4.wireOp",EDGE,"E6")])],"isStart":true});
            var Q700;
            Q700=makeQuery(id+"F5.opExtrude","CAP_EDGE",EDGE,{"disambiguationData":[OSD([sQuery(id+"F4.wireOp",EDGE,"E6")])],"isStart":true});
            var Q701;
            Q701=makeQuery(id+"F5.opExtrude","CAP_EDGE",EDGE,{"disambiguationData":[OSD([sQuery(id+"F4.wireOp",EDGE,"E6")])],"isStart":true});
            var Q702;
            Q702=makeQuery(id+"F5.opExtrude","CAP_EDGE",EDGE,{"disambiguationData":[OSD([sQuery(id+"F4.wireOp",EDGE,"E6")])],"isStart":true});
            var Q703;
            Q703=makeQuery(id+"F5.opExtrude","CAP_EDGE",EDGE,{"disambiguationData":[OSD([sQuery(id+"F4.wireOp",EDGE,"E6")])],"isStart":true});
            var Q704;
            Q704=makeQuery(id+"F5.opExtrude","CAP_EDGE",EDGE,{"disambiguationData":[OSD([sQuery(id+"F4.wireOp",EDGE,"E6")])],"isStart":true});
            var Q705;
            Q705=makeQuery(id+"F5.opExtrude","CAP_EDGE",EDGE,{"disambiguationData":[OSD([sQuery(id+"F4.wireOp",EDGE,"E6")])],"isStart":true});
            var Q706;
            Q706=makeQuery(id+"F5.opExtrude","CAP_EDGE",EDGE,{"disambiguationData":[OSD([sQuery(id+"F4.wireOp",EDGE,"E6")])],"isStart":true});
            var Q707;
            Q707=makeQuery(id+"F5.opExtrude","CAP_EDGE",EDGE,{"disambiguationData":[OSD([sQuery(id+"F4.wireOp",EDGE,"E6")])],"isStart":true});
            var Q708;
            Q708=makeQuery(id+"F5.opExtrude","CAP_EDGE",EDGE,{"disambiguationData":[OSD([sQuery(id+"F4.wireOp",EDGE,"E6")])],"isStart":true});
            var Q709;
            Q709=makeQuery(id+"F5.opExtrude","CAP_EDGE",EDGE,{"disambiguationData":[OSD([sQuery(id+"F4.wireOp",EDGE,"E6")])],"isStart":true});
            var Q710;
            Q710=makeQuery(id+"F5.opExtrude","CAP_EDGE",EDGE,{"disambiguationData":[OSD([sQuery(id+"F4.wireOp",EDGE,"E6")])],"isStart":true});
            var Q711;
            Q711=makeQuery(id+"F5.opExtrude","CAP_EDGE",EDGE,{"disambiguationData":[OSD([sQuery(id+"F4.wireOp",EDGE,"E6")])],"isStart":true});
            var Q712;
            Q712=makeQuery(id+"F5.opExtrude","CAP_EDGE",EDGE,{"disambiguationData":[OSD([sQuery(id+"F4.wireOp",EDGE,"E6")])],"isStart":true});
            var Q713;
            Q713=makeQuery(id+"F5.opExtrude","CAP_EDGE",EDGE,{"disambiguationData":[OSD([sQuery(id+"F4.wireOp",EDGE,"E6")])],"isStart":true});
            var Q714;
            Q714=makeQuery(id+"F5.opExtrude","CAP_EDGE",EDGE,{"disambiguationData":[OSD([sQuery(id+"F4.wireOp",EDGE,"E6")])],"isStart":true});
            var Q715;
            Q715=makeQuery(id+"F5.opExtrude","CAP_EDGE",EDGE,{"disambiguationData":[OSD([sQuery(id+"F4.wireOp",EDGE,"E6")])],"isStart":true});
            var Q716;
            Q716=makeQuery(id+"F5.opExtrude","CAP_EDGE",EDGE,{"disambiguationData":[OSD([sQuery(id+"F4.wireOp",EDGE,"E6")])],"isStart":true});
            var Q717;
            Q717=makeQuery(id+"F5.opExtrude","CAP_EDGE",EDGE,{"disambiguationData":[OSD([sQuery(id+"F4.wireOp",EDGE,"E6")])],"isStart":true});
            var Q718;
            Q718=makeQuery(id+"F5.opExtrude","CAP_EDGE",EDGE,{"disambiguationData":[OSD([sQuery(id+"F4.wireOp",EDGE,"E6")])],"isStart":true});
            var Q719;
            Q719=makeQuery(id+"F5.opExtrude","CAP_EDGE",EDGE,{"disambiguationData":[OSD([sQuery(id+"F4.wireOp",EDGE,"E6")])],"isStart":true});
            var Q720;
            Q720=makeQuery(id+"F5.opExtrude","CAP_EDGE",EDGE,{"disambiguationData":[OSD([sQuery(id+"F4.wireOp",EDGE,"E6")])],"isStart":true});
            var Q721;
            Q721=makeQuery(id+"F5.opExtrude","CAP_EDGE",EDGE,{"disambiguationData":[OSD([sQuery(id+"F4.wireOp",EDGE,"E6")])],"isStart":true});
            var Q722;
            Q722=makeQuery(id+"F5.opExtrude","CAP_EDGE",EDGE,{"disambiguationData":[OSD([sQuery(id+"F4.wireOp",EDGE,"E6")])],"isStart":true});
            var Q723;
            Q723=makeQuery(id+"F5.opExtrude","CAP_EDGE",EDGE,{"disambiguationData":[OSD([sQuery(id+"F4.wireOp",EDGE,"E6")])],"isStart":true});
            var Q724;
            Q724=makeQuery(id+"F5.opExtrude","CAP_EDGE",EDGE,{"disambiguationData":[OSD([sQuery(id+"F4.wireOp",EDGE,"E6")])],"isStart":true});
            var Q725;
            Q725=makeQuery(id+"F5.opExtrude","CAP_EDGE",EDGE,{"disambiguationData":[OSD([sQuery(id+"F4.wireOp",EDGE,"E6")])],"isStart":true});
            var Q726;
            Q726=makeQuery(id+"F5.opExtrude","CAP_EDGE",EDGE,{"disambiguationData":[OSD([sQuery(id+"F4.wireOp",EDGE,"E6")])],"isStart":true});
            var Q727;
            Q727=makeQuery(id+"F5.opExtrude","CAP_EDGE",EDGE,{"disambiguationData":[OSD([sQuery(id+"F4.wireOp",EDGE,"E6")])],"isStart":true});
            var Q728;
            Q728=makeQuery(id+"F5.opExtrude","CAP_EDGE",EDGE,{"disambiguationData":[OSD([sQuery(id+"F4.wireOp",EDGE,"E6")])],"isStart":true});
            var Q729;
            Q729=makeQuery(id+"F5.opExtrude","CAP_EDGE",EDGE,{"disambiguationData":[OSD([sQuery(id+"F4.wireOp",EDGE,"E6")])],"isStart":true});
            var Q730;
            Q730=makeQuery(id+"F5.opExtrude","CAP_EDGE",EDGE,{"disambiguationData":[OSD([sQuery(id+"F4.wireOp",EDGE,"E6")])],"isStart":true});
            var Q731;
            Q731=makeQuery(id+"F5.opExtrude","CAP_EDGE",EDGE,{"disambiguationData":[OSD([sQuery(id+"F4.wireOp",EDGE,"E6")])],"isStart":true});
            var Q732;
            Q732=makeQuery(id+"F5.opExtrude","CAP_EDGE",EDGE,{"disambiguationData":[OSD([sQuery(id+"F4.wireOp",EDGE,"E6")])],"isStart":true});
            var Q733;
            Q733=makeQuery(id+"F5.opExtrude","CAP_EDGE",EDGE,{"disambiguationData":[OSD([sQuery(id+"F4.wireOp",EDGE,"E6")])],"isStart":true});
            var Q734;
            Q734=makeQuery(id+"F5.opExtrude","CAP_EDGE",EDGE,{"disambiguationData":[OSD([sQuery(id+"F4.wireOp",EDGE,"E6")])],"isStart":true});
            var Q735;
            Q735=makeQuery(id+"F5.opExtrude","CAP_EDGE",EDGE,{"disambiguationData":[OSD([sQuery(id+"F4.wireOp",EDGE,"E6")])],"isStart":true});
            var Q736;
            Q736=makeQuery(id+"F5.opExtrude","CAP_EDGE",EDGE,{"disambiguationData":[OSD([sQuery(id+"F4.wireOp",EDGE,"E6")])],"isStart":true});
            var Q737;
            Q737=makeQuery(id+"F5.opExtrude","CAP_EDGE",EDGE,{"disambiguationData":[OSD([sQuery(id+"F4.wireOp",EDGE,"E6")])],"isStart":true});
            var Q738;
            Q738=makeQuery(id+"F5.opExtrude","CAP_EDGE",EDGE,{"disambiguationData":[OSD([sQuery(id+"F4.wireOp",EDGE,"E6")])],"isStart":true});
            var Q739;
            Q739=makeQuery(id+"F5.opExtrude","CAP_EDGE",EDGE,{"disambiguationData":[OSD([sQuery(id+"F4.wireOp",EDGE,"E6")])],"isStart":true});
            var Q740;
            Q740=makeQuery(id+"F5.opExtrude","CAP_EDGE",EDGE,{"disambiguationData":[OSD([sQuery(id+"F4.wireOp",EDGE,"E6")])],"isStart":true});
            var Q741;
            Q741=makeQuery(id+"F5.opExtrude","CAP_EDGE",EDGE,{"disambiguationData":[OSD([sQuery(id+"F4.wireOp",EDGE,"E6")])],"isStart":true});
            var Q742;
            Q742=makeQuery(id+"F5.opExtrude","CAP_EDGE",EDGE,{"disambiguationData":[OSD([sQuery(id+"F4.wireOp",EDGE,"E6")])],"isStart":true});
            var Q743;
            Q743=makeQuery(id+"F5.opExtrude","CAP_EDGE",EDGE,{"disambiguationData":[OSD([sQuery(id+"F4.wireOp",EDGE,"E6")])],"isStart":true});
            var Q744;
            Q744=makeQuery(id+"F5.opExtrude","CAP_EDGE",EDGE,{"disambiguationData":[OSD([sQuery(id+"F4.wireOp",EDGE,"E6")])],"isStart":true});
            var Q745;
            Q745=makeQuery(id+"F5.opExtrude","CAP_EDGE",EDGE,{"disambiguationData":[OSD([sQuery(id+"F4.wireOp",EDGE,"E6")])],"isStart":true});
            var Q746;
            Q746=makeQuery(id+"F5.opExtrude","CAP_EDGE",EDGE,{"disambiguationData":[OSD([sQuery(id+"F4.wireOp",EDGE,"E6")])],"isStart":true});
            var Q747;
            Q747=makeQuery(id+"F5.opExtrude","CAP_EDGE",EDGE,{"disambiguationData":[OSD([sQuery(id+"F4.wireOp",EDGE,"E6")])],"isStart":true});
            var Q748;
            Q748=makeQuery(id+"F5.opExtrude","CAP_EDGE",EDGE,{"disambiguationData":[OSD([sQuery(id+"F4.wireOp",EDGE,"E6")])],"isStart":true});
            var Q749;
            Q749=makeQuery(id+"F5.opExtrude","CAP_EDGE",EDGE,{"disambiguationData":[OSD([sQuery(id+"F4.wireOp",EDGE,"E6")])],"isStart":true});
            var Q750;
            Q750=makeQuery(id+"F5.opExtrude","CAP_EDGE",EDGE,{"disambiguationData":[OSD([sQuery(id+"F4.wireOp",EDGE,"E6")])],"isStart":true});
            var Q751;
            Q751=makeQuery(id+"F5.opExtrude","CAP_EDGE",EDGE,{"disambiguationData":[OSD([sQuery(id+"F4.wireOp",EDGE,"E6")])],"isStart":true});
            var Q752;
            Q752=makeQuery(id+"F5.opExtrude","CAP_EDGE",EDGE,{"disambiguationData":[OSD([sQuery(id+"F4.wireOp",EDGE,"E6")])],"isStart":true});
            var Q753;
            Q753=makeQuery(id+"F5.opExtrude","CAP_EDGE",EDGE,{"disambiguationData":[OSD([sQuery(id+"F4.wireOp",EDGE,"E6")])],"isStart":true});
            var Q754;
            Q754=makeQuery(id+"F5.opExtrude","CAP_EDGE",EDGE,{"disambiguationData":[OSD([sQuery(id+"F4.wireOp",EDGE,"E6")])],"isStart":true});
            var Q755;
            Q755=makeQuery(id+"F5.opExtrude","CAP_EDGE",EDGE,{"disambiguationData":[OSD([sQuery(id+"F4.wireOp",EDGE,"E6")])],"isStart":true});
            var Q756;
            Q756=makeQuery(id+"F5.opExtrude","CAP_EDGE",EDGE,{"disambiguationData":[OSD([sQuery(id+"F4.wireOp",EDGE,"E6")])],"isStart":true});
            var Q757;
            Q757=makeQuery(id+"F5.opExtrude","CAP_EDGE",EDGE,{"disambiguationData":[OSD([sQuery(id+"F4.wireOp",EDGE,"E6")])],"isStart":true});
            var Q758;
            Q758=makeQuery(id+"F5.opExtrude","CAP_EDGE",EDGE,{"disambiguationData":[OSD([sQuery(id+"F4.wireOp",EDGE,"E6")])],"isStart":true});
            var Q759;
            Q759=makeQuery(id+"F5.opExtrude","CAP_EDGE",EDGE,{"disambiguationData":[OSD([sQuery(id+"F4.wireOp",EDGE,"E6")])],"isStart":true});
            var Q760;
            Q760=makeQuery(id+"F5.opExtrude","CAP_EDGE",EDGE,{"disambiguationData":[OSD([sQuery(id+"F4.wireOp",EDGE,"E6")])],"isStart":true});
            var Q761;
            Q761=makeQuery(id+"F5.opExtrude","CAP_EDGE",EDGE,{"disambiguationData":[OSD([sQuery(id+"F4.wireOp",EDGE,"E6")])],"isStart":true});
            var Q762;
            Q762=makeQuery(id+"F5.opExtrude","CAP_EDGE",EDGE,{"disambiguationData":[OSD([sQuery(id+"F4.wireOp",EDGE,"E6")])],"isStart":true});
            var Q763;
            Q763=makeQuery(id+"F5.opExtrude","CAP_EDGE",EDGE,{"disambiguationData":[OSD([sQuery(id+"F4.wireOp",EDGE,"E6")])],"isStart":true});
            var Q764;
            Q764=makeQuery(id+"F5.opExtrude","CAP_EDGE",EDGE,{"disambiguationData":[OSD([sQuery(id+"F4.wireOp",EDGE,"E6")])],"isStart":true});
            var Q765;
            Q765=makeQuery(id+"F5.opExtrude","CAP_EDGE",EDGE,{"disambiguationData":[OSD([sQuery(id+"F4.wireOp",EDGE,"E6")])],"isStart":true});
            var Q766;
            Q766=makeQuery(id+"F5.opExtrude","CAP_EDGE",EDGE,{"disambiguationData":[OSD([sQuery(id+"F4.wireOp",EDGE,"E6")])],"isStart":true});
            var Q767;
            Q767=makeQuery(id+"F5.opExtrude","CAP_EDGE",EDGE,{"disambiguationData":[OSD([sQuery(id+"F4.wireOp",EDGE,"E6")])],"isStart":true});
            var Q768;
            Q768=makeQuery(id+"F5.opExtrude","CAP_EDGE",EDGE,{"disambiguationData":[OSD([sQuery(id+"F4.wireOp",EDGE,"E6")])],"isStart":true});
            var Q769;
            Q769=makeQuery(id+"F5.opExtrude","CAP_EDGE",EDGE,{"disambiguationData":[OSD([sQuery(id+"F4.wireOp",EDGE,"E6")])],"isStart":true});
            var Q770;
            Q770=makeQuery(id+"F5.opExtrude","CAP_EDGE",EDGE,{"disambiguationData":[OSD([sQuery(id+"F4.wireOp",EDGE,"E6")])],"isStart":true});
            var Q771;
            Q771=makeQuery(id+"F5.opExtrude","CAP_EDGE",EDGE,{"disambiguationData":[OSD([sQuery(id+"F4.wireOp",EDGE,"E6")])],"isStart":true});
            var Q772;
            Q772=makeQuery(id+"F5.opExtrude","CAP_EDGE",EDGE,{"disambiguationData":[OSD([sQuery(id+"F4.wireOp",EDGE,"E6")])],"isStart":true});
            var Q773;
            Q773=makeQuery(id+"F5.opExtrude","CAP_EDGE",EDGE,{"disambiguationData":[OSD([sQuery(id+"F4.wireOp",EDGE,"E6")])],"isStart":true});
            var Q774;
            Q774=makeQuery(id+"F5.opExtrude","CAP_EDGE",EDGE,{"disambiguationData":[OSD([sQuery(id+"F4.wireOp",EDGE,"E6")])],"isStart":true});
            var Q775;
            Q775=makeQuery(id+"F5.opExtrude","CAP_EDGE",EDGE,{"disambiguationData":[OSD([sQuery(id+"F4.wireOp",EDGE,"E6")])],"isStart":true});
            var Q776;
            Q776=makeQuery(id+"F5.opExtrude","CAP_EDGE",EDGE,{"disambiguationData":[OSD([sQuery(id+"F4.wireOp",EDGE,"E6")])],"isStart":true});
            var Q777;
            Q777=makeQuery(id+"F5.opExtrude","CAP_EDGE",EDGE,{"disambiguationData":[OSD([sQuery(id+"F4.wireOp",EDGE,"E6")])],"isStart":true});
            var Q778;
            Q778=makeQuery(id+"F5.opExtrude","CAP_EDGE",EDGE,{"disambiguationData":[OSD([sQuery(id+"F4.wireOp",EDGE,"E6")])],"isStart":true});
            var Q779;
            Q779=makeQuery(id+"F5.opExtrude","CAP_EDGE",EDGE,{"disambiguationData":[OSD([sQuery(id+"F4.wireOp",EDGE,"E6")])],"isStart":true});
            var Q780;
            Q780=makeQuery(id+"F5.opExtrude","CAP_EDGE",EDGE,{"disambiguationData":[OSD([sQuery(id+"F4.wireOp",EDGE,"E6")])],"isStart":true});
            var Q781;
            Q781=makeQuery(id+"F5.opExtrude","CAP_EDGE",EDGE,{"disambiguationData":[OSD([sQuery(id+"F4.wireOp",EDGE,"E6")])],"isStart":true});
            var Q782;
            Q782=makeQuery(id+"F5.opExtrude","CAP_EDGE",EDGE,{"disambiguationData":[OSD([sQuery(id+"F4.wireOp",EDGE,"E6")])],"isStart":true});
            var Q783;
            Q783=makeQuery(id+"F5.opExtrude","CAP_EDGE",EDGE,{"disambiguationData":[OSD([sQuery(id+"F4.wireOp",EDGE,"E6")])],"isStart":true});
            var Q784;
            Q784=makeQuery(id+"F5.opExtrude","CAP_EDGE",EDGE,{"disambiguationData":[OSD([sQuery(id+"F4.wireOp",EDGE,"E6")])],"isStart":true});
            var Q785;
            Q785=makeQuery(id+"F5.opExtrude","CAP_EDGE",EDGE,{"disambiguationData":[OSD([sQuery(id+"F4.wireOp",EDGE,"E6")])],"isStart":true});
            var Q786;
            Q786=makeQuery(id+"F5.opExtrude","CAP_EDGE",EDGE,{"disambiguationData":[OSD([sQuery(id+"F4.wireOp",EDGE,"E6")])],"isStart":true});
            var Q787;
            Q787=makeQuery(id+"F5.opExtrude","CAP_EDGE",EDGE,{"disambiguationData":[OSD([sQuery(id+"F4.wireOp",EDGE,"E6")])],"isStart":true});
            var Q788;
            Q788=makeQuery(id+"F5.opExtrude","CAP_EDGE",EDGE,{"disambiguationData":[OSD([sQuery(id+"F4.wireOp",EDGE,"E6")])],"isStart":true});
            var Q789;
            Q789=makeQuery(id+"F5.opExtrude","CAP_EDGE",EDGE,{"disambiguationData":[OSD([sQuery(id+"F4.wireOp",EDGE,"E6")])],"isStart":true});
            var Q790;
            Q790=makeQuery(id+"F5.opExtrude","CAP_EDGE",EDGE,{"disambiguationData":[OSD([sQuery(id+"F4.wireOp",EDGE,"E6")])],"isStart":true});
            var Q791;
            Q791=makeQuery(id+"F5.opExtrude","CAP_EDGE",EDGE,{"disambiguationData":[OSD([sQuery(id+"F4.wireOp",EDGE,"E6")])],"isStart":true});
            var Q792;
            Q792=makeQuery(id+"F5.opExtrude","CAP_EDGE",EDGE,{"disambiguationData":[OSD([sQuery(id+"F4.wireOp",EDGE,"E6")])],"isStart":true});
            var Q793;
            Q793=makeQuery(id+"F5.opExtrude","CAP_EDGE",EDGE,{"disambiguationData":[OSD([sQuery(id+"F4.wireOp",EDGE,"E6")])],"isStart":true});
            var Q794;
            Q794=makeQuery(id+"F5.opExtrude","CAP_EDGE",EDGE,{"disambiguationData":[OSD([sQuery(id+"F4.wireOp",EDGE,"E6")])],"isStart":true});
            var Q795;
            Q795=makeQuery(id+"F5.opExtrude","CAP_EDGE",EDGE,{"disambiguationData":[OSD([sQuery(id+"F4.wireOp",EDGE,"E6")])],"isStart":true});
            var Q796;
            Q796=makeQuery(id+"F5.opExtrude","CAP_EDGE",EDGE,{"disambiguationData":[OSD([sQuery(id+"F4.wireOp",EDGE,"E6")])],"isStart":true});
            var Q797;
            Q797=makeQuery(id+"F5.opExtrude","CAP_EDGE",EDGE,{"disambiguationData":[OSD([sQuery(id+"F4.wireOp",EDGE,"E6")])],"isStart":true});
            var Q798;
            Q798=makeQuery(id+"F5.opExtrude","CAP_EDGE",EDGE,{"disambiguationData":[OSD([sQuery(id+"F4.wireOp",EDGE,"E6")])],"isStart":true});
            var Q799;
            Q799=makeQuery(id+"F5.opExtrude","CAP_EDGE",EDGE,{"disambiguationData":[OSD([sQuery(id+"F4.wireOp",EDGE,"E6")])],"isStart":true});
            var Q800;
            Q800=makeQuery(id+"F5.opExtrude","CAP_EDGE",EDGE,{"disambiguationData":[OSD([sQuery(id+"F4.wireOp",EDGE,"E6")])],"isStart":true});
            var Q801;
            Q801=makeQuery(id+"F5.opExtrude","CAP_EDGE",EDGE,{"disambiguationData":[OSD([sQuery(id+"F4.wireOp",EDGE,"E6")])],"isStart":true});
            var Q802;
            Q802=makeQuery(id+"F5.opExtrude","CAP_EDGE",EDGE,{"disambiguationData":[OSD([sQuery(id+"F4.wireOp",EDGE,"E6")])],"isStart":true});
            var Q803;
            Q803=makeQuery(id+"F5.opExtrude","CAP_EDGE",EDGE,{"disambiguationData":[OSD([sQuery(id+"F4.wireOp",EDGE,"E6")])],"isStart":true});
            var Q804;
            Q804=makeQuery(id+"F5.opExtrude","CAP_EDGE",EDGE,{"disambiguationData":[OSD([sQuery(id+"F4.wireOp",EDGE,"E6")])],"isStart":true});
            var Q805;
            Q805=makeQuery(id+"F5.opExtrude","CAP_EDGE",EDGE,{"disambiguationData":[OSD([sQuery(id+"F4.wireOp",EDGE,"E6")])],"isStart":true});
            var Q806;
            Q806=makeQuery(id+"F5.opExtrude","CAP_EDGE",EDGE,{"disambiguationData":[OSD([sQuery(id+"F4.wireOp",EDGE,"E6")])],"isStart":true});
            var Q807;
            Q807=makeQuery(id+"F5.opExtrude","CAP_EDGE",EDGE,{"disambiguationData":[OSD([sQuery(id+"F4.wireOp",EDGE,"E6")])],"isStart":true});
            var Q808;
            Q808=makeQuery(id+"F5.opExtrude","CAP_EDGE",EDGE,{"disambiguationData":[OSD([sQuery(id+"F4.wireOp",EDGE,"E6")])],"isStart":true});
            var Q809;
            Q809=makeQuery(id+"F5.opExtrude","CAP_EDGE",EDGE,{"disambiguationData":[OSD([sQuery(id+"F4.wireOp",EDGE,"E6")])],"isStart":true});
            var Q810;
            Q810=makeQuery(id+"F5.opExtrude","CAP_EDGE",EDGE,{"disambiguationData":[OSD([sQuery(id+"F4.wireOp",EDGE,"E6")])],"isStart":true});
            var Q811;
            Q811=makeQuery(id+"F5.opExtrude","CAP_EDGE",EDGE,{"disambiguationData":[OSD([sQuery(id+"F4.wireOp",EDGE,"E6")])],"isStart":true});
            var Q812;
            Q812=makeQuery(id+"F5.opExtrude","CAP_EDGE",EDGE,{"disambiguationData":[OSD([sQuery(id+"F4.wireOp",EDGE,"E6")])],"isStart":true});
            var Q813;
            Q813=makeQuery(id+"F5.opExtrude","CAP_EDGE",EDGE,{"disambiguationData":[OSD([sQuery(id+"F4.wireOp",EDGE,"E6")])],"isStart":true});
            var Q814;
            Q814=makeQuery(id+"F5.opExtrude","CAP_EDGE",EDGE,{"disambiguationData":[OSD([sQuery(id+"F4.wireOp",EDGE,"E6")])],"isStart":true});
            var Q815;
            Q815=makeQuery(id+"F5.opExtrude","CAP_EDGE",EDGE,{"disambiguationData":[OSD([sQuery(id+"F4.wireOp",EDGE,"E6")])],"isStart":true});
            var Q816;
            Q816=makeQuery(id+"F5.opExtrude","CAP_EDGE",EDGE,{"disambiguationData":[OSD([sQuery(id+"F4.wireOp",EDGE,"E6")])],"isStart":true});
            var Q817;
            Q817=makeQuery(id+"F5.opExtrude","CAP_EDGE",EDGE,{"disambiguationData":[OSD([sQuery(id+"F4.wireOp",EDGE,"E6")])],"isStart":true});
            var Q818;
            Q818=makeQuery(id+"F5.opExtrude","CAP_EDGE",EDGE,{"disambiguationData":[OSD([sQuery(id+"F4.wireOp",EDGE,"E6")])],"isStart":true});
            var Q819;
            Q819=makeQuery(id+"F5.opExtrude","CAP_EDGE",EDGE,{"disambiguationData":[OSD([sQuery(id+"F4.wireOp",EDGE,"E6")])],"isStart":true});
            var Q820;
            Q820=makeQuery(id+"F5.opExtrude","CAP_EDGE",EDGE,{"disambiguationData":[OSD([sQuery(id+"F4.wireOp",EDGE,"E6")])],"isStart":true});
            var Q821;
            Q821=makeQuery(id+"F5.opExtrude","CAP_EDGE",EDGE,{"disambiguationData":[OSD([sQuery(id+"F4.wireOp",EDGE,"E6")])],"isStart":true});
            var Q822;
            Q822=makeQuery(id+"F5.opExtrude","CAP_EDGE",EDGE,{"disambiguationData":[OSD([sQuery(id+"F4.wireOp",EDGE,"E6")])],"isStart":true});
            var Q823;
            Q823=makeQuery(id+"F5.opExtrude","CAP_EDGE",EDGE,{"disambiguationData":[OSD([sQuery(id+"F4.wireOp",EDGE,"E6")])],"isStart":true});
            var Q824;
            Q824=makeQuery(id+"F5.opExtrude","CAP_EDGE",EDGE,{"disambiguationData":[OSD([sQuery(id+"F4.wireOp",EDGE,"E6")])],"isStart":true});
            var Q825;
            Q825=makeQuery(id+"F5.opExtrude","CAP_EDGE",EDGE,{"disambiguationData":[OSD([sQuery(id+"F4.wireOp",EDGE,"E6")])],"isStart":true});
            var Q826;
            Q826=makeQuery(id+"F5.opExtrude","CAP_EDGE",EDGE,{"disambiguationData":[OSD([sQuery(id+"F4.wireOp",EDGE,"E6")])],"isStart":true});
            var Q827;
            Q827=makeQuery(id+"F5.opExtrude","CAP_EDGE",EDGE,{"disambiguationData":[OSD([sQuery(id+"F4.wireOp",EDGE,"E6")])],"isStart":true});
            var Q828;
            Q828=makeQuery(id+"F5.opExtrude","CAP_EDGE",EDGE,{"disambiguationData":[OSD([sQuery(id+"F4.wireOp",EDGE,"E6")])],"isStart":true});
            var Q829;
            Q829=makeQuery(id+"F5.opExtrude","CAP_EDGE",EDGE,{"disambiguationData":[OSD([sQuery(id+"F4.wireOp",EDGE,"E6")])],"isStart":true});
            var Q830;
            Q830=makeQuery(id+"F5.opExtrude","CAP_EDGE",EDGE,{"disambiguationData":[OSD([sQuery(id+"F4.wireOp",EDGE,"E6")])],"isStart":true});
            var Q831;
            Q831=makeQuery(id+"F5.opExtrude","CAP_EDGE",EDGE,{"disambiguationData":[OSD([sQuery(id+"F4.wireOp",EDGE,"E6")])],"isStart":true});
            var Q832;
            Q832=makeQuery(id+"F5.opExtrude","CAP_EDGE",EDGE,{"disambiguationData":[OSD([sQuery(id+"F4.wireOp",EDGE,"E6")])],"isStart":true});
            var Q833;
            Q833=makeQuery(id+"F5.opExtrude","CAP_EDGE",EDGE,{"disambiguationData":[OSD([sQuery(id+"F4.wireOp",EDGE,"E6")])],"isStart":true});
            var Q834;
            Q834=makeQuery(id+"F5.opExtrude","CAP_EDGE",EDGE,{"disambiguationData":[OSD([sQuery(id+"F4.wireOp",EDGE,"E6")])],"isStart":true});
            var Q835;
            Q835=makeQuery(id+"F5.opExtrude","CAP_EDGE",EDGE,{"disambiguationData":[OSD([sQuery(id+"F4.wireOp",EDGE,"E6")])],"isStart":true});
            var Q836;
            Q836=makeQuery(id+"F5.opExtrude","CAP_EDGE",EDGE,{"disambiguationData":[OSD([sQuery(id+"F4.wireOp",EDGE,"E6")])],"isStart":true});
            var Q837;
            Q837=makeQuery(id+"F5.opExtrude","CAP_EDGE",EDGE,{"disambiguationData":[OSD([sQuery(id+"F4.wireOp",EDGE,"E6")])],"isStart":true});
            var Q838;
            Q838=makeQuery(id+"F5.opExtrude","CAP_EDGE",EDGE,{"disambiguationData":[OSD([sQuery(id+"F4.wireOp",EDGE,"E6")])],"isStart":true});
            var Q839;
            Q839=makeQuery(id+"F5.opExtrude","CAP_EDGE",EDGE,{"disambiguationData":[OSD([sQuery(id+"F4.wireOp",EDGE,"E6")])],"isStart":true});
            var Q840;
            Q840=makeQuery(id+"F5.opExtrude","CAP_EDGE",EDGE,{"disambiguationData":[OSD([sQuery(id+"F4.wireOp",EDGE,"E6")])],"isStart":true});
            var Q841;
            Q841=makeQuery(id+"F5.opExtrude","CAP_EDGE",EDGE,{"disambiguationData":[OSD([sQuery(id+"F4.wireOp",EDGE,"E6")])],"isStart":true});
            var Q842;
            Q842=makeQuery(id+"F5.opExtrude","CAP_EDGE",EDGE,{"disambiguationData":[OSD([sQuery(id+"F4.wireOp",EDGE,"E6")])],"isStart":true});
            var Q843;
            Q843=makeQuery(id+"F5.opExtrude","CAP_EDGE",EDGE,{"disambiguationData":[OSD([sQuery(id+"F4.wireOp",EDGE,"E6")])],"isStart":true});
            var Q844;
            Q844=makeQuery(id+"F5.opExtrude","CAP_EDGE",EDGE,{"disambiguationData":[OSD([sQuery(id+"F4.wireOp",EDGE,"E6")])],"isStart":true});
            var Q845;
            Q845=makeQuery(id+"F5.opExtrude","CAP_EDGE",EDGE,{"disambiguationData":[OSD([sQuery(id+"F4.wireOp",EDGE,"E6")])],"isStart":true});
            var Q846;
            Q846=makeQuery(id+"F5.opExtrude","CAP_EDGE",EDGE,{"disambiguationData":[OSD([sQuery(id+"F4.wireOp",EDGE,"E6")])],"isStart":true});
            var Q847;
            Q847=makeQuery(id+"F5.opExtrude","CAP_EDGE",EDGE,{"disambiguationData":[OSD([sQuery(id+"F4.wireOp",EDGE,"E6")])],"isStart":true});
            var Q848;
            Q848=makeQuery(id+"F5.opExtrude","CAP_EDGE",EDGE,{"disambiguationData":[OSD([sQuery(id+"F4.wireOp",EDGE,"E6")])],"isStart":true});
            var Q849;
            Q849=makeQuery(id+"F5.opExtrude","CAP_EDGE",EDGE,{"disambiguationData":[OSD([sQuery(id+"F4.wireOp",EDGE,"E6")])],"isStart":true});
            var Q850;
            Q850=makeQuery(id+"F5.opExtrude","CAP_EDGE",EDGE,{"disambiguationData":[OSD([sQuery(id+"F4.wireOp",EDGE,"E6")])],"isStart":true});
            var Q851;
            Q851=makeQuery(id+"F5.opExtrude","CAP_EDGE",EDGE,{"disambiguationData":[OSD([sQuery(id+"F4.wireOp",EDGE,"E6")])],"isStart":true});
            var Q852;
            Q852=makeQuery(id+"F5.opExtrude","CAP_EDGE",EDGE,{"disambiguationData":[OSD([sQuery(id+"F4.wireOp",EDGE,"E6")])],"isStart":true});
            var Q853;
            Q853=makeQuery(id+"F5.opExtrude","CAP_EDGE",EDGE,{"disambiguationData":[OSD([sQuery(id+"F4.wireOp",EDGE,"E6")])],"isStart":true});
            var Q854;
            Q854=makeQuery(id+"F5.opExtrude","CAP_EDGE",EDGE,{"disambiguationData":[OSD([sQuery(id+"F4.wireOp",EDGE,"E6")])],"isStart":true});
            var Q855;
            Q855=makeQuery(id+"F5.opExtrude","CAP_EDGE",EDGE,{"disambiguationData":[OSD([sQuery(id+"F4.wireOp",EDGE,"E6")])],"isStart":true});
            var Q856;
            Q856=makeQuery(id+"F5.opExtrude","CAP_EDGE",EDGE,{"disambiguationData":[OSD([sQuery(id+"F4.wireOp",EDGE,"E6")])],"isStart":true});
            var Q857;
            Q857=makeQuery(id+"F5.opExtrude","CAP_EDGE",EDGE,{"disambiguationData":[OSD([sQuery(id+"F4.wireOp",EDGE,"E6")])],"isStart":true});
            var Q858;
            Q858=makeQuery(id+"F5.opExtrude","CAP_EDGE",EDGE,{"disambiguationData":[OSD([sQuery(id+"F4.wireOp",EDGE,"E6")])],"isStart":true});
            var Q859;
            Q859=makeQuery(id+"F5.opExtrude","CAP_EDGE",EDGE,{"disambiguationData":[OSD([sQuery(id+"F4.wireOp",EDGE,"E6")])],"isStart":true});
            var Q860;
            Q860=makeQuery(id+"F5.opExtrude","CAP_EDGE",EDGE,{"disambiguationData":[OSD([sQuery(id+"F4.wireOp",EDGE,"E6")])],"isStart":true});
            var Q861;
            Q861=makeQuery(id+"F5.opExtrude","CAP_EDGE",EDGE,{"disambiguationData":[OSD([sQuery(id+"F4.wireOp",EDGE,"E6")])],"isStart":true});
            var Q862;
            Q862=makeQuery(id+"F5.opExtrude","CAP_EDGE",EDGE,{"disambiguationData":[OSD([sQuery(id+"F4.wireOp",EDGE,"E6")])],"isStart":true});
            var Q863;
            Q863=makeQuery(id+"F5.opExtrude","CAP_EDGE",EDGE,{"disambiguationData":[OSD([sQuery(id+"F4.wireOp",EDGE,"E6")])],"isStart":true});
            var Q864;
            Q864=makeQuery(id+"F5.opExtrude","CAP_EDGE",EDGE,{"disambiguationData":[OSD([sQuery(id+"F4.wireOp",EDGE,"E6")])],"isStart":true});
            var Q865;
            Q865=makeQuery(id+"F5.opExtrude","CAP_EDGE",EDGE,{"disambiguationData":[OSD([sQuery(id+"F4.wireOp",EDGE,"E6")])],"isStart":true});
            var Q866;
            Q866=makeQuery(id+"F5.opExtrude","CAP_EDGE",EDGE,{"disambiguationData":[OSD([sQuery(id+"F4.wireOp",EDGE,"E6")])],"isStart":true});
            var Q867;
            Q867=makeQuery(id+"F5.opExtrude","CAP_EDGE",EDGE,{"disambiguationData":[OSD([sQuery(id+"F4.wireOp",EDGE,"E6")])],"isStart":true});
            var Q868;
            Q868=makeQuery(id+"F5.opExtrude","CAP_EDGE",EDGE,{"disambiguationData":[OSD([sQuery(id+"F4.wireOp",EDGE,"E6")])],"isStart":true});
            var Q869;
            Q869=makeQuery(id+"F5.opExtrude","CAP_EDGE",EDGE,{"disambiguationData":[OSD([sQuery(id+"F4.wireOp",EDGE,"E6")])],"isStart":true});
            var Q870;
            Q870=makeQuery(id+"F5.opExtrude","CAP_EDGE",EDGE,{"disambiguationData":[OSD([sQuery(id+"F4.wireOp",EDGE,"E6")])],"isStart":true});
            var Q871;
            Q871=makeQuery(id+"F5.opExtrude","CAP_EDGE",EDGE,{"disambiguationData":[OSD([sQuery(id+"F4.wireOp",EDGE,"E6")])],"isStart":true});
            var Q872;
            Q872=makeQuery(id+"F5.opExtrude","CAP_EDGE",EDGE,{"disambiguationData":[OSD([sQuery(id+"F4.wireOp",EDGE,"E6")])],"isStart":true});
            var Q873;
            Q873=makeQuery(id+"F5.opExtrude","CAP_EDGE",EDGE,{"disambiguationData":[OSD([sQuery(id+"F4.wireOp",EDGE,"E6")])],"isStart":true});
            var Q874;
            Q874=makeQuery(id+"F5.opExtrude","CAP_EDGE",EDGE,{"disambiguationData":[OSD([sQuery(id+"F4.wireOp",EDGE,"E6")])],"isStart":true});
            var Q875;
            Q875=makeQuery(id+"F5.opExtrude","CAP_EDGE",EDGE,{"disambiguationData":[OSD([sQuery(id+"F4.wireOp",EDGE,"E6")])],"isStart":true});
            var Q876;
            Q876=makeQuery(id+"F5.opExtrude","CAP_EDGE",EDGE,{"disambiguationData":[OSD([sQuery(id+"F4.wireOp",EDGE,"E6")])],"isStart":true});
            var Q877;
            Q877=makeQuery(id+"F5.opExtrude","CAP_EDGE",EDGE,{"disambiguationData":[OSD([sQuery(id+"F4.wireOp",EDGE,"E6")])],"isStart":true});
            var Q878;
            Q878=makeQuery(id+"F5.opExtrude","CAP_EDGE",EDGE,{"disambiguationData":[OSD([sQuery(id+"F4.wireOp",EDGE,"E6")])],"isStart":true});
            var Q879;
            Q879=makeQuery(id+"F5.opExtrude","CAP_EDGE",EDGE,{"disambiguationData":[OSD([sQuery(id+"F4.wireOp",EDGE,"E6")])],"isStart":true});
            var Q880;
            Q880=makeQuery(id+"F5.opExtrude","CAP_EDGE",EDGE,{"disambiguationData":[OSD([sQuery(id+"F4.wireOp",EDGE,"E6")])],"isStart":true});
            var Q881;
            Q881=makeQuery(id+"F5.opExtrude","CAP_EDGE",EDGE,{"disambiguationData":[OSD([sQuery(id+"F4.wireOp",EDGE,"E6")])],"isStart":true});
            var Q882;
            Q882=makeQuery(id+"F5.opExtrude","CAP_EDGE",EDGE,{"disambiguationData":[OSD([sQuery(id+"F4.wireOp",EDGE,"E6")])],"isStart":true});
            var Q883;
            Q883=makeQuery(id+"F5.opExtrude","CAP_EDGE",EDGE,{"disambiguationData":[OSD([sQuery(id+"F4.wireOp",EDGE,"E6")])],"isStart":true});
            var Q884;
            Q884=makeQuery(id+"F5.opExtrude","CAP_EDGE",EDGE,{"disambiguationData":[OSD([sQuery(id+"F4.wireOp",EDGE,"E6")])],"isStart":true});
            var Q885;
            Q885=makeQuery(id+"F5.opExtrude","CAP_EDGE",EDGE,{"disambiguationData":[OSD([sQuery(id+"F4.wireOp",EDGE,"E6")])],"isStart":true});
            var Q886;
            Q886=makeQuery(id+"F5.opExtrude","CAP_EDGE",EDGE,{"disambiguationData":[OSD([sQuery(id+"F4.wireOp",EDGE,"E6")])],"isStart":true});
            var Q887;
            Q887=makeQuery(id+"F5.opExtrude","CAP_EDGE",EDGE,{"disambiguationData":[OSD([sQuery(id+"F4.wireOp",EDGE,"E6")])],"isStart":true});
            var Q888;
            Q888=makeQuery(id+"F5.opExtrude","CAP_EDGE",EDGE,{"disambiguationData":[OSD([sQuery(id+"F4.wireOp",EDGE,"E6")])],"isStart":true});
            var Q889;
            Q889=makeQuery(id+"F5.opExtrude","CAP_EDGE",EDGE,{"disambiguationData":[OSD([sQuery(id+"F4.wireOp",EDGE,"E6")])],"isStart":true});
            var Q890;
            Q890=makeQuery(id+"F5.opExtrude","CAP_EDGE",EDGE,{"disambiguationData":[OSD([sQuery(id+"F4.wireOp",EDGE,"E6")])],"isStart":true});
            var Q891;
            Q891=makeQuery(id+"F5.opExtrude","CAP_EDGE",EDGE,{"disambiguationData":[OSD([sQuery(id+"F4.wireOp",EDGE,"E6")])],"isStart":true});
            var Q892;
            Q892=makeQuery(id+"F5.opExtrude","CAP_EDGE",EDGE,{"disambiguationData":[OSD([sQuery(id+"F4.wireOp",EDGE,"E6")])],"isStart":true});
            var Q893;
            Q893=makeQuery(id+"F5.opExtrude","CAP_EDGE",EDGE,{"disambiguationData":[OSD([sQuery(id+"F4.wireOp",EDGE,"E6")])],"isStart":true});
            var Q894;
            Q894=makeQuery(id+"F5.opExtrude","CAP_EDGE",EDGE,{"disambiguationData":[OSD([sQuery(id+"F4.wireOp",EDGE,"E6")])],"isStart":true});
            var Q895;
            Q895=makeQuery(id+"F5.opExtrude","CAP_EDGE",EDGE,{"disambiguationData":[OSD([sQuery(id+"F4.wireOp",EDGE,"E6")])],"isStart":true});
            var Q896;
            Q896=makeQuery(id+"F5.opExtrude","CAP_EDGE",EDGE,{"disambiguationData":[OSD([sQuery(id+"F4.wireOp",EDGE,"E6")])],"isStart":true});
            var Q897;
            Q897=makeQuery(id+"F5.opExtrude","CAP_EDGE",EDGE,{"disambiguationData":[OSD([sQuery(id+"F4.wireOp",EDGE,"E6")])],"isStart":true});
            var Q898;
            Q898=makeQuery(id+"F5.opExtrude","CAP_EDGE",EDGE,{"disambiguationData":[OSD([sQuery(id+"F4.wireOp",EDGE,"E6")])],"isStart":true});
            var Q899;
            Q899=makeQuery(id+"F5.opExtrude","CAP_EDGE",EDGE,{"disambiguationData":[OSD([sQuery(id+"F4.wireOp",EDGE,"E6")])],"isStart":true});
            var Q900;
            Q900=makeQuery(id+"F5.opExtrude","CAP_EDGE",EDGE,{"disambiguationData":[OSD([sQuery(id+"F4.wireOp",EDGE,"E6")])],"isStart":true});
            var Q901;
            Q901=makeQuery(id+"F5.opExtrude","CAP_EDGE",EDGE,{"disambiguationData":[OSD([sQuery(id+"F4.wireOp",EDGE,"E6")])],"isStart":true});
            var Q902;
            Q902=makeQuery(id+"F5.opExtrude","CAP_EDGE",EDGE,{"disambiguationData":[OSD([sQuery(id+"F4.wireOp",EDGE,"E6")])],"isStart":true});
            var Q903;
            Q903=makeQuery(id+"F5.opExtrude","CAP_EDGE",EDGE,{"disambiguationData":[OSD([sQuery(id+"F4.wireOp",EDGE,"E6")])],"isStart":true});
            var Q904;
            Q904=makeQuery(id+"F5.opExtrude","CAP_EDGE",EDGE,{"disambiguationData":[OSD([sQuery(id+"F4.wireOp",EDGE,"E6")])],"isStart":true});
            var Q905;
            Q905=makeQuery(id+"F5.opExtrude","CAP_EDGE",EDGE,{"disambiguationData":[OSD([sQuery(id+"F4.wireOp",EDGE,"E6")])],"isStart":true});
            var Q906;
            Q906=makeQuery(id+"F5.opExtrude","CAP_EDGE",EDGE,{"disambiguationData":[OSD([sQuery(id+"F4.wireOp",EDGE,"E6")])],"isStart":true});
            var Q907;
            Q907=makeQuery(id+"F5.opExtrude","CAP_EDGE",EDGE,{"disambiguationData":[OSD([sQuery(id+"F4.wireOp",EDGE,"E6")])],"isStart":true});
            var Q908;
            Q908=makeQuery(id+"F5.opExtrude","CAP_EDGE",EDGE,{"disambiguationData":[OSD([sQuery(id+"F4.wireOp",EDGE,"E6")])],"isStart":true});
            var Q909;
            Q909=makeQuery(id+"F5.opExtrude","CAP_EDGE",EDGE,{"disambiguationData":[OSD([sQuery(id+"F4.wireOp",EDGE,"E6")])],"isStart":true});
            var Q910;
            Q910=makeQuery(id+"F5.opExtrude","CAP_EDGE",EDGE,{"disambiguationData":[OSD([sQuery(id+"F4.wireOp",EDGE,"E6")])],"isStart":true});
            var Q911;
            Q911=makeQuery(id+"F5.opExtrude","CAP_EDGE",EDGE,{"disambiguationData":[OSD([sQuery(id+"F4.wireOp",EDGE,"E6")])],"isStart":true});
            var Q912;
            Q912=makeQuery(id+"F5.opExtrude","CAP_EDGE",EDGE,{"disambiguationData":[OSD([sQuery(id+"F4.wireOp",EDGE,"E6")])],"isStart":true});
            var Q913;
            Q913=makeQuery(id+"F5.opExtrude","CAP_EDGE",EDGE,{"disambiguationData":[OSD([sQuery(id+"F4.wireOp",EDGE,"E6")])],"isStart":true});
            var Q914;
            Q914=makeQuery(id+"F5.opExtrude","CAP_EDGE",EDGE,{"disambiguationData":[OSD([sQuery(id+"F4.wireOp",EDGE,"E6")])],"isStart":true});
            var Q915;
            Q915=makeQuery(id+"F5.opExtrude","CAP_EDGE",EDGE,{"disambiguationData":[OSD([sQuery(id+"F4.wireOp",EDGE,"E6")])],"isStart":true});
            var Q916;
            Q916=makeQuery(id+"F5.opExtrude","CAP_EDGE",EDGE,{"disambiguationData":[OSD([sQuery(id+"F4.wireOp",EDGE,"E6")])],"isStart":true});
            var Q917;
            Q917=makeQuery(id+"F5.opExtrude","CAP_EDGE",EDGE,{"disambiguationData":[OSD([sQuery(id+"F4.wireOp",EDGE,"E6")])],"isStart":true});
            var Q918;
            Q918=makeQuery(id+"F5.opExtrude","CAP_EDGE",EDGE,{"disambiguationData":[OSD([sQuery(id+"F4.wireOp",EDGE,"E6")])],"isStart":true});
            var Q919;
            Q919=makeQuery(id+"F5.opExtrude","CAP_EDGE",EDGE,{"disambiguationData":[OSD([sQuery(id+"F4.wireOp",EDGE,"E6")])],"isStart":true});
            var Q920;
            Q920=makeQuery(id+"F5.opExtrude","CAP_EDGE",EDGE,{"disambiguationData":[OSD([sQuery(id+"F4.wireOp",EDGE,"E6")])],"isStart":true});
            var Q921;
            Q921=makeQuery(id+"F5.opExtrude","CAP_EDGE",EDGE,{"disambiguationData":[OSD([sQuery(id+"F4.wireOp",EDGE,"E6")])],"isStart":true});
            var Q922;
            Q922=makeQuery(id+"F5.opExtrude","CAP_EDGE",EDGE,{"disambiguationData":[OSD([sQuery(id+"F4.wireOp",EDGE,"E6")])],"isStart":true});
            var Q923;
            Q923=makeQuery(id+"F5.opExtrude","CAP_EDGE",EDGE,{"disambiguationData":[OSD([sQuery(id+"F4.wireOp",EDGE,"E6")])],"isStart":true});
            var Q924;
            Q924=makeQuery(id+"F5.opExtrude","CAP_EDGE",EDGE,{"disambiguationData":[OSD([sQuery(id+"F4.wireOp",EDGE,"E6")])],"isStart":true});
            var Q925;
            Q925=makeQuery(id+"F5.opExtrude","CAP_EDGE",EDGE,{"disambiguationData":[OSD([sQuery(id+"F4.wireOp",EDGE,"E6")])],"isStart":true});
            var Q926;
            Q926=makeQuery(id+"F5.opExtrude","CAP_EDGE",EDGE,{"disambiguationData":[OSD([sQuery(id+"F4.wireOp",EDGE,"E6")])],"isStart":true});
            var Q927;
            Q927=makeQuery(id+"F5.opExtrude","CAP_EDGE",EDGE,{"disambiguationData":[OSD([sQuery(id+"F4.wireOp",EDGE,"E6")])],"isStart":true});
            var Q928;
            Q928=makeQuery(id+"F5.opExtrude","CAP_EDGE",EDGE,{"disambiguationData":[OSD([sQuery(id+"F4.wireOp",EDGE,"E6")])],"isStart":true});
            var Q929;
            Q929=makeQuery(id+"F5.opExtrude","CAP_EDGE",EDGE,{"disambiguationData":[OSD([sQuery(id+"F4.wireOp",EDGE,"E6")])],"isStart":true});
            var Q930;
            Q930=makeQuery(id+"F5.opExtrude","CAP_EDGE",EDGE,{"disambiguationData":[OSD([sQuery(id+"F4.wireOp",EDGE,"E6")])],"isStart":true});
            var Q931;
            Q931=makeQuery(id+"F5.opExtrude","CAP_EDGE",EDGE,{"disambiguationData":[OSD([sQuery(id+"F4.wireOp",EDGE,"E6")])],"isStart":true});
            var Q932;
            Q932=makeQuery(id+"F5.opExtrude","CAP_EDGE",EDGE,{"disambiguationData":[OSD([sQuery(id+"F4.wireOp",EDGE,"E6")])],"isStart":true});
            var Q933;
            Q933=makeQuery(id+"F5.opExtrude","CAP_EDGE",EDGE,{"disambiguationData":[OSD([sQuery(id+"F4.wireOp",EDGE,"E6")])],"isStart":true});
            var Q934;
            Q934=makeQuery(id+"F5.opExtrude","CAP_EDGE",EDGE,{"disambiguationData":[OSD([sQuery(id+"F4.wireOp",EDGE,"E6")])],"isStart":true});
            var Q935;
            Q935=makeQuery(id+"F5.opExtrude","CAP_EDGE",EDGE,{"disambiguationData":[OSD([sQuery(id+"F4.wireOp",EDGE,"E6")])],"isStart":true});
            var Q936;
            Q936=makeQuery(id+"F5.opExtrude","CAP_EDGE",EDGE,{"disambiguationData":[OSD([sQuery(id+"F4.wireOp",EDGE,"E6")])],"isStart":true});
            var Q937;
            Q937=makeQuery(id+"F5.opExtrude","CAP_EDGE",EDGE,{"disambiguationData":[OSD([sQuery(id+"F4.wireOp",EDGE,"E6")])],"isStart":true});
            var Q938;
            Q938=makeQuery(id+"F5.opExtrude","CAP_EDGE",EDGE,{"disambiguationData":[OSD([sQuery(id+"F4.wireOp",EDGE,"E6")])],"isStart":true});
            var Q939;
            Q939=makeQuery(id+"F5.opExtrude","CAP_EDGE",EDGE,{"disambiguationData":[OSD([sQuery(id+"F4.wireOp",EDGE,"E6")])],"isStart":true});
            var Q940;
            Q940=makeQuery(id+"F5.opExtrude","CAP_EDGE",EDGE,{"disambiguationData":[OSD([sQuery(id+"F4.wireOp",EDGE,"E6")])],"isStart":true});
            var Q941;
            Q941=makeQuery(id+"F5.opExtrude","CAP_EDGE",EDGE,{"disambiguationData":[OSD([sQuery(id+"F4.wireOp",EDGE,"E6")])],"isStart":true});
            var Q942;
            Q942=makeQuery(id+"F5.opExtrude","CAP_EDGE",EDGE,{"disambiguationData":[OSD([sQuery(id+"F4.wireOp",EDGE,"E6")])],"isStart":true});
            var Q943;
            Q943=makeQuery(id+"F5.opExtrude","CAP_EDGE",EDGE,{"disambiguationData":[OSD([sQuery(id+"F4.wireOp",EDGE,"E6")])],"isStart":true});
            var Q944;
            Q944=makeQuery(id+"F5.opExtrude","CAP_EDGE",EDGE,{"disambiguationData":[OSD([sQuery(id+"F4.wireOp",EDGE,"E6")])],"isStart":true});
            var Q945;
            Q945=makeQuery(id+"F5.opExtrude","CAP_EDGE",EDGE,{"disambiguationData":[OSD([sQuery(id+"F4.wireOp",EDGE,"E6")])],"isStart":true});
            var Q946;
            Q946=makeQuery(id+"F5.opExtrude","CAP_EDGE",EDGE,{"disambiguationData":[OSD([sQuery(id+"F4.wireOp",EDGE,"E6")])],"isStart":true});
            var Q947;
            Q947=makeQuery(id+"F5.opExtrude","CAP_EDGE",EDGE,{"disambiguationData":[OSD([sQuery(id+"F4.wireOp",EDGE,"E6")])],"isStart":true});
            var Q948;
            Q948=makeQuery(id+"F5.opExtrude","CAP_EDGE",EDGE,{"disambiguationData":[OSD([sQuery(id+"F4.wireOp",EDGE,"E6")])],"isStart":true});
            var Q949;
            Q949=makeQuery(id+"F5.opExtrude","CAP_EDGE",EDGE,{"disambiguationData":[OSD([sQuery(id+"F4.wireOp",EDGE,"E6")])],"isStart":true});
            var Q950;
            Q950=makeQuery(id+"F5.opExtrude","CAP_EDGE",EDGE,{"disambiguationData":[OSD([sQuery(id+"F4.wireOp",EDGE,"E6")])],"isStart":true});
            var Q951;
            Q951=makeQuery(id+"F5.opExtrude","CAP_EDGE",EDGE,{"disambiguationData":[OSD([sQuery(id+"F4.wireOp",EDGE,"E6")])],"isStart":true});
            var Q952;
            Q952=makeQuery(id+"F5.opExtrude","CAP_EDGE",EDGE,{"disambiguationData":[OSD([sQuery(id+"F4.wireOp",EDGE,"E6")])],"isStart":true});
            var Q953;
            Q953=makeQuery(id+"F5.opExtrude","CAP_EDGE",EDGE,{"disambiguationData":[OSD([sQuery(id+"F4.wireOp",EDGE,"E6")])],"isStart":true});
            var Q954;
            Q954=makeQuery(id+"F5.opExtrude","CAP_EDGE",EDGE,{"disambiguationData":[OSD([sQuery(id+"F4.wireOp",EDGE,"E6")])],"isStart":true});
            var Q955;
            Q955=makeQuery(id+"F5.opExtrude","CAP_EDGE",EDGE,{"disambiguationData":[OSD([sQuery(id+"F4.wireOp",EDGE,"E6")])],"isStart":true});
            var Q956;
            Q956=makeQuery(id+"F5.opExtrude","CAP_EDGE",EDGE,{"disambiguationData":[OSD([sQuery(id+"F4.wireOp",EDGE,"E6")])],"isStart":true});
            var Q957;
            Q957=makeQuery(id+"F5.opExtrude","CAP_EDGE",EDGE,{"disambiguationData":[OSD([sQuery(id+"F4.wireOp",EDGE,"E6")])],"isStart":true});
            var Q958;
            Q958=makeQuery(id+"F5.opExtrude","CAP_EDGE",EDGE,{"disambiguationData":[OSD([sQuery(id+"F4.wireOp",EDGE,"E6")])],"isStart":true});
            var Q959;
            Q959=makeQuery(id+"F5.opExtrude","CAP_EDGE",EDGE,{"disambiguationData":[OSD([sQuery(id+"F4.wireOp",EDGE,"E6")])],"isStart":true});
            var Q960;
            Q960=makeQuery(id+"F5.opExtrude","CAP_EDGE",EDGE,{"disambiguationData":[OSD([sQuery(id+"F4.wireOp",EDGE,"E6")])],"isStart":true});
            var Q961;
            Q961=makeQuery(id+"F5.opExtrude","CAP_EDGE",EDGE,{"disambiguationData":[OSD([sQuery(id+"F4.wireOp",EDGE,"E6")])],"isStart":true});
            var Q962;
            Q962=makeQuery(id+"F5.opExtrude","CAP_EDGE",EDGE,{"disambiguationData":[OSD([sQuery(id+"F4.wireOp",EDGE,"E6")])],"isStart":true});
            var Q963;
            Q963=makeQuery(id+"F5.opExtrude","CAP_EDGE",EDGE,{"disambiguationData":[OSD([sQuery(id+"F4.wireOp",EDGE,"E6")])],"isStart":true});
            var Q964;
            Q964=makeQuery(id+"F5.opExtrude","CAP_EDGE",EDGE,{"disambiguationData":[OSD([sQuery(id+"F4.wireOp",EDGE,"E6")])],"isStart":true});
            var Q965;
            Q965=makeQuery(id+"F5.opExtrude","CAP_EDGE",EDGE,{"disambiguationData":[OSD([sQuery(id+"F4.wireOp",EDGE,"E6")])],"isStart":true});
            var Q966;
            Q966=makeQuery(id+"F5.opExtrude","CAP_EDGE",EDGE,{"disambiguationData":[OSD([sQuery(id+"F4.wireOp",EDGE,"E6")])],"isStart":true});
            var Q967;
            Q967=makeQuery(id+"F5.opExtrude","CAP_EDGE",EDGE,{"disambiguationData":[OSD([sQuery(id+"F4.wireOp",EDGE,"E6")])],"isStart":true});
            var Q968;
            Q968=makeQuery(id+"F5.opExtrude","CAP_EDGE",EDGE,{"disambiguationData":[OSD([sQuery(id+"F4.wireOp",EDGE,"E6")])],"isStart":false});
            var Q969;
            Q969=makeQuery(id+"F5.opExtrude","CAP_EDGE",EDGE,{"disambiguationData":[OSD([sQuery(id+"F4.wireOp",EDGE,"E6")])],"isStart":false});
            var Q970;
            Q970=makeQuery(id+"F5.opExtrude","CAP_EDGE",EDGE,{"disambiguationData":[OSD([sQuery(id+"F4.wireOp",EDGE,"E6")])],"isStart":false});
            var Q971;
            Q971=makeQuery(id+"F5.opExtrude","CAP_EDGE",EDGE,{"disambiguationData":[OSD([sQuery(id+"F4.wireOp",EDGE,"E6")])],"isStart":false});
            var Q972;
            Q972=makeQuery(id+"F5.opExtrude","CAP_EDGE",EDGE,{"disambiguationData":[OSD([sQuery(id+"F4.wireOp",EDGE,"E6")])],"isStart":false});
            var Q973;
            Q973=makeQuery(id+"F5.opExtrude","CAP_EDGE",EDGE,{"disambiguationData":[OSD([sQuery(id+"F4.wireOp",EDGE,"E6")])],"isStart":false});
            var Q974;
            Q974=makeQuery(id+"F5.opExtrude","CAP_EDGE",EDGE,{"disambiguationData":[OSD([sQuery(id+"F4.wireOp",EDGE,"E6")])],"isStart":false});
            var Q975;
            Q975=makeQuery(id+"F5.opExtrude","CAP_EDGE",EDGE,{"disambiguationData":[OSD([sQuery(id+"F4.wireOp",EDGE,"E6")])],"isStart":false});
            var Q976;
            Q976=makeQuery(id+"F5.opExtrude","CAP_EDGE",EDGE,{"disambiguationData":[OSD([sQuery(id+"F4.wireOp",EDGE,"E6")])],"isStart":false});
            var Q977;
            Q977=makeQuery(id+"F5.opExtrude","CAP_EDGE",EDGE,{"disambiguationData":[OSD([sQuery(id+"F4.wireOp",EDGE,"E6")])],"isStart":false});
            var Q978;
            Q978=makeQuery(id+"F5.opExtrude","CAP_EDGE",EDGE,{"disambiguationData":[OSD([sQuery(id+"F4.wireOp",EDGE,"E6")])],"isStart":false});
            var Q979;
            Q979=makeQuery(id+"F5.opExtrude","CAP_EDGE",EDGE,{"disambiguationData":[OSD([sQuery(id+"F4.wireOp",EDGE,"E6")])],"isStart":false});
            var Q980;
            Q980=makeQuery(id+"F5.opExtrude","CAP_EDGE",EDGE,{"disambiguationData":[OSD([sQuery(id+"F4.wireOp",EDGE,"E6")])],"isStart":false});
            var Q981;
            Q981=makeQuery(id+"F5.opExtrude","CAP_EDGE",EDGE,{"disambiguationData":[OSD([sQuery(id+"F4.wireOp",EDGE,"E6")])],"isStart":false});
            var Q982;
            Q982=makeQuery(id+"F5.opExtrude","CAP_EDGE",EDGE,{"disambiguationData":[OSD([sQuery(id+"F4.wireOp",EDGE,"E6")])],"isStart":false});
            var Q983;
            Q983=makeQuery(id+"F5.opExtrude","CAP_EDGE",EDGE,{"disambiguationData":[OSD([sQuery(id+"F4.wireOp",EDGE,"E6")])],"isStart":false});
            var Q984;
            Q984=makeQuery(id+"F5.opExtrude","CAP_EDGE",EDGE,{"disambiguationData":[OSD([sQuery(id+"F4.wireOp",EDGE,"E6")])],"isStart":false});
            var Q985;
            Q985=makeQuery(id+"F5.opExtrude","CAP_EDGE",EDGE,{"disambiguationData":[OSD([sQuery(id+"F4.wireOp",EDGE,"E6")])],"isStart":false});
            var Q986;
            Q986=makeQuery(id+"F5.opExtrude","CAP_EDGE",EDGE,{"disambiguationData":[OSD([sQuery(id+"F4.wireOp",EDGE,"E6")])],"isStart":false});
            var Q987;
            Q987=makeQuery(id+"F5.opExtrude","CAP_EDGE",EDGE,{"disambiguationData":[OSD([sQuery(id+"F4.wireOp",EDGE,"E6")])],"isStart":false});
            var Q988;
            Q988=makeQuery(id+"F5.opExtrude","CAP_EDGE",EDGE,{"disambiguationData":[OSD([sQuery(id+"F4.wireOp",EDGE,"E6")])],"isStart":false});
            var Q989;
            Q989=makeQuery(id+"F5.opExtrude","CAP_EDGE",EDGE,{"disambiguationData":[OSD([sQuery(id+"F4.wireOp",EDGE,"E6")])],"isStart":false});
            var Q990;
            Q990=makeQuery(id+"F5.opExtrude","CAP_EDGE",EDGE,{"disambiguationData":[OSD([sQuery(id+"F4.wireOp",EDGE,"E6")])],"isStart":false});
            var Q991;
            Q991=makeQuery(id+"F5.opExtrude","CAP_EDGE",EDGE,{"disambiguationData":[OSD([sQuery(id+"F4.wireOp",EDGE,"E6")])],"isStart":false});
            var Q992;
            Q992=makeQuery(id+"F5.opExtrude","CAP_EDGE",EDGE,{"disambiguationData":[OSD([sQuery(id+"F4.wireOp",EDGE,"E6")])],"isStart":false});
            var Q993;
            Q993=makeQuery(id+"F5.opExtrude","CAP_EDGE",EDGE,{"disambiguationData":[OSD([sQuery(id+"F4.wireOp",EDGE,"E6")])],"isStart":false});
            var Q994;
            Q994=makeQuery(id+"F5.opExtrude","CAP_EDGE",EDGE,{"disambiguationData":[OSD([sQuery(id+"F4.wireOp",EDGE,"E6")])],"isStart":false});
            var Q995;
            Q995=makeQuery(id+"F5.opExtrude","CAP_EDGE",EDGE,{"disambiguationData":[OSD([sQuery(id+"F4.wireOp",EDGE,"E6")])],"isStart":false});
            var Q996;
            Q996=makeQuery(id+"F5.opExtrude","CAP_EDGE",EDGE,{"disambiguationData":[OSD([sQuery(id+"F4.wireOp",EDGE,"E6")])],"isStart":false});
            var Q997;
            Q997=makeQuery(id+"F5.opExtrude","CAP_EDGE",EDGE,{"disambiguationData":[OSD([sQuery(id+"F4.wireOp",EDGE,"E6")])],"isStart":false});
            var Q998;
            Q998=makeQuery(id+"F5.opExtrude","CAP_EDGE",EDGE,{"disambiguationData":[OSD([sQuery(id+"F4.wireOp",EDGE,"E6")])],"isStart":false});
            var Q999;
            Q999=makeQuery(id+"F5.opExtrude","CAP_EDGE",EDGE,{"disambiguationData":[OSD([sQuery(id+"F4.wireOp",EDGE,"E6")])],"isStart":false});
            var Q1000;
            Q1000=makeQuery(id+"F5.opExtrude","CAP_EDGE",EDGE,{"disambiguationData":[OSD([sQuery(id+"F4.wireOp",EDGE,"E6")])],"isStart":false});
            var Q1001;
            Q1001=makeQuery(id+"F5.opExtrude","CAP_EDGE",EDGE,{"disambiguationData":[OSD([sQuery(id+"F4.wireOp",EDGE,"E6")])],"isStart":false});
            var Q1002;
            Q1002=makeQuery(id+"F5.opExtrude","CAP_EDGE",EDGE,{"disambiguationData":[OSD([sQuery(id+"F4.wireOp",EDGE,"E6")])],"isStart":false});
            var Q1003;
            Q1003=makeQuery(id+"F5.opExtrude","CAP_EDGE",EDGE,{"disambiguationData":[OSD([sQuery(id+"F4.wireOp",EDGE,"E6")])],"isStart":false});
            var Q1004;
            Q1004=makeQuery(id+"F5.opExtrude","CAP_EDGE",EDGE,{"disambiguationData":[OSD([sQuery(id+"F4.wireOp",EDGE,"E6")])],"isStart":false});
            var Q1005;
            Q1005=makeQuery(id+"F5.opExtrude","CAP_EDGE",EDGE,{"disambiguationData":[OSD([sQuery(id+"F4.wireOp",EDGE,"E6")])],"isStart":false});
            var Q1006;
            Q1006=makeQuery(id+"F5.opExtrude","CAP_EDGE",EDGE,{"disambiguationData":[OSD([sQuery(id+"F4.wireOp",EDGE,"E6")])],"isStart":false});
            var Q1007;
            Q1007=makeQuery(id+"F5.opExtrude","CAP_EDGE",EDGE,{"disambiguationData":[OSD([sQuery(id+"F4.wireOp",EDGE,"E6")])],"isStart":false});
            var Q1008;
            Q1008=makeQuery(id+"F5.opExtrude","CAP_EDGE",EDGE,{"disambiguationData":[OSD([sQuery(id+"F4.wireOp",EDGE,"E6")])],"isStart":false});
            var Q1009;
            Q1009=makeQuery(id+"F5.opExtrude","CAP_EDGE",EDGE,{"disambiguationData":[OSD([sQuery(id+"F4.wireOp",EDGE,"E6")])],"isStart":false});
            var Q1010;
            Q1010=makeQuery(id+"F5.opExtrude","CAP_EDGE",EDGE,{"disambiguationData":[OSD([sQuery(id+"F4.wireOp",EDGE,"E6")])],"isStart":false});
            var Q1011;
            Q1011=makeQuery(id+"F5.opExtrude","CAP_EDGE",EDGE,{"disambiguationData":[OSD([sQuery(id+"F4.wireOp",EDGE,"E6")])],"isStart":false});
            var Q1012;
            Q1012=makeQuery(id+"F5.opExtrude","CAP_EDGE",EDGE,{"disambiguationData":[OSD([sQuery(id+"F4.wireOp",EDGE,"E6")])],"isStart":false});
            var Q1013;
            Q1013=makeQuery(id+"F5.opExtrude","CAP_EDGE",EDGE,{"disambiguationData":[OSD([sQuery(id+"F4.wireOp",EDGE,"E6")])],"isStart":false});
            var Q1014;
            Q1014=makeQuery(id+"F5.opExtrude","CAP_EDGE",EDGE,{"disambiguationData":[OSD([sQuery(id+"F4.wireOp",EDGE,"E6")])],"isStart":false});
            var Q1015;
            Q1015=makeQuery(id+"F5.opExtrude","CAP_EDGE",EDGE,{"disambiguationData":[OSD([sQuery(id+"F4.wireOp",EDGE,"E6")])],"isStart":false});
            var Q1016;
            Q1016=makeQuery(id+"F5.opExtrude","CAP_EDGE",EDGE,{"disambiguationData":[OSD([sQuery(id+"F4.wireOp",EDGE,"E6")])],"isStart":false});
            var Q1017;
            Q1017=makeQuery(id+"F5.opExtrude","CAP_EDGE",EDGE,{"disambiguationData":[OSD([sQuery(id+"F4.wireOp",EDGE,"E6")])],"isStart":false});
            var Q1018;
            Q1018=makeQuery(id+"F5.opExtrude","CAP_EDGE",EDGE,{"disambiguationData":[OSD([sQuery(id+"F4.wireOp",EDGE,"E6")])],"isStart":false});
            var Q1019;
            Q1019=makeQuery(id+"F5.opExtrude","CAP_EDGE",EDGE,{"disambiguationData":[OSD([sQuery(id+"F4.wireOp",EDGE,"E6")])],"isStart":false});
            var Q1020;
            Q1020=makeQuery(id+"F5.opExtrude","CAP_EDGE",EDGE,{"disambiguationData":[OSD([sQuery(id+"F4.wireOp",EDGE,"E6")])],"isStart":false});
            var Q1021;
            Q1021=makeQuery(id+"F5.opExtrude","CAP_EDGE",EDGE,{"disambiguationData":[OSD([sQuery(id+"F4.wireOp",EDGE,"E6")])],"isStart":false});
            var Q1022;
            Q1022=makeQuery(id+"F5.opExtrude","CAP_EDGE",EDGE,{"disambiguationData":[OSD([sQuery(id+"F4.wireOp",EDGE,"E6")])],"isStart":false});
            var Q1023;
            Q1023=makeQuery(id+"F5.opExtrude","CAP_EDGE",EDGE,{"disambiguationData":[OSD([sQuery(id+"F4.wireOp",EDGE,"E6")])],"isStart":false});
            var Q1024;
            Q1024=makeQuery(id+"F5.opExtrude","CAP_EDGE",EDGE,{"disambiguationData":[OSD([sQuery(id+"F4.wireOp",EDGE,"E6")])],"isStart":false});
            var Q1025;
            Q1025=makeQuery(id+"F5.opExtrude","CAP_EDGE",EDGE,{"disambiguationData":[OSD([sQuery(id+"F4.wireOp",EDGE,"E6")])],"isStart":false});
            var Q1026;
            Q1026=makeQuery(id+"F5.opExtrude","CAP_EDGE",EDGE,{"disambiguationData":[OSD([sQuery(id+"F4.wireOp",EDGE,"E6")])],"isStart":false});
            var Q1027;
            Q1027=makeQuery(id+"F5.opExtrude","CAP_EDGE",EDGE,{"disambiguationData":[OSD([sQuery(id+"F4.wireOp",EDGE,"E6")])],"isStart":false});
            var Q1028;
            Q1028=makeQuery(id+"F5.opExtrude","CAP_EDGE",EDGE,{"disambiguationData":[OSD([sQuery(id+"F4.wireOp",EDGE,"E6")])],"isStart":false});
            var Q1029;
            Q1029=makeQuery(id+"F5.opExtrude","CAP_EDGE",EDGE,{"disambiguationData":[OSD([sQuery(id+"F4.wireOp",EDGE,"E6")])],"isStart":false});
            var Q1030;
            Q1030=makeQuery(id+"F5.opExtrude","CAP_EDGE",EDGE,{"disambiguationData":[OSD([sQuery(id+"F4.wireOp",EDGE,"E6")])],"isStart":false});
            var Q1031;
            Q1031=makeQuery(id+"F5.opExtrude","CAP_EDGE",EDGE,{"disambiguationData":[OSD([sQuery(id+"F4.wireOp",EDGE,"E6")])],"isStart":false});
            var Q1032;
            Q1032=makeQuery(id+"F5.opExtrude","CAP_EDGE",EDGE,{"disambiguationData":[OSD([sQuery(id+"F4.wireOp",EDGE,"E6")])],"isStart":false});
            var Q1033;
            Q1033=makeQuery(id+"F5.opExtrude","CAP_EDGE",EDGE,{"disambiguationData":[OSD([sQuery(id+"F4.wireOp",EDGE,"E6")])],"isStart":false});
            var Q1034;
            Q1034=makeQuery(id+"F5.opExtrude","CAP_EDGE",EDGE,{"disambiguationData":[OSD([sQuery(id+"F4.wireOp",EDGE,"E6")])],"isStart":false});
            var Q1035;
            Q1035=makeQuery(id+"F5.opExtrude","CAP_EDGE",EDGE,{"disambiguationData":[OSD([sQuery(id+"F4.wireOp",EDGE,"E6")])],"isStart":false});
            var Q1036;
            Q1036=makeQuery(id+"F5.opExtrude","CAP_EDGE",EDGE,{"disambiguationData":[OSD([sQuery(id+"F4.wireOp",EDGE,"E6")])],"isStart":false});
            var Q1037;
            Q1037=makeQuery(id+"F5.opExtrude","CAP_EDGE",EDGE,{"disambiguationData":[OSD([sQuery(id+"F4.wireOp",EDGE,"E6")])],"isStart":false});
            var Q1038;
            Q1038=makeQuery(id+"F5.opExtrude","CAP_EDGE",EDGE,{"disambiguationData":[OSD([sQuery(id+"F4.wireOp",EDGE,"E6")])],"isStart":false});
            var Q1039;
            Q1039=makeQuery(id+"F5.opExtrude","CAP_EDGE",EDGE,{"disambiguationData":[OSD([sQuery(id+"F4.wireOp",EDGE,"E6")])],"isStart":false});
            var Q1040;
            Q1040=makeQuery(id+"F5.opExtrude","CAP_EDGE",EDGE,{"disambiguationData":[OSD([sQuery(id+"F4.wireOp",EDGE,"E6")])],"isStart":false});
            var Q1041;
            Q1041=makeQuery(id+"F5.opExtrude","CAP_EDGE",EDGE,{"disambiguationData":[OSD([sQuery(id+"F4.wireOp",EDGE,"E6")])],"isStart":false});
            var Q1042;
            Q1042=makeQuery(id+"F5.opExtrude","CAP_EDGE",EDGE,{"disambiguationData":[OSD([sQuery(id+"F4.wireOp",EDGE,"E6")])],"isStart":false});
            var Q1043;
            Q1043=makeQuery(id+"F5.opExtrude","CAP_EDGE",EDGE,{"disambiguationData":[OSD([sQuery(id+"F4.wireOp",EDGE,"E6")])],"isStart":false});
            var Q1044;
            Q1044=makeQuery(id+"F5.opExtrude","CAP_EDGE",EDGE,{"disambiguationData":[OSD([sQuery(id+"F4.wireOp",EDGE,"E6")])],"isStart":false});
            var Q1045;
            Q1045=makeQuery(id+"F5.opExtrude","CAP_EDGE",EDGE,{"disambiguationData":[OSD([sQuery(id+"F4.wireOp",EDGE,"E6")])],"isStart":false});
            var Q1046;
            Q1046=makeQuery(id+"F5.opExtrude","CAP_EDGE",EDGE,{"disambiguationData":[OSD([sQuery(id+"F4.wireOp",EDGE,"E6")])],"isStart":false});
            var Q1047;
            Q1047=makeQuery(id+"F5.opExtrude","CAP_EDGE",EDGE,{"disambiguationData":[OSD([sQuery(id+"F4.wireOp",EDGE,"E6")])],"isStart":false});
            var Q1048;
            Q1048=makeQuery(id+"F5.opExtrude","CAP_EDGE",EDGE,{"disambiguationData":[OSD([sQuery(id+"F4.wireOp",EDGE,"E6")])],"isStart":false});
            var Q1049;
            Q1049=makeQuery(id+"F5.opExtrude","CAP_EDGE",EDGE,{"disambiguationData":[OSD([sQuery(id+"F4.wireOp",EDGE,"E6")])],"isStart":false});
            var Q1050;
            Q1050=makeQuery(id+"F5.opExtrude","CAP_EDGE",EDGE,{"disambiguationData":[OSD([sQuery(id+"F4.wireOp",EDGE,"E6")])],"isStart":false});
            var Q1051;
            Q1051=makeQuery(id+"F5.opExtrude","CAP_EDGE",EDGE,{"disambiguationData":[OSD([sQuery(id+"F4.wireOp",EDGE,"E6")])],"isStart":false});
            var Q1052;
            Q1052=makeQuery(id+"F5.opExtrude","CAP_EDGE",EDGE,{"disambiguationData":[OSD([sQuery(id+"F4.wireOp",EDGE,"E6")])],"isStart":false});
            var Q1053;
            Q1053=makeQuery(id+"F5.opExtrude","CAP_EDGE",EDGE,{"disambiguationData":[OSD([sQuery(id+"F4.wireOp",EDGE,"E6")])],"isStart":false});
            var Q1054;
            Q1054=makeQuery(id+"F5.opExtrude","CAP_EDGE",EDGE,{"disambiguationData":[OSD([sQuery(id+"F4.wireOp",EDGE,"E6")])],"isStart":false});
            var Q1055;
            Q1055=makeQuery(id+"F5.opExtrude","CAP_EDGE",EDGE,{"disambiguationData":[OSD([sQuery(id+"F4.wireOp",EDGE,"E6")])],"isStart":false});
            var Q1056;
            Q1056=makeQuery(id+"F5.opExtrude","CAP_EDGE",EDGE,{"disambiguationData":[OSD([sQuery(id+"F4.wireOp",EDGE,"E6")])],"isStart":false});
            var Q1057;
            Q1057=makeQuery(id+"F5.opExtrude","CAP_EDGE",EDGE,{"disambiguationData":[OSD([sQuery(id+"F4.wireOp",EDGE,"E6")])],"isStart":false});
            var Q1058;
            Q1058=makeQuery(id+"F5.opExtrude","CAP_EDGE",EDGE,{"disambiguationData":[OSD([sQuery(id+"F4.wireOp",EDGE,"E6")])],"isStart":false});
            var Q1059;
            Q1059=makeQuery(id+"F5.opExtrude","CAP_EDGE",EDGE,{"disambiguationData":[OSD([sQuery(id+"F4.wireOp",EDGE,"E6")])],"isStart":false});
            var Q1060;
            Q1060=makeQuery(id+"F5.opExtrude","CAP_EDGE",EDGE,{"disambiguationData":[OSD([sQuery(id+"F4.wireOp",EDGE,"E6")])],"isStart":false});
            var Q1061;
            Q1061=makeQuery(id+"F5.opExtrude","CAP_EDGE",EDGE,{"disambiguationData":[OSD([sQuery(id+"F4.wireOp",EDGE,"E6")])],"isStart":false});
            var Q1062;
            Q1062=makeQuery(id+"F5.opExtrude","CAP_EDGE",EDGE,{"disambiguationData":[OSD([sQuery(id+"F4.wireOp",EDGE,"E6")])],"isStart":false});
            var Q1063;
            Q1063=makeQuery(id+"F5.opExtrude","CAP_EDGE",EDGE,{"disambiguationData":[OSD([sQuery(id+"F4.wireOp",EDGE,"E6")])],"isStart":false});
            var Q1064;
            Q1064=makeQuery(id+"F5.opExtrude","CAP_EDGE",EDGE,{"disambiguationData":[OSD([sQuery(id+"F4.wireOp",EDGE,"E6")])],"isStart":false});
            var Q1065;
            Q1065=makeQuery(id+"F5.opExtrude","CAP_EDGE",EDGE,{"disambiguationData":[OSD([sQuery(id+"F4.wireOp",EDGE,"E6")])],"isStart":false});
            var Q1066;
            Q1066=makeQuery(id+"F5.opExtrude","CAP_EDGE",EDGE,{"disambiguationData":[OSD([sQuery(id+"F4.wireOp",EDGE,"E6")])],"isStart":false});
            var Q1067;
            Q1067=makeQuery(id+"F5.opExtrude","CAP_EDGE",EDGE,{"disambiguationData":[OSD([sQuery(id+"F4.wireOp",EDGE,"E6")])],"isStart":false});
            var Q1068;
            Q1068=makeQuery(id+"F5.opExtrude","CAP_EDGE",EDGE,{"disambiguationData":[OSD([sQuery(id+"F4.wireOp",EDGE,"E6")])],"isStart":false});
            var Q1069;
            Q1069=makeQuery(id+"F5.opExtrude","CAP_EDGE",EDGE,{"disambiguationData":[OSD([sQuery(id+"F4.wireOp",EDGE,"E6")])],"isStart":false});
            var Q1070;
            Q1070=makeQuery(id+"F5.opExtrude","CAP_EDGE",EDGE,{"disambiguationData":[OSD([sQuery(id+"F4.wireOp",EDGE,"E6")])],"isStart":false});
            var Q1071;
            Q1071=makeQuery(id+"F5.opExtrude","CAP_EDGE",EDGE,{"disambiguationData":[OSD([sQuery(id+"F4.wireOp",EDGE,"E6")])],"isStart":false});
            var Q1072;
            Q1072=makeQuery(id+"F5.opExtrude","CAP_EDGE",EDGE,{"disambiguationData":[OSD([sQuery(id+"F4.wireOp",EDGE,"E6")])],"isStart":false});
            var Q1073;
            Q1073=makeQuery(id+"F5.opExtrude","CAP_EDGE",EDGE,{"disambiguationData":[OSD([sQuery(id+"F4.wireOp",EDGE,"E6")])],"isStart":false});
            var Q1074;
            Q1074=makeQuery(id+"F5.opExtrude","CAP_EDGE",EDGE,{"disambiguationData":[OSD([sQuery(id+"F4.wireOp",EDGE,"E6")])],"isStart":false});
            var Q1075;
            Q1075=makeQuery(id+"F5.opExtrude","CAP_EDGE",EDGE,{"disambiguationData":[OSD([sQuery(id+"F4.wireOp",EDGE,"E6")])],"isStart":false});
            var Q1076;
            Q1076=makeQuery(id+"F5.opExtrude","CAP_EDGE",EDGE,{"disambiguationData":[OSD([sQuery(id+"F4.wireOp",EDGE,"E6")])],"isStart":false});
            var Q1077;
            Q1077=makeQuery(id+"F5.opExtrude","CAP_EDGE",EDGE,{"disambiguationData":[OSD([sQuery(id+"F4.wireOp",EDGE,"E6")])],"isStart":false});
            var Q1078;
            Q1078=makeQuery(id+"F5.opExtrude","CAP_EDGE",EDGE,{"disambiguationData":[OSD([sQuery(id+"F4.wireOp",EDGE,"E6")])],"isStart":false});
            var Q1079;
            Q1079=makeQuery(id+"F5.opExtrude","CAP_EDGE",EDGE,{"disambiguationData":[OSD([sQuery(id+"F4.wireOp",EDGE,"E6")])],"isStart":false});
            var Q1080;
            Q1080=makeQuery(id+"F5.opExtrude","CAP_EDGE",EDGE,{"disambiguationData":[OSD([sQuery(id+"F4.wireOp",EDGE,"E6")])],"isStart":false});
            var Q1081;
            Q1081=makeQuery(id+"F5.opExtrude","CAP_EDGE",EDGE,{"disambiguationData":[OSD([sQuery(id+"F4.wireOp",EDGE,"E6")])],"isStart":false});
            var Q1082;
            Q1082=makeQuery(id+"F5.opExtrude","CAP_EDGE",EDGE,{"disambiguationData":[OSD([sQuery(id+"F4.wireOp",EDGE,"E6")])],"isStart":false});
            var Q1083;
            Q1083=makeQuery(id+"F5.opExtrude","CAP_EDGE",EDGE,{"disambiguationData":[OSD([sQuery(id+"F4.wireOp",EDGE,"E6")])],"isStart":false});
            var Q1084;
            Q1084=makeQuery(id+"F5.opExtrude","CAP_EDGE",EDGE,{"disambiguationData":[OSD([sQuery(id+"F4.wireOp",EDGE,"E6")])],"isStart":false});
            var Q1085;
            Q1085=makeQuery(id+"F5.opExtrude","CAP_EDGE",EDGE,{"disambiguationData":[OSD([sQuery(id+"F4.wireOp",EDGE,"E6")])],"isStart":false});
            var Q1086;
            Q1086=makeQuery(id+"F5.opExtrude","CAP_EDGE",EDGE,{"disambiguationData":[OSD([sQuery(id+"F4.wireOp",EDGE,"E6")])],"isStart":false});
            var Q1087;
            Q1087=makeQuery(id+"F5.opExtrude","CAP_EDGE",EDGE,{"disambiguationData":[OSD([sQuery(id+"F4.wireOp",EDGE,"E6")])],"isStart":false});
            var Q1088;
            Q1088=makeQuery(id+"F5.opExtrude","CAP_EDGE",EDGE,{"disambiguationData":[OSD([sQuery(id+"F4.wireOp",EDGE,"E6")])],"isStart":false});
            var Q1089;
            Q1089=makeQuery(id+"F5.opExtrude","CAP_EDGE",EDGE,{"disambiguationData":[OSD([sQuery(id+"F4.wireOp",EDGE,"E6")])],"isStart":false});
            var Q1090;
            Q1090=makeQuery(id+"F5.opExtrude","CAP_EDGE",EDGE,{"disambiguationData":[OSD([sQuery(id+"F4.wireOp",EDGE,"E6")])],"isStart":false});
            var Q1091;
            Q1091=makeQuery(id+"F5.opExtrude","CAP_EDGE",EDGE,{"disambiguationData":[OSD([sQuery(id+"F4.wireOp",EDGE,"E6")])],"isStart":false});
            var Q1092;
            Q1092=makeQuery(id+"F5.opExtrude","CAP_EDGE",EDGE,{"disambiguationData":[OSD([sQuery(id+"F4.wireOp",EDGE,"E6")])],"isStart":false});
            var Q1093;
            Q1093=makeQuery(id+"F5.opExtrude","CAP_EDGE",EDGE,{"disambiguationData":[OSD([sQuery(id+"F4.wireOp",EDGE,"E6")])],"isStart":false});
            var Q1094;
            Q1094=makeQuery(id+"F5.opExtrude","CAP_EDGE",EDGE,{"disambiguationData":[OSD([sQuery(id+"F4.wireOp",EDGE,"E6")])],"isStart":false});
            var Q1095;
            Q1095=makeQuery(id+"F5.opExtrude","CAP_EDGE",EDGE,{"disambiguationData":[OSD([sQuery(id+"F4.wireOp",EDGE,"E6")])],"isStart":false});
            var Q1096;
            Q1096=makeQuery(id+"F5.opExtrude","CAP_EDGE",EDGE,{"disambiguationData":[OSD([sQuery(id+"F4.wireOp",EDGE,"E6")])],"isStart":false});
            var Q1097;
            Q1097=makeQuery(id+"F5.opExtrude","CAP_EDGE",EDGE,{"disambiguationData":[OSD([sQuery(id+"F4.wireOp",EDGE,"E6")])],"isStart":false});
            var Q1098;
            Q1098=makeQuery(id+"F5.opExtrude","CAP_EDGE",EDGE,{"disambiguationData":[OSD([sQuery(id+"F4.wireOp",EDGE,"E6")])],"isStart":false});
            var Q1099;
            Q1099=makeQuery(id+"F5.opExtrude","CAP_EDGE",EDGE,{"disambiguationData":[OSD([sQuery(id+"F4.wireOp",EDGE,"E6")])],"isStart":false});
            var Q1100;
            Q1100=makeQuery(id+"F5.opExtrude","CAP_EDGE",EDGE,{"disambiguationData":[OSD([sQuery(id+"F4.wireOp",EDGE,"E6")])],"isStart":false});
            var Q1101;
            Q1101=makeQuery(id+"F5.opExtrude","CAP_EDGE",EDGE,{"disambiguationData":[OSD([sQuery(id+"F4.wireOp",EDGE,"E6")])],"isStart":false});
            var Q1102;
            Q1102=makeQuery(id+"F5.opExtrude","CAP_EDGE",EDGE,{"disambiguationData":[OSD([sQuery(id+"F4.wireOp",EDGE,"E6")])],"isStart":false});
            var Q1103;
            Q1103=makeQuery(id+"F5.opExtrude","CAP_EDGE",EDGE,{"disambiguationData":[OSD([sQuery(id+"F4.wireOp",EDGE,"E6")])],"isStart":false});
            var Q1104;
            Q1104=makeQuery(id+"F5.opExtrude","CAP_EDGE",EDGE,{"disambiguationData":[OSD([sQuery(id+"F4.wireOp",EDGE,"E6")])],"isStart":false});
            var Q1105;
            Q1105=makeQuery(id+"F5.opExtrude","CAP_EDGE",EDGE,{"disambiguationData":[OSD([sQuery(id+"F4.wireOp",EDGE,"E6")])],"isStart":false});
            var Q1106;
            Q1106=makeQuery(id+"F5.opExtrude","CAP_EDGE",EDGE,{"disambiguationData":[OSD([sQuery(id+"F4.wireOp",EDGE,"E6")])],"isStart":false});
            var Q1107;
            Q1107=makeQuery(id+"F5.opExtrude","CAP_EDGE",EDGE,{"disambiguationData":[OSD([sQuery(id+"F4.wireOp",EDGE,"E6")])],"isStart":false});
            var Q1108;
            Q1108=makeQuery(id+"F5.opExtrude","CAP_EDGE",EDGE,{"disambiguationData":[OSD([sQuery(id+"F4.wireOp",EDGE,"E6")])],"isStart":false});
            var Q1109;
            Q1109=makeQuery(id+"F5.opExtrude","CAP_EDGE",EDGE,{"disambiguationData":[OSD([sQuery(id+"F4.wireOp",EDGE,"E6")])],"isStart":false});
            var Q1110;
            Q1110=makeQuery(id+"F5.opExtrude","CAP_EDGE",EDGE,{"disambiguationData":[OSD([sQuery(id+"F4.wireOp",EDGE,"E6")])],"isStart":false});
            var Q1111;
            Q1111=makeQuery(id+"F5.opExtrude","CAP_EDGE",EDGE,{"disambiguationData":[OSD([sQuery(id+"F4.wireOp",EDGE,"E6")])],"isStart":false});
            var Q1112;
            Q1112=makeQuery(id+"F5.opExtrude","CAP_EDGE",EDGE,{"disambiguationData":[OSD([sQuery(id+"F4.wireOp",EDGE,"E6")])],"isStart":false});
            var Q1113;
            Q1113=makeQuery(id+"F5.opExtrude","CAP_EDGE",EDGE,{"disambiguationData":[OSD([sQuery(id+"F4.wireOp",EDGE,"E6")])],"isStart":false});
            var Q1114;
            Q1114=makeQuery(id+"F5.opExtrude","CAP_EDGE",EDGE,{"disambiguationData":[OSD([sQuery(id+"F4.wireOp",EDGE,"E6")])],"isStart":false});
            var Q1115;
            Q1115=makeQuery(id+"F5.opExtrude","CAP_EDGE",EDGE,{"disambiguationData":[OSD([sQuery(id+"F4.wireOp",EDGE,"E6")])],"isStart":false});
            var Q1116;
            Q1116=makeQuery(id+"F5.opExtrude","CAP_EDGE",EDGE,{"disambiguationData":[OSD([sQuery(id+"F4.wireOp",EDGE,"E6")])],"isStart":false});
            var Q1117;
            Q1117=makeQuery(id+"F5.opExtrude","CAP_EDGE",EDGE,{"disambiguationData":[OSD([sQuery(id+"F4.wireOp",EDGE,"E6")])],"isStart":false});
            var Q1118;
            Q1118=makeQuery(id+"F5.opExtrude","CAP_EDGE",EDGE,{"disambiguationData":[OSD([sQuery(id+"F4.wireOp",EDGE,"E6")])],"isStart":false});
            var Q1119;
            Q1119=makeQuery(id+"F5.opExtrude","CAP_EDGE",EDGE,{"disambiguationData":[OSD([sQuery(id+"F4.wireOp",EDGE,"E6")])],"isStart":false});
            var Q1120;
            Q1120=makeQuery(id+"F5.opExtrude","CAP_EDGE",EDGE,{"disambiguationData":[OSD([sQuery(id+"F4.wireOp",EDGE,"E6")])],"isStart":false});
            var Q1121;
            Q1121=makeQuery(id+"F5.opExtrude","CAP_EDGE",EDGE,{"disambiguationData":[OSD([sQuery(id+"F4.wireOp",EDGE,"E6")])],"isStart":false});
            var Q1122;
            Q1122=makeQuery(id+"F5.opExtrude","CAP_EDGE",EDGE,{"disambiguationData":[OSD([sQuery(id+"F4.wireOp",EDGE,"E6")])],"isStart":false});
            var Q1123;
            Q1123=makeQuery(id+"F5.opExtrude","CAP_EDGE",EDGE,{"disambiguationData":[OSD([sQuery(id+"F4.wireOp",EDGE,"E6")])],"isStart":false});
            var Q1124;
            Q1124=makeQuery(id+"F5.opExtrude","CAP_EDGE",EDGE,{"disambiguationData":[OSD([sQuery(id+"F4.wireOp",EDGE,"E6")])],"isStart":false});
            var Q1125;
            Q1125=makeQuery(id+"F5.opExtrude","CAP_EDGE",EDGE,{"disambiguationData":[OSD([sQuery(id+"F4.wireOp",EDGE,"E6")])],"isStart":false});
            var Q1126;
            Q1126=makeQuery(id+"F5.opExtrude","CAP_EDGE",EDGE,{"disambiguationData":[OSD([sQuery(id+"F4.wireOp",EDGE,"E6")])],"isStart":false});
            var Q1127;
            Q1127=makeQuery(id+"F5.opExtrude","CAP_EDGE",EDGE,{"disambiguationData":[OSD([sQuery(id+"F4.wireOp",EDGE,"E6")])],"isStart":false});
            var Q1128;
            Q1128=makeQuery(id+"F5.opExtrude","CAP_EDGE",EDGE,{"disambiguationData":[OSD([sQuery(id+"F4.wireOp",EDGE,"E6")])],"isStart":false});
            var Q1129;
            Q1129=makeQuery(id+"F5.opExtrude","CAP_EDGE",EDGE,{"disambiguationData":[OSD([sQuery(id+"F4.wireOp",EDGE,"E6")])],"isStart":false});
            var Q1130;
            Q1130=makeQuery(id+"F5.opExtrude","CAP_EDGE",EDGE,{"disambiguationData":[OSD([sQuery(id+"F4.wireOp",EDGE,"E6")])],"isStart":false});
            var Q1131;
            Q1131=makeQuery(id+"F5.opExtrude","CAP_EDGE",EDGE,{"disambiguationData":[OSD([sQuery(id+"F4.wireOp",EDGE,"E6")])],"isStart":false});
            var Q1132;
            Q1132=makeQuery(id+"F5.opExtrude","CAP_EDGE",EDGE,{"disambiguationData":[OSD([sQuery(id+"F4.wireOp",EDGE,"E6")])],"isStart":false});
            var Q1133;
            Q1133=makeQuery(id+"F5.opExtrude","CAP_EDGE",EDGE,{"disambiguationData":[OSD([sQuery(id+"F4.wireOp",EDGE,"E6")])],"isStart":false});
            var Q1134;
            Q1134=makeQuery(id+"F5.opExtrude","CAP_EDGE",EDGE,{"disambiguationData":[OSD([sQuery(id+"F4.wireOp",EDGE,"E6")])],"isStart":false});
            var Q1135;
            Q1135=makeQuery(id+"F5.opExtrude","CAP_EDGE",EDGE,{"disambiguationData":[OSD([sQuery(id+"F4.wireOp",EDGE,"E6")])],"isStart":false});
            var Q1136;
            Q1136=makeQuery(id+"F5.opExtrude","CAP_EDGE",EDGE,{"disambiguationData":[OSD([sQuery(id+"F4.wireOp",EDGE,"E6")])],"isStart":false});
            var Q1137;
            Q1137=makeQuery(id+"F5.opExtrude","CAP_EDGE",EDGE,{"disambiguationData":[OSD([sQuery(id+"F4.wireOp",EDGE,"E6")])],"isStart":false});
            var Q1138;
            Q1138=makeQuery(id+"F5.opExtrude","CAP_EDGE",EDGE,{"disambiguationData":[OSD([sQuery(id+"F4.wireOp",EDGE,"E6")])],"isStart":false});
            var Q1139;
            Q1139=makeQuery(id+"F5.opExtrude","CAP_EDGE",EDGE,{"disambiguationData":[OSD([sQuery(id+"F4.wireOp",EDGE,"E6")])],"isStart":false});
            var Q1140;
            Q1140=makeQuery(id+"F5.opExtrude","CAP_EDGE",EDGE,{"disambiguationData":[OSD([sQuery(id+"F4.wireOp",EDGE,"E6")])],"isStart":false});
            var Q1141;
            Q1141=makeQuery(id+"F5.opExtrude","CAP_EDGE",EDGE,{"disambiguationData":[OSD([sQuery(id+"F4.wireOp",EDGE,"E6")])],"isStart":false});
            var Q1142;
            Q1142=makeQuery(id+"F5.opExtrude","CAP_EDGE",EDGE,{"disambiguationData":[OSD([sQuery(id+"F4.wireOp",EDGE,"E6")])],"isStart":false});
            var Q1143;
            Q1143=makeQuery(id+"F5.opExtrude","CAP_EDGE",EDGE,{"disambiguationData":[OSD([sQuery(id+"F4.wireOp",EDGE,"E6")])],"isStart":false});
            var Q1144;
            Q1144=makeQuery(id+"F5.opExtrude","CAP_EDGE",EDGE,{"disambiguationData":[OSD([sQuery(id+"F4.wireOp",EDGE,"E6")])],"isStart":false});
            var Q1145;
            Q1145=makeQuery(id+"F5.opExtrude","CAP_EDGE",EDGE,{"disambiguationData":[OSD([sQuery(id+"F4.wireOp",EDGE,"E6")])],"isStart":false});
            var Q1146;
            Q1146=makeQuery(id+"F5.opExtrude","CAP_EDGE",EDGE,{"disambiguationData":[OSD([sQuery(id+"F4.wireOp",EDGE,"E6")])],"isStart":false});
            var Q1147;
            Q1147=makeQuery(id+"F5.opExtrude","CAP_EDGE",EDGE,{"disambiguationData":[OSD([sQuery(id+"F4.wireOp",EDGE,"E6")])],"isStart":false});
            var Q1148;
            Q1148=makeQuery(id+"F5.opExtrude","CAP_EDGE",EDGE,{"disambiguationData":[OSD([sQuery(id+"F4.wireOp",EDGE,"E6")])],"isStart":false});
            var Q1149;
            Q1149=makeQuery(id+"F5.opExtrude","CAP_EDGE",EDGE,{"disambiguationData":[OSD([sQuery(id+"F4.wireOp",EDGE,"E6")])],"isStart":false});
            var Q1150;
            Q1150=makeQuery(id+"F5.opExtrude","CAP_EDGE",EDGE,{"disambiguationData":[OSD([sQuery(id+"F4.wireOp",EDGE,"E6")])],"isStart":false});
            var Q1151;
            Q1151=makeQuery(id+"F5.opExtrude","CAP_EDGE",EDGE,{"disambiguationData":[OSD([sQuery(id+"F4.wireOp",EDGE,"E6")])],"isStart":false});
            var Q1152;
            Q1152=makeQuery(id+"F5.opExtrude","CAP_EDGE",EDGE,{"disambiguationData":[OSD([sQuery(id+"F4.wireOp",EDGE,"E6")])],"isStart":false});
            var Q1153;
            Q1153=makeQuery(id+"F5.opExtrude","CAP_EDGE",EDGE,{"disambiguationData":[OSD([sQuery(id+"F4.wireOp",EDGE,"E6")])],"isStart":false});
            var Q1154;
            Q1154=makeQuery(id+"F5.opExtrude","CAP_EDGE",EDGE,{"disambiguationData":[OSD([sQuery(id+"F4.wireOp",EDGE,"E6")])],"isStart":false});
            var Q1155;
            Q1155=makeQuery(id+"F5.opExtrude","CAP_EDGE",EDGE,{"disambiguationData":[OSD([sQuery(id+"F4.wireOp",EDGE,"E6")])],"isStart":false});
            var Q1156;
            Q1156=makeQuery(id+"F5.opExtrude","CAP_EDGE",EDGE,{"disambiguationData":[OSD([sQuery(id+"F4.wireOp",EDGE,"E6")])],"isStart":false});
            var Q1157;
            Q1157=makeQuery(id+"F5.opExtrude","CAP_EDGE",EDGE,{"disambiguationData":[OSD([sQuery(id+"F4.wireOp",EDGE,"E6")])],"isStart":false});
            var Q1158;
            Q1158=makeQuery(id+"F5.opExtrude","CAP_EDGE",EDGE,{"disambiguationData":[OSD([sQuery(id+"F4.wireOp",EDGE,"E6")])],"isStart":false});
            var Q1159;
            Q1159=makeQuery(id+"F5.opExtrude","CAP_EDGE",EDGE,{"disambiguationData":[OSD([sQuery(id+"F4.wireOp",EDGE,"E6")])],"isStart":false});
            var Q1160;
            Q1160=makeQuery(id+"F5.opExtrude","CAP_EDGE",EDGE,{"disambiguationData":[OSD([sQuery(id+"F4.wireOp",EDGE,"E6")])],"isStart":false});
            var Q1161;
            Q1161=makeQuery(id+"F5.opExtrude","CAP_EDGE",EDGE,{"disambiguationData":[OSD([sQuery(id+"F4.wireOp",EDGE,"E6")])],"isStart":false});
            var Q1162;
            Q1162=makeQuery(id+"F5.opExtrude","CAP_EDGE",EDGE,{"disambiguationData":[OSD([sQuery(id+"F4.wireOp",EDGE,"E6")])],"isStart":false});
            var Q1163;
            Q1163=makeQuery(id+"F5.opExtrude","CAP_EDGE",EDGE,{"disambiguationData":[OSD([sQuery(id+"F4.wireOp",EDGE,"E6")])],"isStart":false});
            var Q1164;
            Q1164=makeQuery(id+"F5.opExtrude","CAP_EDGE",EDGE,{"disambiguationData":[OSD([sQuery(id+"F4.wireOp",EDGE,"E6")])],"isStart":false});
            var Q1165;
            Q1165=makeQuery(id+"F5.opExtrude","CAP_EDGE",EDGE,{"disambiguationData":[OSD([sQuery(id+"F4.wireOp",EDGE,"E6")])],"isStart":false});
            var Q1166;
            Q1166=makeQuery(id+"F5.opExtrude","CAP_EDGE",EDGE,{"disambiguationData":[OSD([sQuery(id+"F4.wireOp",EDGE,"E6")])],"isStart":false});
            var Q1167;
            Q1167=makeQuery(id+"F5.opExtrude","CAP_EDGE",EDGE,{"disambiguationData":[OSD([sQuery(id+"F4.wireOp",EDGE,"E6")])],"isStart":false});
            var Q1168;
            Q1168=makeQuery(id+"F5.opExtrude","CAP_EDGE",EDGE,{"disambiguationData":[OSD([sQuery(id+"F4.wireOp",EDGE,"E6")])],"isStart":false});
            var Q1169;
            Q1169=makeQuery(id+"F5.opExtrude","CAP_EDGE",EDGE,{"disambiguationData":[OSD([sQuery(id+"F4.wireOp",EDGE,"E6")])],"isStart":false});
            var Q1170;
            Q1170=makeQuery(id+"F5.opExtrude","CAP_EDGE",EDGE,{"disambiguationData":[OSD([sQuery(id+"F4.wireOp",EDGE,"E6")])],"isStart":false});
            var Q1171;
            Q1171=makeQuery(id+"F5.opExtrude","CAP_EDGE",EDGE,{"disambiguationData":[OSD([sQuery(id+"F4.wireOp",EDGE,"E6")])],"isStart":false});
            var Q1172;
            Q1172=makeQuery(id+"F5.opExtrude","CAP_EDGE",EDGE,{"disambiguationData":[OSD([sQuery(id+"F4.wireOp",EDGE,"E6")])],"isStart":false});
            var Q1173;
            Q1173=makeQuery(id+"F5.opExtrude","CAP_EDGE",EDGE,{"disambiguationData":[OSD([sQuery(id+"F4.wireOp",EDGE,"E6")])],"isStart":false});
            var Q1174;
            Q1174=makeQuery(id+"F5.opExtrude","CAP_EDGE",EDGE,{"disambiguationData":[OSD([sQuery(id+"F4.wireOp",EDGE,"E6")])],"isStart":false});
            var Q1175;
            Q1175=makeQuery(id+"F5.opExtrude","CAP_EDGE",EDGE,{"disambiguationData":[OSD([sQuery(id+"F4.wireOp",EDGE,"E6")])],"isStart":false});
            var Q1176;
            Q1176=makeQuery(id+"F5.opExtrude","CAP_EDGE",EDGE,{"disambiguationData":[OSD([sQuery(id+"F4.wireOp",EDGE,"E6")])],"isStart":false});
            var Q1177;
            Q1177=makeQuery(id+"F5.opExtrude","CAP_EDGE",EDGE,{"disambiguationData":[OSD([sQuery(id+"F4.wireOp",EDGE,"E6")])],"isStart":false});
            var Q1178;
            Q1178=makeQuery(id+"F5.opExtrude","CAP_EDGE",EDGE,{"disambiguationData":[OSD([sQuery(id+"F4.wireOp",EDGE,"E6")])],"isStart":false});
            var Q1179;
            Q1179=makeQuery(id+"F5.opExtrude","CAP_EDGE",EDGE,{"disambiguationData":[OSD([sQuery(id+"F4.wireOp",EDGE,"E6")])],"isStart":false});
            var Q1180;
            Q1180=makeQuery(id+"F5.opExtrude","CAP_EDGE",EDGE,{"disambiguationData":[OSD([sQuery(id+"F4.wireOp",EDGE,"E6")])],"isStart":false});
            var Q1181;
            Q1181=makeQuery(id+"F5.opExtrude","CAP_EDGE",EDGE,{"disambiguationData":[OSD([sQuery(id+"F4.wireOp",EDGE,"E6")])],"isStart":false});
            var Q1182;
            Q1182=makeQuery(id+"F5.opExtrude","CAP_EDGE",EDGE,{"disambiguationData":[OSD([sQuery(id+"F4.wireOp",EDGE,"E6")])],"isStart":false});
            var Q1183;
            Q1183=makeQuery(id+"F5.opExtrude","CAP_EDGE",EDGE,{"disambiguationData":[OSD([sQuery(id+"F4.wireOp",EDGE,"E6")])],"isStart":false});
            var Q1184;
            Q1184=makeQuery(id+"F5.opExtrude","CAP_EDGE",EDGE,{"disambiguationData":[OSD([sQuery(id+"F4.wireOp",EDGE,"E6")])],"isStart":false});
            var Q1185;
            Q1185=makeQuery(id+"F5.opExtrude","CAP_EDGE",EDGE,{"disambiguationData":[OSD([sQuery(id+"F4.wireOp",EDGE,"E6")])],"isStart":false});
            var Q1186;
            Q1186=makeQuery(id+"F5.opExtrude","CAP_EDGE",EDGE,{"disambiguationData":[OSD([sQuery(id+"F4.wireOp",EDGE,"E6")])],"isStart":false});
            var Q1187;
            Q1187=makeQuery(id+"F5.opExtrude","CAP_EDGE",EDGE,{"disambiguationData":[OSD([sQuery(id+"F4.wireOp",EDGE,"E6")])],"isStart":false});
            var Q1188;
            Q1188=makeQuery(id+"F5.opExtrude","CAP_EDGE",EDGE,{"disambiguationData":[OSD([sQuery(id+"F4.wireOp",EDGE,"E6")])],"isStart":false});
            var Q1189;
            Q1189=makeQuery(id+"F5.opExtrude","CAP_EDGE",EDGE,{"disambiguationData":[OSD([sQuery(id+"F4.wireOp",EDGE,"E6")])],"isStart":false});
            var Q1190;
            Q1190=makeQuery(id+"F5.opExtrude","CAP_EDGE",EDGE,{"disambiguationData":[OSD([sQuery(id+"F4.wireOp",EDGE,"E6")])],"isStart":false});
            var Q1191;
            Q1191=makeQuery(id+"F5.opExtrude","CAP_EDGE",EDGE,{"disambiguationData":[OSD([sQuery(id+"F4.wireOp",EDGE,"E6")])],"isStart":false});
            var Q1192;
            Q1192=makeQuery(id+"F5.opExtrude","CAP_EDGE",EDGE,{"disambiguationData":[OSD([sQuery(id+"F4.wireOp",EDGE,"E6")])],"isStart":false});
            var Q1193;
            Q1193=makeQuery(id+"F5.opExtrude","CAP_EDGE",EDGE,{"disambiguationData":[OSD([sQuery(id+"F4.wireOp",EDGE,"E6")])],"isStart":false});
            var Q1194;
            Q1194=makeQuery(id+"F5.opExtrude","CAP_EDGE",EDGE,{"disambiguationData":[OSD([sQuery(id+"F4.wireOp",EDGE,"E6")])],"isStart":false});
            var Q1195;
            Q1195=makeQuery(id+"F5.opExtrude","CAP_EDGE",EDGE,{"disambiguationData":[OSD([sQuery(id+"F4.wireOp",EDGE,"E6")])],"isStart":false});
            var Q1196;
            Q1196=makeQuery(id+"F5.opExtrude","CAP_EDGE",EDGE,{"disambiguationData":[OSD([sQuery(id+"F4.wireOp",EDGE,"E6")])],"isStart":false});
            var Q1197;
            Q1197=makeQuery(id+"F5.opExtrude","CAP_EDGE",EDGE,{"disambiguationData":[OSD([sQuery(id+"F4.wireOp",EDGE,"E6")])],"isStart":false});
            var Q1198;
            Q1198=makeQuery(id+"F5.opExtrude","CAP_EDGE",EDGE,{"disambiguationData":[OSD([sQuery(id+"F4.wireOp",EDGE,"E6")])],"isStart":false});
            var Q1199;
            Q1199=makeQuery(id+"F5.opExtrude","CAP_EDGE",EDGE,{"disambiguationData":[OSD([sQuery(id+"F4.wireOp",EDGE,"E6")])],"isStart":false});
            var Q1200;
            Q1200=makeQuery(id+"F5.opExtrude","CAP_EDGE",EDGE,{"disambiguationData":[OSD([sQuery(id+"F4.wireOp",EDGE,"E6")])],"isStart":false});
            var Q1201;
            Q1201=makeQuery(id+"F5.opExtrude","CAP_EDGE",EDGE,{"disambiguationData":[OSD([sQuery(id+"F4.wireOp",EDGE,"E6")])],"isStart":false});
            var Q1202;
            Q1202=makeQuery(id+"F5.opExtrude","CAP_EDGE",EDGE,{"disambiguationData":[OSD([sQuery(id+"F4.wireOp",EDGE,"E6")])],"isStart":false});
            var Q1203;
            Q1203=makeQuery(id+"F5.opExtrude","CAP_EDGE",EDGE,{"disambiguationData":[OSD([sQuery(id+"F4.wireOp",EDGE,"E6")])],"isStart":false});
            var Q1204;
            Q1204=makeQuery(id+"F7.boolean.opBoolean","INTERSECT",EDGE,{"derivedFrom":[makeQuery(id+"F5.opExtrude","SWEPT_FACE",FACE,{"disambiguationData":[OSD([sQuery(id+"F4.wireOp",EDGE,"E8")])]}),makeQuery(id+"F7.opRevolve","SWEPT_FACE",FACE,{"disambiguationData":[OSD([sQuery(id+"F6.wireOp",EDGE,"E12")])]})]});
            var Q1205;
            Q1205=makeQuery(id+"F5.opExtrude","CAP_EDGE",EDGE,{"disambiguationData":[OSD([sQuery(id+"F4.wireOp",EDGE,"E8")])],"isStart":false});
            var Q1206;
            Q1206=makeQuery(id+"F5.opExtrude","CAP_EDGE",EDGE,{"disambiguationData":[OSD([sQuery(id+"F4.wireOp",EDGE,"E9")])],"isStart":false});
            var Q1207;
            Q1207=makeQuery(id+"F5.opExtrude","CAP_EDGE",EDGE,{"disambiguationData":[OSD([sQuery(id+"F4.wireOp",EDGE,"E7")])],"isStart":false});
            var Q1208;
            Q1208=makeQuery(id+"F7.boolean.opBoolean","INTERSECT",EDGE,{"derivedFrom":[makeQuery(id+"F5.opExtrude","SWEPT_FACE",FACE,{"disambiguationData":[OSD([sQuery(id+"F4.wireOp",EDGE,"E7")])]}),makeQuery(id+"F7.opRevolve","SWEPT_FACE",FACE,{"disambiguationData":[OSD([sQuery(id+"F6.wireOp",EDGE,"E12")])]})]});
            var Q1209;
            Q1209=makeQuery(id+"F7.boolean.opBoolean","INTERSECT",EDGE,{"derivedFrom":[makeQuery(id+"F5.opExtrude","SWEPT_FACE",FACE,{"disambiguationData":[OSD([sQuery(id+"F4.wireOp",EDGE,"E9")])]}),makeQuery(id+"F7.opRevolve","SWEPT_FACE",FACE,{"disambiguationData":[OSD([sQuery(id+"F6.wireOp",EDGE,"E12")])]})]});
            var Q1210;
            Q1210=makeQuery(id+"F15.opFillet","BLEND_EDGE",EDGE,{"disambiguationData":[OD(1.0)],"blendedFrom":[makeQuery(id+"F7.boolean.opBoolean","COPY",EDGE,{"derivedFrom":makeQuery(id+"F7.opRevolve","SWEPT_EDGE",EDGE,{"disambiguationData":[OSD([sQuery(id+"F6.wireOp",EDGE,"E11"),sQuery(id+"F6.wireOp",EDGE,"E12")])]})}),makeQuery(id+"F5.opExtrude","SWEPT_FACE",FACE,{"disambiguationData":[OSD([sQuery(id+"F4.wireOp",EDGE,"E6")])]})],"blendedInto":[makeQuery(id+"F5.opExtrude","SWEPT_FACE",FACE,{"disambiguationData":[OSD([sQuery(id+"F4.wireOp",EDGE,"E6")])]})]});
            var Q1211;
            Q1211=makeQuery(id+"F7.boolean.opBoolean","INTERSECT",EDGE,{"disambiguationData":[OD(1.0)],"derivedFrom":[makeQuery(id+"F5.opExtrude","SWEPT_FACE",FACE,{"disambiguationData":[OSD([sQuery(id+"F4.wireOp",EDGE,"E6")])]}),makeQuery(id+"F7.opRevolve","SWEPT_FACE",FACE,{"disambiguationData":[OSD([sQuery(id+"F6.wireOp",EDGE,"E12")])]})]});
            var Q1212;
            Q1212=makeQuery(id+"F7.boolean.opBoolean","INTERSECT",EDGE,{"disambiguationData":[OD(1.0)],"derivedFrom":[makeQuery(id+"F5.opExtrude","SWEPT_FACE",FACE,{"disambiguationData":[OSD([sQuery(id+"F4.wireOp",EDGE,"E6")])]}),makeQuery(id+"F7.opRevolve","SWEPT_FACE",FACE,{"disambiguationData":[OSD([sQuery(id+"F6.wireOp",EDGE,"E11")])]})]});
            var Q1213;
            Q1213=makeQuery(id+"F7.boolean.opBoolean","INTERSECT",EDGE,{"derivedFrom":[makeQuery(id+"F5.opExtrude","SWEPT_FACE",FACE,{"disambiguationData":[OSD([sQuery(id+"F4.wireOp",EDGE,"E8")])]}),makeQuery(id+"F7.opRevolve","SWEPT_FACE",FACE,{"disambiguationData":[OSD([sQuery(id+"F6.wireOp",EDGE,"E10")])]})]});
            var Q1214;
            Q1214=makeQuery(id+"F7.boolean.opBoolean","INTERSECT",EDGE,{"derivedFrom":[makeQuery(id+"F5.opExtrude","SWEPT_FACE",FACE,{"disambiguationData":[OSD([sQuery(id+"F4.wireOp",EDGE,"E7")])]}),makeQuery(id+"F7.opRevolve","SWEPT_FACE",FACE,{"disambiguationData":[OSD([sQuery(id+"F6.wireOp",EDGE,"E10")])]})]});
            var Q1215;
            Q1215=makeQuery(id+"F7.boolean.opBoolean","INTERSECT",EDGE,{"derivedFrom":[makeQuery(id+"F5.opExtrude","SWEPT_FACE",FACE,{"disambiguationData":[OSD([sQuery(id+"F4.wireOp",EDGE,"E9")])]}),makeQuery(id+"F7.opRevolve","SWEPT_FACE",FACE,{"disambiguationData":[OSD([sQuery(id+"F6.wireOp",EDGE,"E10")])]})]});
            var Q1216;
            Q1216=makeQuery(id+"F7.boolean.opBoolean","INTERSECT",EDGE,{"disambiguationData":[OD(1.0)],"derivedFrom":[makeQuery(id+"F5.opExtrude","SWEPT_FACE",FACE,{"disambiguationData":[OSD([sQuery(id+"F4.wireOp",EDGE,"E6")])]}),makeQuery(id+"F7.opRevolve","SWEPT_FACE",FACE,{"disambiguationData":[OSD([sQuery(id+"F6.wireOp",EDGE,"E10")])]})]});
            var Q1217;
            {var subQ0=sQuery(id+"F6.wireOp",EDGE,"E10");Q1217=makeQuery(id+"F15.opFillet","BLEND_EDGE",EDGE,{"blendedFrom":[makeQuery(id+"F7.boolean.opBoolean","COPY",EDGE,{"derivedFrom":makeQuery(id+"F7.opRevolve","SWEPT_EDGE",EDGE,{"disambiguationData":[OSD([subQ0,sQuery(id+"F6.wireOp",EDGE,"E11")])]})}),makeQuery(id+"F7.boolean.opBoolean","COPY",FACE,{"derivedFrom":makeQuery(id+"F7.opRevolve","SWEPT_FACE",FACE,{"disambiguationData":[OSD([subQ0])]})})],"blendedInto":[makeQuery(id+"F7.boolean.opBoolean","COPY",FACE,{"derivedFrom":makeQuery(id+"F7.opRevolve","SWEPT_FACE",FACE,{"disambiguationData":[OSD([subQ0])]})})]});}
            var Q1218;
            Q1218=makeQuery(id+"F7.boolean.opBoolean","INTERSECT",EDGE,{"disambiguationData":[OD(0.0)],"derivedFrom":[makeQuery(id+"F5.opExtrude","SWEPT_FACE",FACE,{"disambiguationData":[OSD([sQuery(id+"F4.wireOp",EDGE,"E6")])]}),makeQuery(id+"F7.opRevolve","SWEPT_FACE",FACE,{"disambiguationData":[OSD([sQuery(id+"F6.wireOp",EDGE,"E10")])]})]});
            var Q1219;
            Q1219=makeQuery(id+"F15.opFillet","BLEND_EDGE",EDGE,{"disambiguationData":[OD(0.0)],"blendedFrom":[makeQuery(id+"F7.boolean.opBoolean","COPY",EDGE,{"derivedFrom":makeQuery(id+"F7.opRevolve","SWEPT_EDGE",EDGE,{"disambiguationData":[OSD([sQuery(id+"F6.wireOp",EDGE,"E10"),sQuery(id+"F6.wireOp",EDGE,"E11")])]})}),makeQuery(id+"F5.opExtrude","SWEPT_FACE",FACE,{"disambiguationData":[OSD([sQuery(id+"F4.wireOp",EDGE,"E6")])]})],"blendedInto":[makeQuery(id+"F5.opExtrude","SWEPT_FACE",FACE,{"disambiguationData":[OSD([sQuery(id+"F4.wireOp",EDGE,"E6")])]})]});
            var Q1220;
            Q1220=makeQuery(id+"F7.boolean.opBoolean","INTERSECT",EDGE,{"disambiguationData":[OD(0.0)],"derivedFrom":[makeQuery(id+"F5.opExtrude","SWEPT_FACE",FACE,{"disambiguationData":[OSD([sQuery(id+"F4.wireOp",EDGE,"E6")])]}),makeQuery(id+"F7.opRevolve","SWEPT_FACE",FACE,{"disambiguationData":[OSD([sQuery(id+"F6.wireOp",EDGE,"E11")])]})]});
            var Q1221;
            Q1221=makeQuery(id+"F15.opFillet","BLEND_EDGE",EDGE,{"disambiguationData":[OD(1.0)],"blendedFrom":[makeQuery(id+"F7.boolean.opBoolean","COPY",EDGE,{"derivedFrom":makeQuery(id+"F7.opRevolve","SWEPT_EDGE",EDGE,{"disambiguationData":[OSD([sQuery(id+"F6.wireOp",EDGE,"E10"),sQuery(id+"F6.wireOp",EDGE,"E11")])]})}),makeQuery(id+"F5.opExtrude","SWEPT_FACE",FACE,{"disambiguationData":[OSD([sQuery(id+"F4.wireOp",EDGE,"E6")])]})],"blendedInto":[makeQuery(id+"F5.opExtrude","SWEPT_FACE",FACE,{"disambiguationData":[OSD([sQuery(id+"F4.wireOp",EDGE,"E6")])]})]});
            var Q1222;
            Q1222=makeQuery(id+"F15.opFillet","BLEND_EDGE",EDGE,{"disambiguationData":[OD(0.0)],"blendedFrom":[makeQuery(id+"F7.boolean.opBoolean","COPY",EDGE,{"derivedFrom":makeQuery(id+"F7.opRevolve","SWEPT_EDGE",EDGE,{"disambiguationData":[OSD([sQuery(id+"F6.wireOp",EDGE,"E11"),sQuery(id+"F6.wireOp",EDGE,"E12")])]})}),makeQuery(id+"F5.opExtrude","SWEPT_FACE",FACE,{"disambiguationData":[OSD([sQuery(id+"F4.wireOp",EDGE,"E6")])]})],"blendedInto":[makeQuery(id+"F5.opExtrude","SWEPT_FACE",FACE,{"disambiguationData":[OSD([sQuery(id+"F4.wireOp",EDGE,"E6")])]})]});
            var Q1223;
            Q1223=makeQuery(id+"F7.boolean.opBoolean","INTERSECT",EDGE,{"disambiguationData":[OD(0.0)],"derivedFrom":[makeQuery(id+"F5.opExtrude","SWEPT_FACE",FACE,{"disambiguationData":[OSD([sQuery(id+"F4.wireOp",EDGE,"E6")])]}),makeQuery(id+"F7.opRevolve","SWEPT_FACE",FACE,{"disambiguationData":[OSD([sQuery(id+"F6.wireOp",EDGE,"E12")])]})]});
            var Q1224;
            Q1224=makeQuery(id+"F5.opExtrude","CAP_EDGE",EDGE,{"disambiguationData":[OSD([sQuery(id+"F4.wireOp",EDGE,"E8")])],"isStart":true});
            var Q1225;
            Q1225=makeQuery(id+"F5.opExtrude","CAP_EDGE",EDGE,{"disambiguationData":[OSD([sQuery(id+"F4.wireOp",EDGE,"E7")])],"isStart":true});
            var Q1226;
            Q1226=makeQuery(id+"F5.opExtrude","CAP_EDGE",EDGE,{"disambiguationData":[OSD([sQuery(id+"F4.wireOp",EDGE,"E9")])],"isStart":true});
            var Q1227;
            Q1227=makeQuery(id+"F5.opExtrude","CAP_EDGE",EDGE,{"disambiguationData":[OSD([sQuery(id+"F4.wireOp",EDGE,"E6")])],"isStart":true});
            var Q1228;
            Q1228=makeQuery(id+"F5.opExtrude","CAP_EDGE",EDGE,{"disambiguationData":[OSD([sQuery(id+"F4.wireOp",EDGE,"E6")])],"isStart":true});
            var Q1229;
            Q1229=makeQuery(id+"F5.opExtrude","CAP_EDGE",EDGE,{"disambiguationData":[OSD([sQuery(id+"F4.wireOp",EDGE,"E6")])],"isStart":true});
            var Q1230;
            Q1230=makeQuery(id+"F5.opExtrude","CAP_EDGE",EDGE,{"disambiguationData":[OSD([sQuery(id+"F4.wireOp",EDGE,"E6")])],"isStart":true});
            var Q1231;
            Q1231=makeQuery(id+"F5.opExtrude","CAP_EDGE",EDGE,{"disambiguationData":[OSD([sQuery(id+"F4.wireOp",EDGE,"E6")])],"isStart":true});
            var Q1232;
            Q1232=makeQuery(id+"F5.opExtrude","CAP_EDGE",EDGE,{"disambiguationData":[OSD([sQuery(id+"F4.wireOp",EDGE,"E6")])],"isStart":true});
            var Q1233;
            Q1233=makeQuery(id+"F5.opExtrude","CAP_EDGE",EDGE,{"disambiguationData":[OSD([sQuery(id+"F4.wireOp",EDGE,"E6")])],"isStart":true});
            var Q1234;
            Q1234=makeQuery(id+"F5.opExtrude","CAP_EDGE",EDGE,{"disambiguationData":[OSD([sQuery(id+"F4.wireOp",EDGE,"E6")])],"isStart":true});
            var Q1235;
            Q1235=makeQuery(id+"F5.opExtrude","CAP_EDGE",EDGE,{"disambiguationData":[OSD([sQuery(id+"F4.wireOp",EDGE,"E6")])],"isStart":true});
            var Q1236;
            Q1236=makeQuery(id+"F5.opExtrude","CAP_EDGE",EDGE,{"disambiguationData":[OSD([sQuery(id+"F4.wireOp",EDGE,"E6")])],"isStart":true});
            var Q1237;
            Q1237=makeQuery(id+"F5.opExtrude","CAP_EDGE",EDGE,{"disambiguationData":[OSD([sQuery(id+"F4.wireOp",EDGE,"E6")])],"isStart":true});
            var Q1238;
            Q1238=makeQuery(id+"F5.opExtrude","CAP_EDGE",EDGE,{"disambiguationData":[OSD([sQuery(id+"F4.wireOp",EDGE,"E6")])],"isStart":true});
            var Q1239;
            Q1239=makeQuery(id+"F5.opExtrude","CAP_EDGE",EDGE,{"disambiguationData":[OSD([sQuery(id+"F4.wireOp",EDGE,"E6")])],"isStart":true});
            var Q1240;
            Q1240=makeQuery(id+"F5.opExtrude","CAP_EDGE",EDGE,{"disambiguationData":[OSD([sQuery(id+"F4.wireOp",EDGE,"E6")])],"isStart":true});
            var Q1241;
            Q1241=makeQuery(id+"F5.opExtrude","CAP_EDGE",EDGE,{"disambiguationData":[OSD([sQuery(id+"F4.wireOp",EDGE,"E6")])],"isStart":true});
            var Q1242;
            Q1242=makeQuery(id+"F5.opExtrude","CAP_EDGE",EDGE,{"disambiguationData":[OSD([sQuery(id+"F4.wireOp",EDGE,"E6")])],"isStart":true});
            var Q1243;
            Q1243=makeQuery(id+"F5.opExtrude","CAP_EDGE",EDGE,{"disambiguationData":[OSD([sQuery(id+"F4.wireOp",EDGE,"E6")])],"isStart":true});
            var Q1244;
            Q1244=makeQuery(id+"F5.opExtrude","CAP_EDGE",EDGE,{"disambiguationData":[OSD([sQuery(id+"F4.wireOp",EDGE,"E6")])],"isStart":true});
            var Q1245;
            Q1245=makeQuery(id+"F5.opExtrude","CAP_EDGE",EDGE,{"disambiguationData":[OSD([sQuery(id+"F4.wireOp",EDGE,"E6")])],"isStart":true});
            var Q1246;
            Q1246=makeQuery(id+"F5.opExtrude","CAP_EDGE",EDGE,{"disambiguationData":[OSD([sQuery(id+"F4.wireOp",EDGE,"E6")])],"isStart":true});
            var Q1247;
            Q1247=makeQuery(id+"F5.opExtrude","CAP_EDGE",EDGE,{"disambiguationData":[OSD([sQuery(id+"F4.wireOp",EDGE,"E6")])],"isStart":true});
            var Q1248;
            Q1248=makeQuery(id+"F5.opExtrude","CAP_EDGE",EDGE,{"disambiguationData":[OSD([sQuery(id+"F4.wireOp",EDGE,"E6")])],"isStart":true});
            var Q1249;
            Q1249=makeQuery(id+"F5.opExtrude","CAP_EDGE",EDGE,{"disambiguationData":[OSD([sQuery(id+"F4.wireOp",EDGE,"E6")])],"isStart":true});
            var Q1250;
            Q1250=makeQuery(id+"F5.opExtrude","CAP_EDGE",EDGE,{"disambiguationData":[OSD([sQuery(id+"F4.wireOp",EDGE,"E6")])],"isStart":true});
            var Q1251;
            Q1251=makeQuery(id+"F5.opExtrude","CAP_EDGE",EDGE,{"disambiguationData":[OSD([sQuery(id+"F4.wireOp",EDGE,"E6")])],"isStart":true});
            var Q1252;
            Q1252=makeQuery(id+"F5.opExtrude","CAP_EDGE",EDGE,{"disambiguationData":[OSD([sQuery(id+"F4.wireOp",EDGE,"E6")])],"isStart":true});
            var Q1253;
            Q1253=makeQuery(id+"F5.opExtrude","CAP_EDGE",EDGE,{"disambiguationData":[OSD([sQuery(id+"F4.wireOp",EDGE,"E6")])],"isStart":true});
            var Q1254;
            Q1254=makeQuery(id+"F5.opExtrude","CAP_EDGE",EDGE,{"disambiguationData":[OSD([sQuery(id+"F4.wireOp",EDGE,"E6")])],"isStart":true});
            var Q1255;
            Q1255=makeQuery(id+"F5.opExtrude","CAP_EDGE",EDGE,{"disambiguationData":[OSD([sQuery(id+"F4.wireOp",EDGE,"E6")])],"isStart":true});
            var Q1256;
            Q1256=makeQuery(id+"F5.opExtrude","CAP_EDGE",EDGE,{"disambiguationData":[OSD([sQuery(id+"F4.wireOp",EDGE,"E6")])],"isStart":true});
            var Q1257;
            Q1257=makeQuery(id+"F5.opExtrude","CAP_EDGE",EDGE,{"disambiguationData":[OSD([sQuery(id+"F4.wireOp",EDGE,"E6")])],"isStart":true});
            var Q1258;
            Q1258=makeQuery(id+"F5.opExtrude","CAP_EDGE",EDGE,{"disambiguationData":[OSD([sQuery(id+"F4.wireOp",EDGE,"E6")])],"isStart":true});
            var Q1259;
            Q1259=makeQuery(id+"F5.opExtrude","CAP_EDGE",EDGE,{"disambiguationData":[OSD([sQuery(id+"F4.wireOp",EDGE,"E6")])],"isStart":true});
            var Q1260;
            Q1260=makeQuery(id+"F5.opExtrude","CAP_EDGE",EDGE,{"disambiguationData":[OSD([sQuery(id+"F4.wireOp",EDGE,"E6")])],"isStart":true});
            var Q1261;
            Q1261=makeQuery(id+"F5.opExtrude","CAP_EDGE",EDGE,{"disambiguationData":[OSD([sQuery(id+"F4.wireOp",EDGE,"E6")])],"isStart":true});
            var Q1262;
            Q1262=makeQuery(id+"F5.opExtrude","CAP_EDGE",EDGE,{"disambiguationData":[OSD([sQuery(id+"F4.wireOp",EDGE,"E6")])],"isStart":true});
            var Q1263;
            Q1263=makeQuery(id+"F5.opExtrude","CAP_EDGE",EDGE,{"disambiguationData":[OSD([sQuery(id+"F4.wireOp",EDGE,"E6")])],"isStart":true});
            var Q1264;
            Q1264=makeQuery(id+"F5.opExtrude","CAP_EDGE",EDGE,{"disambiguationData":[OSD([sQuery(id+"F4.wireOp",EDGE,"E6")])],"isStart":true});
            var Q1265;
            Q1265=makeQuery(id+"F5.opExtrude","CAP_EDGE",EDGE,{"disambiguationData":[OSD([sQuery(id+"F4.wireOp",EDGE,"E6")])],"isStart":true});
            var Q1266;
            Q1266=makeQuery(id+"F5.opExtrude","CAP_EDGE",EDGE,{"disambiguationData":[OSD([sQuery(id+"F4.wireOp",EDGE,"E6")])],"isStart":true});
            var Q1267;
            Q1267=makeQuery(id+"F5.opExtrude","CAP_EDGE",EDGE,{"disambiguationData":[OSD([sQuery(id+"F4.wireOp",EDGE,"E6")])],"isStart":true});
            var Q1268;
            Q1268=makeQuery(id+"F5.opExtrude","CAP_EDGE",EDGE,{"disambiguationData":[OSD([sQuery(id+"F4.wireOp",EDGE,"E6")])],"isStart":true});
            var Q1269;
            Q1269=makeQuery(id+"F5.opExtrude","CAP_EDGE",EDGE,{"disambiguationData":[OSD([sQuery(id+"F4.wireOp",EDGE,"E6")])],"isStart":true});
            var Q1270;
            Q1270=makeQuery(id+"F5.opExtrude","CAP_EDGE",EDGE,{"disambiguationData":[OSD([sQuery(id+"F4.wireOp",EDGE,"E6")])],"isStart":true});
            var Q1271;
            Q1271=makeQuery(id+"F5.opExtrude","CAP_EDGE",EDGE,{"disambiguationData":[OSD([sQuery(id+"F4.wireOp",EDGE,"E6")])],"isStart":true});
            var Q1272;
            Q1272=makeQuery(id+"F5.opExtrude","CAP_EDGE",EDGE,{"disambiguationData":[OSD([sQuery(id+"F4.wireOp",EDGE,"E6")])],"isStart":true});
            var Q1273;
            Q1273=makeQuery(id+"F5.opExtrude","CAP_EDGE",EDGE,{"disambiguationData":[OSD([sQuery(id+"F4.wireOp",EDGE,"E6")])],"isStart":true});
            var Q1274;
            Q1274=makeQuery(id+"F5.opExtrude","CAP_EDGE",EDGE,{"disambiguationData":[OSD([sQuery(id+"F4.wireOp",EDGE,"E6")])],"isStart":true});
            var Q1275;
            Q1275=makeQuery(id+"F5.opExtrude","CAP_EDGE",EDGE,{"disambiguationData":[OSD([sQuery(id+"F4.wireOp",EDGE,"E6")])],"isStart":true});
            var Q1276;
            Q1276=makeQuery(id+"F5.opExtrude","CAP_EDGE",EDGE,{"disambiguationData":[OSD([sQuery(id+"F4.wireOp",EDGE,"E6")])],"isStart":true});
            var Q1277;
            Q1277=makeQuery(id+"F5.opExtrude","CAP_EDGE",EDGE,{"disambiguationData":[OSD([sQuery(id+"F4.wireOp",EDGE,"E6")])],"isStart":true});
            var Q1278;
            Q1278=makeQuery(id+"F5.opExtrude","CAP_EDGE",EDGE,{"disambiguationData":[OSD([sQuery(id+"F4.wireOp",EDGE,"E6")])],"isStart":true});
            var Q1279;
            Q1279=makeQuery(id+"F5.opExtrude","CAP_EDGE",EDGE,{"disambiguationData":[OSD([sQuery(id+"F4.wireOp",EDGE,"E6")])],"isStart":true});
            var Q1280;
            Q1280=makeQuery(id+"F5.opExtrude","CAP_EDGE",EDGE,{"disambiguationData":[OSD([sQuery(id+"F4.wireOp",EDGE,"E6")])],"isStart":true});
            var Q1281;
            Q1281=makeQuery(id+"F5.opExtrude","CAP_EDGE",EDGE,{"disambiguationData":[OSD([sQuery(id+"F4.wireOp",EDGE,"E6")])],"isStart":true});
            var Q1282;
            Q1282=makeQuery(id+"F5.opExtrude","CAP_EDGE",EDGE,{"disambiguationData":[OSD([sQuery(id+"F4.wireOp",EDGE,"E6")])],"isStart":true});
            var Q1283;
            Q1283=makeQuery(id+"F5.opExtrude","CAP_EDGE",EDGE,{"disambiguationData":[OSD([sQuery(id+"F4.wireOp",EDGE,"E6")])],"isStart":true});
            var Q1284;
            Q1284=makeQuery(id+"F5.opExtrude","CAP_EDGE",EDGE,{"disambiguationData":[OSD([sQuery(id+"F4.wireOp",EDGE,"E6")])],"isStart":true});
            var Q1285;
            Q1285=makeQuery(id+"F5.opExtrude","CAP_EDGE",EDGE,{"disambiguationData":[OSD([sQuery(id+"F4.wireOp",EDGE,"E6")])],"isStart":true});
            var Q1286;
            Q1286=makeQuery(id+"F5.opExtrude","CAP_EDGE",EDGE,{"disambiguationData":[OSD([sQuery(id+"F4.wireOp",EDGE,"E6")])],"isStart":true});
            var Q1287;
            Q1287=makeQuery(id+"F5.opExtrude","CAP_EDGE",EDGE,{"disambiguationData":[OSD([sQuery(id+"F4.wireOp",EDGE,"E6")])],"isStart":true});
            var Q1288;
            Q1288=makeQuery(id+"F5.opExtrude","CAP_EDGE",EDGE,{"disambiguationData":[OSD([sQuery(id+"F4.wireOp",EDGE,"E6")])],"isStart":true});
            var Q1289;
            Q1289=makeQuery(id+"F5.opExtrude","CAP_EDGE",EDGE,{"disambiguationData":[OSD([sQuery(id+"F4.wireOp",EDGE,"E6")])],"isStart":true});
            var Q1290;
            Q1290=makeQuery(id+"F5.opExtrude","CAP_EDGE",EDGE,{"disambiguationData":[OSD([sQuery(id+"F4.wireOp",EDGE,"E6")])],"isStart":true});
            var Q1291;
            Q1291=makeQuery(id+"F5.opExtrude","CAP_EDGE",EDGE,{"disambiguationData":[OSD([sQuery(id+"F4.wireOp",EDGE,"E6")])],"isStart":true});
            var Q1292;
            Q1292=makeQuery(id+"F5.opExtrude","CAP_EDGE",EDGE,{"disambiguationData":[OSD([sQuery(id+"F4.wireOp",EDGE,"E6")])],"isStart":true});
            var Q1293;
            Q1293=makeQuery(id+"F5.opExtrude","CAP_EDGE",EDGE,{"disambiguationData":[OSD([sQuery(id+"F4.wireOp",EDGE,"E6")])],"isStart":true});
            var Q1294;
            Q1294=makeQuery(id+"F5.opExtrude","CAP_EDGE",EDGE,{"disambiguationData":[OSD([sQuery(id+"F4.wireOp",EDGE,"E6")])],"isStart":true});
            var Q1295;
            Q1295=makeQuery(id+"F5.opExtrude","CAP_EDGE",EDGE,{"disambiguationData":[OSD([sQuery(id+"F4.wireOp",EDGE,"E6")])],"isStart":true});
            var Q1296;
            Q1296=makeQuery(id+"F5.opExtrude","CAP_EDGE",EDGE,{"disambiguationData":[OSD([sQuery(id+"F4.wireOp",EDGE,"E6")])],"isStart":true});
            var Q1297;
            Q1297=makeQuery(id+"F5.opExtrude","CAP_EDGE",EDGE,{"disambiguationData":[OSD([sQuery(id+"F4.wireOp",EDGE,"E6")])],"isStart":true});
            var Q1298;
            Q1298=makeQuery(id+"F5.opExtrude","CAP_EDGE",EDGE,{"disambiguationData":[OSD([sQuery(id+"F4.wireOp",EDGE,"E6")])],"isStart":true});
            var Q1299;
            Q1299=makeQuery(id+"F5.opExtrude","CAP_EDGE",EDGE,{"disambiguationData":[OSD([sQuery(id+"F4.wireOp",EDGE,"E6")])],"isStart":true});
            var Q1300;
            Q1300=makeQuery(id+"F5.opExtrude","CAP_EDGE",EDGE,{"disambiguationData":[OSD([sQuery(id+"F4.wireOp",EDGE,"E6")])],"isStart":true});
            var Q1301;
            Q1301=makeQuery(id+"F5.opExtrude","CAP_EDGE",EDGE,{"disambiguationData":[OSD([sQuery(id+"F4.wireOp",EDGE,"E6")])],"isStart":true});
            var Q1302;
            Q1302=makeQuery(id+"F5.opExtrude","CAP_EDGE",EDGE,{"disambiguationData":[OSD([sQuery(id+"F4.wireOp",EDGE,"E6")])],"isStart":true});
            var Q1303;
            Q1303=makeQuery(id+"F5.opExtrude","CAP_EDGE",EDGE,{"disambiguationData":[OSD([sQuery(id+"F4.wireOp",EDGE,"E6")])],"isStart":true});
            var Q1304;
            Q1304=makeQuery(id+"F5.opExtrude","CAP_EDGE",EDGE,{"disambiguationData":[OSD([sQuery(id+"F4.wireOp",EDGE,"E6")])],"isStart":true});
            var Q1305;
            Q1305=makeQuery(id+"F5.opExtrude","CAP_EDGE",EDGE,{"disambiguationData":[OSD([sQuery(id+"F4.wireOp",EDGE,"E6")])],"isStart":true});
            var Q1306;
            Q1306=makeQuery(id+"F5.opExtrude","CAP_EDGE",EDGE,{"disambiguationData":[OSD([sQuery(id+"F4.wireOp",EDGE,"E6")])],"isStart":true});
            var Q1307;
            Q1307=makeQuery(id+"F5.opExtrude","CAP_EDGE",EDGE,{"disambiguationData":[OSD([sQuery(id+"F4.wireOp",EDGE,"E6")])],"isStart":true});
            var Q1308;
            Q1308=makeQuery(id+"F5.opExtrude","CAP_EDGE",EDGE,{"disambiguationData":[OSD([sQuery(id+"F4.wireOp",EDGE,"E6")])],"isStart":true});
            var Q1309;
            Q1309=makeQuery(id+"F5.opExtrude","CAP_EDGE",EDGE,{"disambiguationData":[OSD([sQuery(id+"F4.wireOp",EDGE,"E6")])],"isStart":true});
            var Q1310;
            Q1310=makeQuery(id+"F5.opExtrude","CAP_EDGE",EDGE,{"disambiguationData":[OSD([sQuery(id+"F4.wireOp",EDGE,"E6")])],"isStart":true});
            var Q1311;
            Q1311=makeQuery(id+"F5.opExtrude","CAP_EDGE",EDGE,{"disambiguationData":[OSD([sQuery(id+"F4.wireOp",EDGE,"E6")])],"isStart":true});
            var Q1312;
            Q1312=makeQuery(id+"F5.opExtrude","CAP_EDGE",EDGE,{"disambiguationData":[OSD([sQuery(id+"F4.wireOp",EDGE,"E6")])],"isStart":true});
            var Q1313;
            Q1313=makeQuery(id+"F5.opExtrude","CAP_EDGE",EDGE,{"disambiguationData":[OSD([sQuery(id+"F4.wireOp",EDGE,"E6")])],"isStart":true});
            var Q1314;
            Q1314=makeQuery(id+"F5.opExtrude","CAP_EDGE",EDGE,{"disambiguationData":[OSD([sQuery(id+"F4.wireOp",EDGE,"E6")])],"isStart":true});
            var Q1315;
            Q1315=makeQuery(id+"F5.opExtrude","CAP_EDGE",EDGE,{"disambiguationData":[OSD([sQuery(id+"F4.wireOp",EDGE,"E6")])],"isStart":true});
            var Q1316;
            Q1316=makeQuery(id+"F5.opExtrude","CAP_EDGE",EDGE,{"disambiguationData":[OSD([sQuery(id+"F4.wireOp",EDGE,"E6")])],"isStart":true});
            var Q1317;
            Q1317=makeQuery(id+"F5.opExtrude","CAP_EDGE",EDGE,{"disambiguationData":[OSD([sQuery(id+"F4.wireOp",EDGE,"E6")])],"isStart":true});
            var Q1318;
            Q1318=makeQuery(id+"F5.opExtrude","CAP_EDGE",EDGE,{"disambiguationData":[OSD([sQuery(id+"F4.wireOp",EDGE,"E6")])],"isStart":true});
            var Q1319;
            Q1319=makeQuery(id+"F5.opExtrude","CAP_EDGE",EDGE,{"disambiguationData":[OSD([sQuery(id+"F4.wireOp",EDGE,"E6")])],"isStart":true});
            var Q1320;
            Q1320=makeQuery(id+"F5.opExtrude","CAP_EDGE",EDGE,{"disambiguationData":[OSD([sQuery(id+"F4.wireOp",EDGE,"E6")])],"isStart":true});
            var Q1321;
            Q1321=makeQuery(id+"F5.opExtrude","CAP_EDGE",EDGE,{"disambiguationData":[OSD([sQuery(id+"F4.wireOp",EDGE,"E6")])],"isStart":true});
            var Q1322;
            Q1322=makeQuery(id+"F5.opExtrude","CAP_EDGE",EDGE,{"disambiguationData":[OSD([sQuery(id+"F4.wireOp",EDGE,"E6")])],"isStart":true});
            var Q1323;
            Q1323=makeQuery(id+"F5.opExtrude","CAP_EDGE",EDGE,{"disambiguationData":[OSD([sQuery(id+"F4.wireOp",EDGE,"E6")])],"isStart":true});
            var Q1324;
            Q1324=makeQuery(id+"F5.opExtrude","CAP_EDGE",EDGE,{"disambiguationData":[OSD([sQuery(id+"F4.wireOp",EDGE,"E6")])],"isStart":true});
            var Q1325;
            Q1325=makeQuery(id+"F5.opExtrude","CAP_EDGE",EDGE,{"disambiguationData":[OSD([sQuery(id+"F4.wireOp",EDGE,"E6")])],"isStart":true});
            var Q1326;
            Q1326=makeQuery(id+"F5.opExtrude","CAP_EDGE",EDGE,{"disambiguationData":[OSD([sQuery(id+"F4.wireOp",EDGE,"E6")])],"isStart":true});
            var Q1327;
            Q1327=makeQuery(id+"F5.opExtrude","CAP_EDGE",EDGE,{"disambiguationData":[OSD([sQuery(id+"F4.wireOp",EDGE,"E6")])],"isStart":true});
            var Q1328;
            Q1328=makeQuery(id+"F5.opExtrude","CAP_EDGE",EDGE,{"disambiguationData":[OSD([sQuery(id+"F4.wireOp",EDGE,"E6")])],"isStart":true});
            var Q1329;
            Q1329=makeQuery(id+"F5.opExtrude","CAP_EDGE",EDGE,{"disambiguationData":[OSD([sQuery(id+"F4.wireOp",EDGE,"E6")])],"isStart":true});
            var Q1330;
            Q1330=makeQuery(id+"F5.opExtrude","CAP_EDGE",EDGE,{"disambiguationData":[OSD([sQuery(id+"F4.wireOp",EDGE,"E6")])],"isStart":true});
            var Q1331;
            Q1331=makeQuery(id+"F5.opExtrude","CAP_EDGE",EDGE,{"disambiguationData":[OSD([sQuery(id+"F4.wireOp",EDGE,"E6")])],"isStart":true});
            var Q1332;
            Q1332=makeQuery(id+"F5.opExtrude","CAP_EDGE",EDGE,{"disambiguationData":[OSD([sQuery(id+"F4.wireOp",EDGE,"E6")])],"isStart":true});
            var Q1333;
            Q1333=makeQuery(id+"F5.opExtrude","CAP_EDGE",EDGE,{"disambiguationData":[OSD([sQuery(id+"F4.wireOp",EDGE,"E6")])],"isStart":true});
            var Q1334;
            Q1334=makeQuery(id+"F5.opExtrude","CAP_EDGE",EDGE,{"disambiguationData":[OSD([sQuery(id+"F4.wireOp",EDGE,"E6")])],"isStart":true});
            var Q1335;
            Q1335=makeQuery(id+"F5.opExtrude","CAP_EDGE",EDGE,{"disambiguationData":[OSD([sQuery(id+"F4.wireOp",EDGE,"E6")])],"isStart":true});
            var Q1336;
            Q1336=makeQuery(id+"F5.opExtrude","CAP_EDGE",EDGE,{"disambiguationData":[OSD([sQuery(id+"F4.wireOp",EDGE,"E6")])],"isStart":true});
            var Q1337;
            Q1337=makeQuery(id+"F5.opExtrude","CAP_EDGE",EDGE,{"disambiguationData":[OSD([sQuery(id+"F4.wireOp",EDGE,"E6")])],"isStart":true});
            var Q1338;
            Q1338=makeQuery(id+"F5.opExtrude","CAP_EDGE",EDGE,{"disambiguationData":[OSD([sQuery(id+"F4.wireOp",EDGE,"E6")])],"isStart":true});
            var Q1339;
            Q1339=makeQuery(id+"F5.opExtrude","CAP_EDGE",EDGE,{"disambiguationData":[OSD([sQuery(id+"F4.wireOp",EDGE,"E6")])],"isStart":true});
            var Q1340;
            Q1340=makeQuery(id+"F5.opExtrude","CAP_EDGE",EDGE,{"disambiguationData":[OSD([sQuery(id+"F4.wireOp",EDGE,"E6")])],"isStart":true});
            var Q1341;
            Q1341=makeQuery(id+"F5.opExtrude","CAP_EDGE",EDGE,{"disambiguationData":[OSD([sQuery(id+"F4.wireOp",EDGE,"E6")])],"isStart":true});
            var Q1342;
            Q1342=makeQuery(id+"F5.opExtrude","CAP_EDGE",EDGE,{"disambiguationData":[OSD([sQuery(id+"F4.wireOp",EDGE,"E6")])],"isStart":true});
            var Q1343;
            Q1343=makeQuery(id+"F5.opExtrude","CAP_EDGE",EDGE,{"disambiguationData":[OSD([sQuery(id+"F4.wireOp",EDGE,"E6")])],"isStart":true});
            var Q1344;
            Q1344=makeQuery(id+"F5.opExtrude","CAP_EDGE",EDGE,{"disambiguationData":[OSD([sQuery(id+"F4.wireOp",EDGE,"E6")])],"isStart":true});
            var Q1345;
            Q1345=makeQuery(id+"F5.opExtrude","CAP_EDGE",EDGE,{"disambiguationData":[OSD([sQuery(id+"F4.wireOp",EDGE,"E6")])],"isStart":true});
            var Q1346;
            Q1346=makeQuery(id+"F5.opExtrude","CAP_EDGE",EDGE,{"disambiguationData":[OSD([sQuery(id+"F4.wireOp",EDGE,"E6")])],"isStart":true});
            var Q1347;
            Q1347=makeQuery(id+"F5.opExtrude","CAP_EDGE",EDGE,{"disambiguationData":[OSD([sQuery(id+"F4.wireOp",EDGE,"E6")])],"isStart":true});
            var Q1348;
            Q1348=makeQuery(id+"F5.opExtrude","CAP_EDGE",EDGE,{"disambiguationData":[OSD([sQuery(id+"F4.wireOp",EDGE,"E6")])],"isStart":true});
            var Q1349;
            Q1349=makeQuery(id+"F5.opExtrude","CAP_EDGE",EDGE,{"disambiguationData":[OSD([sQuery(id+"F4.wireOp",EDGE,"E6")])],"isStart":true});
            var Q1350;
            Q1350=makeQuery(id+"F5.opExtrude","CAP_EDGE",EDGE,{"disambiguationData":[OSD([sQuery(id+"F4.wireOp",EDGE,"E6")])],"isStart":true});
            var Q1351;
            Q1351=makeQuery(id+"F5.opExtrude","CAP_EDGE",EDGE,{"disambiguationData":[OSD([sQuery(id+"F4.wireOp",EDGE,"E6")])],"isStart":true});
            var Q1352;
            Q1352=makeQuery(id+"F5.opExtrude","CAP_EDGE",EDGE,{"disambiguationData":[OSD([sQuery(id+"F4.wireOp",EDGE,"E6")])],"isStart":true});
            var Q1353;
            Q1353=makeQuery(id+"F5.opExtrude","CAP_EDGE",EDGE,{"disambiguationData":[OSD([sQuery(id+"F4.wireOp",EDGE,"E6")])],"isStart":true});
            var Q1354;
            Q1354=makeQuery(id+"F5.opExtrude","CAP_EDGE",EDGE,{"disambiguationData":[OSD([sQuery(id+"F4.wireOp",EDGE,"E6")])],"isStart":true});
            var Q1355;
            Q1355=makeQuery(id+"F5.opExtrude","CAP_EDGE",EDGE,{"disambiguationData":[OSD([sQuery(id+"F4.wireOp",EDGE,"E6")])],"isStart":true});
            var Q1356;
            Q1356=makeQuery(id+"F5.opExtrude","CAP_EDGE",EDGE,{"disambiguationData":[OSD([sQuery(id+"F4.wireOp",EDGE,"E6")])],"isStart":true});
            var Q1357;
            Q1357=makeQuery(id+"F5.opExtrude","CAP_EDGE",EDGE,{"disambiguationData":[OSD([sQuery(id+"F4.wireOp",EDGE,"E6")])],"isStart":true});
            var Q1358;
            Q1358=makeQuery(id+"F5.opExtrude","CAP_EDGE",EDGE,{"disambiguationData":[OSD([sQuery(id+"F4.wireOp",EDGE,"E6")])],"isStart":true});
            var Q1359;
            Q1359=makeQuery(id+"F5.opExtrude","CAP_EDGE",EDGE,{"disambiguationData":[OSD([sQuery(id+"F4.wireOp",EDGE,"E6")])],"isStart":true});
            var Q1360;
            Q1360=makeQuery(id+"F5.opExtrude","CAP_EDGE",EDGE,{"disambiguationData":[OSD([sQuery(id+"F4.wireOp",EDGE,"E6")])],"isStart":true});
            var Q1361;
            Q1361=makeQuery(id+"F5.opExtrude","CAP_EDGE",EDGE,{"disambiguationData":[OSD([sQuery(id+"F4.wireOp",EDGE,"E6")])],"isStart":true});
            var Q1362;
            Q1362=makeQuery(id+"F5.opExtrude","CAP_EDGE",EDGE,{"disambiguationData":[OSD([sQuery(id+"F4.wireOp",EDGE,"E6")])],"isStart":true});
            var Q1363;
            Q1363=makeQuery(id+"F5.opExtrude","CAP_EDGE",EDGE,{"disambiguationData":[OSD([sQuery(id+"F4.wireOp",EDGE,"E6")])],"isStart":true});
            var Q1364;
            Q1364=makeQuery(id+"F5.opExtrude","CAP_EDGE",EDGE,{"disambiguationData":[OSD([sQuery(id+"F4.wireOp",EDGE,"E6")])],"isStart":true});
            var Q1365;
            Q1365=makeQuery(id+"F5.opExtrude","CAP_EDGE",EDGE,{"disambiguationData":[OSD([sQuery(id+"F4.wireOp",EDGE,"E6")])],"isStart":true});
            var Q1366;
            Q1366=makeQuery(id+"F5.opExtrude","CAP_EDGE",EDGE,{"disambiguationData":[OSD([sQuery(id+"F4.wireOp",EDGE,"E6")])],"isStart":true});
            var Q1367;
            Q1367=makeQuery(id+"F5.opExtrude","CAP_EDGE",EDGE,{"disambiguationData":[OSD([sQuery(id+"F4.wireOp",EDGE,"E6")])],"isStart":true});
            var Q1368;
            Q1368=makeQuery(id+"F5.opExtrude","CAP_EDGE",EDGE,{"disambiguationData":[OSD([sQuery(id+"F4.wireOp",EDGE,"E6")])],"isStart":true});
            var Q1369;
            Q1369=makeQuery(id+"F5.opExtrude","CAP_EDGE",EDGE,{"disambiguationData":[OSD([sQuery(id+"F4.wireOp",EDGE,"E6")])],"isStart":true});
            var Q1370;
            Q1370=makeQuery(id+"F5.opExtrude","CAP_EDGE",EDGE,{"disambiguationData":[OSD([sQuery(id+"F4.wireOp",EDGE,"E6")])],"isStart":true});
            var Q1371;
            Q1371=makeQuery(id+"F5.opExtrude","CAP_EDGE",EDGE,{"disambiguationData":[OSD([sQuery(id+"F4.wireOp",EDGE,"E6")])],"isStart":true});
            var Q1372;
            Q1372=makeQuery(id+"F5.opExtrude","CAP_EDGE",EDGE,{"disambiguationData":[OSD([sQuery(id+"F4.wireOp",EDGE,"E6")])],"isStart":true});
            var Q1373;
            Q1373=makeQuery(id+"F5.opExtrude","CAP_EDGE",EDGE,{"disambiguationData":[OSD([sQuery(id+"F4.wireOp",EDGE,"E6")])],"isStart":true});
            var Q1374;
            Q1374=makeQuery(id+"F5.opExtrude","CAP_EDGE",EDGE,{"disambiguationData":[OSD([sQuery(id+"F4.wireOp",EDGE,"E6")])],"isStart":true});
            var Q1375;
            Q1375=makeQuery(id+"F5.opExtrude","CAP_EDGE",EDGE,{"disambiguationData":[OSD([sQuery(id+"F4.wireOp",EDGE,"E6")])],"isStart":true});
            var Q1376;
            Q1376=makeQuery(id+"F5.opExtrude","CAP_EDGE",EDGE,{"disambiguationData":[OSD([sQuery(id+"F4.wireOp",EDGE,"E6")])],"isStart":true});
            var Q1377;
            Q1377=makeQuery(id+"F5.opExtrude","CAP_EDGE",EDGE,{"disambiguationData":[OSD([sQuery(id+"F4.wireOp",EDGE,"E6")])],"isStart":true});
            var Q1378;
            Q1378=makeQuery(id+"F5.opExtrude","CAP_EDGE",EDGE,{"disambiguationData":[OSD([sQuery(id+"F4.wireOp",EDGE,"E6")])],"isStart":true});
            var Q1379;
            Q1379=makeQuery(id+"F5.opExtrude","CAP_EDGE",EDGE,{"disambiguationData":[OSD([sQuery(id+"F4.wireOp",EDGE,"E6")])],"isStart":true});
            fillet(context, id + "F17", {"entities" : qUnion([Q0, Q1, Q2, Q3, Q4, Q5, Q6, Q7, Q8, Q9, Q10, Q11, Q12, Q13, Q14, Q15, Q16, Q17, Q18, Q19, Q20, Q21, Q22, Q23, Q24, Q25, Q26, Q27, Q28, Q29, Q30, Q31, Q32, Q33, Q34, Q35, Q36, Q37, Q38, Q39, Q40, Q41, Q42, Q43, Q44, Q45, Q46, Q47, Q48, Q49, Q50, Q51, Q52, Q53, Q54, Q55, Q56, Q57, Q58, Q59, Q60, Q61, Q62, Q63, Q64, Q65, Q66, Q67, Q68, Q69, Q70, Q71, Q72, Q73, Q74, Q75, Q76, Q77, Q78, Q79, Q80, Q81, Q82, Q83, Q84, Q85, Q86, Q87, Q88, Q89, Q90, Q91, Q92, Q93, Q94, Q95, Q96, Q97, Q98, Q99, Q100, Q101, Q102, Q103, Q104, Q105, Q106, Q107, Q108, Q109, Q110, Q111, Q112, Q113, Q114, Q115, Q116, Q117, Q118, Q119, Q120, Q121, Q122, Q123, Q124, Q125, Q126, Q127, Q128, Q129, Q130, Q131, Q132, Q133, Q134, Q135, Q136, Q137, Q138, Q139, Q140, Q141, Q142, Q143, Q144, Q145, Q146, Q147, Q148, Q149, Q150, Q151, Q152, Q153, Q154, Q155, Q156, Q157, Q158, Q159, Q160, Q161, Q162, Q163, Q164, Q165, Q166, Q167, Q168, Q169, Q170, Q171, Q172, Q173, Q174, Q175, Q176, Q177, Q178, Q179, Q180, Q181, Q182, Q183, Q184, Q185, Q186, Q187, Q188, Q189, Q190, Q191, Q192, Q193, Q194, Q195, Q196, Q197, Q198, Q199, Q200, Q201, Q202, Q203, Q204, Q205, Q206, Q207, Q208, Q209, Q210, Q211, Q212, Q213, Q214, Q215, Q216, Q217, Q218, Q219, Q220, Q221, Q222, Q223, Q224, Q225, Q226, Q227, Q228, Q229, Q230, Q231, Q232, Q233, Q234, Q235, Q236, Q237, Q238, Q239, Q240, Q241, Q242, Q243, Q244, Q245, Q246, Q247, Q248, Q249, Q250, Q251, Q252, Q253, Q254, Q255, Q256, Q257, Q258, Q259, Q260, Q261, Q262, Q263, Q264, Q265, Q266, Q267, Q268, Q269, Q270, Q271, Q272, Q273, Q274, Q275, Q276, Q277, Q278, Q279, Q280, Q281, Q282, Q283, Q284, Q285, Q286, Q287, Q288, Q289, Q290, Q291, Q292, Q293, Q294, Q295, Q296, Q297, Q298, Q299, Q300, Q301, Q302, Q303, Q304, Q305, Q306, Q307, Q308, Q309, Q310, Q311, Q312, Q313, Q314, Q315, Q316, Q317, Q318, Q319, Q320, Q321, Q322, Q323, Q324, Q325, Q326, Q327, Q328, Q329, Q330, Q331, Q332, Q333, Q334, Q335, Q336, Q337, Q338, Q339, Q340, Q341, Q342, Q343, Q344, Q345, Q346, Q347, Q348, Q349, Q350, Q351, Q352, Q353, Q354, Q355, Q356, Q357, Q358, Q359, Q360, Q361, Q362, Q363, Q364, Q365, Q366, Q367, Q368, Q369, Q370, Q371, Q372, Q373, Q374, Q375, Q376, Q377, Q378, Q379, Q380, Q381, Q382, Q383, Q384, Q385, Q386, Q387, Q388, Q389, Q390, Q391, Q392, Q393, Q394, Q395, Q396, Q397, Q398, Q399, Q400, Q401, Q402, Q403, Q404, Q405, Q406, Q407, Q408, Q409, Q410, Q411, Q412, Q413, Q414, Q415, Q416, Q417, Q418, Q419, Q420, Q421, Q422, Q423, Q424, Q425, Q426, Q427, Q428, Q429, Q430, Q431, Q432, Q433, Q434, Q435, Q436, Q437, Q438, Q439, Q440, Q441, Q442, Q443, Q444, Q445, Q446, Q447, Q448, Q449, Q450, Q451, Q452, Q453, Q454, Q455, Q456, Q457, Q458, Q459, Q460, Q461, Q462, Q463, Q464, Q465, Q466, Q467, Q468, Q469, Q470, Q471, Q472, Q473, Q474, Q475, Q476, Q477, Q478, Q479, Q480, Q481, Q482, Q483, Q484, Q485, Q486, Q487, Q488, Q489, Q490, Q491, Q492, Q493, Q494, Q495, Q496, Q497, Q498, Q499, Q500, Q501, Q502, Q503, Q504, Q505, Q506, Q507, Q508, Q509, Q510, Q511, Q512, Q513, Q514, Q515, Q516, Q517, Q518, Q519, Q520, Q521, Q522, Q523, Q524, Q525, Q526, Q527, Q528, Q529, Q530, Q531, Q532, Q533, Q534, Q535, Q536, Q537, Q538, Q539, Q540, Q541, Q542, Q543, Q544, Q545, Q546, Q547, Q548, Q549, Q550, Q551, Q552, Q553, Q554, Q555, Q556, Q557, Q558, Q559, Q560, Q561, Q562, Q563, Q564, Q565, Q566, Q567, Q568, Q569, Q570, Q571, Q572, Q573, Q574, Q575, Q576, Q577, Q578, Q579, Q580, Q581, Q582, Q583, Q584, Q585, Q586, Q587, Q588, Q589, Q590, Q591, Q592, Q593, Q594, Q595, Q596, Q597, Q598, Q599, Q600, Q601, Q602, Q603, Q604, Q605, Q606, Q607, Q608, Q609, Q610, Q611, Q612, Q613, Q614, Q615, Q616, Q617, Q618, Q619, Q620, Q621, Q622, Q623, Q624, Q625, Q626, Q627, Q628, Q629, Q630, Q631, Q632, Q633, Q634, Q635, Q636, Q637, Q638, Q639, Q640, Q641, Q642, Q643, Q644, Q645, Q646, Q647, Q648, Q649, Q650, Q651, Q652, Q653, Q654, Q655, Q656, Q657, Q658, Q659, Q660, Q661, Q662, Q663, Q664, Q665, Q666, Q667, Q668, Q669, Q670, Q671, Q672, Q673, Q674, Q675, Q676, Q677, Q678, Q679, Q680, Q681, Q682, Q683, Q684, Q685, Q686, Q687, Q688, Q689, Q690, Q691, Q692, Q693, Q694, Q695, Q696, Q697, Q698, Q699, Q700, Q701, Q702, Q703, Q704, Q705, Q706, Q707, Q708, Q709, Q710, Q711, Q712, Q713, Q714, Q715, Q716, Q717, Q718, Q719, Q720, Q721, Q722, Q723, Q724, Q725, Q726, Q727, Q728, Q729, Q730, Q731, Q732, Q733, Q734, Q735, Q736, Q737, Q738, Q739, Q740, Q741, Q742, Q743, Q744, Q745, Q746, Q747, Q748, Q749, Q750, Q751, Q752, Q753, Q754, Q755, Q756, Q757, Q758, Q759, Q760, Q761, Q762, Q763, Q764, Q765, Q766, Q767, Q768, Q769, Q770, Q771, Q772, Q773, Q774, Q775, Q776, Q777, Q778, Q779, Q780, Q781, Q782, Q783, Q784, Q785, Q786, Q787, Q788, Q789, Q790, Q791, Q792, Q793, Q794, Q795, Q796, Q797, Q798, Q799, Q800, Q801, Q802, Q803, Q804, Q805, Q806, Q807, Q808, Q809, Q810, Q811, Q812, Q813, Q814, Q815, Q816, Q817, Q818, Q819, Q820, Q821, Q822, Q823, Q824, Q825, Q826, Q827, Q828, Q829, Q830, Q831, Q832, Q833, Q834, Q835, Q836, Q837, Q838, Q839, Q840, Q841, Q842, Q843, Q844, Q845, Q846, Q847, Q848, Q849, Q850, Q851, Q852, Q853, Q854, Q855, Q856, Q857, Q858, Q859, Q860, Q861, Q862, Q863, Q864, Q865, Q866, Q867, Q868, Q869, Q870, Q871, Q872, Q873, Q874, Q875, Q876, Q877, Q878, Q879, Q880, Q881, Q882, Q883, Q884, Q885, Q886, Q887, Q888, Q889, Q890, Q891, Q892, Q893, Q894, Q895, Q896, Q897, Q898, Q899, Q900, Q901, Q902, Q903, Q904, Q905, Q906, Q907, Q908, Q909, Q910, Q911, Q912, Q913, Q914, Q915, Q916, Q917, Q918, Q919, Q920, Q921, Q922, Q923, Q924, Q925, Q926, Q927, Q928, Q929, Q930, Q931, Q932, Q933, Q934, Q935, Q936, Q937, Q938, Q939, Q940, Q941, Q942, Q943, Q944, Q945, Q946, Q947, Q948, Q949, Q950, Q951, Q952, Q953, Q954, Q955, Q956, Q957, Q958, Q959, Q960, Q961, Q962, Q963, Q964, Q965, Q966, Q967, Q968, Q969, Q970, Q971, Q972, Q973, Q974, Q975, Q976, Q977, Q978, Q979, Q980, Q981, Q982, Q983, Q984, Q985, Q986, Q987, Q988, Q989, Q990, Q991, Q992, Q993, Q994, Q995, Q996, Q997, Q998, Q999, Q1000, Q1001, Q1002, Q1003, Q1004, Q1005, Q1006, Q1007, Q1008, Q1009, Q1010, Q1011, Q1012, Q1013, Q1014, Q1015, Q1016, Q1017, Q1018, Q1019, Q1020, Q1021, Q1022, Q1023, Q1024, Q1025, Q1026, Q1027, Q1028, Q1029, Q1030, Q1031, Q1032, Q1033, Q1034, Q1035, Q1036, Q1037, Q1038, Q1039, Q1040, Q1041, Q1042, Q1043, Q1044, Q1045, Q1046, Q1047, Q1048, Q1049, Q1050, Q1051, Q1052, Q1053, Q1054, Q1055, Q1056, Q1057, Q1058, Q1059, Q1060, Q1061, Q1062, Q1063, Q1064, Q1065, Q1066, Q1067, Q1068, Q1069, Q1070, Q1071, Q1072, Q1073, Q1074, Q1075, Q1076, Q1077, Q1078, Q1079, Q1080, Q1081, Q1082, Q1083, Q1084, Q1085, Q1086, Q1087, Q1088, Q1089, Q1090, Q1091, Q1092, Q1093, Q1094, Q1095, Q1096, Q1097, Q1098, Q1099, Q1100, Q1101, Q1102, Q1103, Q1104, Q1105, Q1106, Q1107, Q1108, Q1109, Q1110, Q1111, Q1112, Q1113, Q1114, Q1115, Q1116, Q1117, Q1118, Q1119, Q1120, Q1121, Q1122, Q1123, Q1124, Q1125, Q1126, Q1127, Q1128, Q1129, Q1130, Q1131, Q1132, Q1133, Q1134, Q1135, Q1136, Q1137, Q1138, Q1139, Q1140, Q1141, Q1142, Q1143, Q1144, Q1145, Q1146, Q1147, Q1148, Q1149, Q1150, Q1151, Q1152, Q1153, Q1154, Q1155, Q1156, Q1157, Q1158, Q1159, Q1160, Q1161, Q1162, Q1163, Q1164, Q1165, Q1166, Q1167, Q1168, Q1169, Q1170, Q1171, Q1172, Q1173, Q1174, Q1175, Q1176, Q1177, Q1178, Q1179, Q1180, Q1181, Q1182, Q1183, Q1184, Q1185, Q1186, Q1187, Q1188, Q1189, Q1190, Q1191, Q1192, Q1193, Q1194, Q1195, Q1196, Q1197, Q1198, Q1199, Q1200, Q1201, Q1202, Q1203, Q1204, Q1205, Q1206, Q1207, Q1208, Q1209, Q1210, Q1211, Q1212, Q1213, Q1214, Q1215, Q1216, Q1217, Q1218, Q1219, Q1220, Q1221, Q1222, Q1223, Q1224, Q1225, Q1226, Q1227, Q1228, Q1229, Q1230, Q1231, Q1232, Q1233, Q1234, Q1235, Q1236, Q1237, Q1238, Q1239, Q1240, Q1241, Q1242, Q1243, Q1244, Q1245, Q1246, Q1247, Q1248, Q1249, Q1250, Q1251, Q1252, Q1253, Q1254, Q1255, Q1256, Q1257, Q1258, Q1259, Q1260, Q1261, Q1262, Q1263, Q1264, Q1265, Q1266, Q1267, Q1268, Q1269, Q1270, Q1271, Q1272, Q1273, Q1274, Q1275, Q1276, Q1277, Q1278, Q1279, Q1280, Q1281, Q1282, Q1283, Q1284, Q1285, Q1286, Q1287, Q1288, Q1289, Q1290, Q1291, Q1292, Q1293, Q1294, Q1295, Q1296, Q1297, Q1298, Q1299, Q1300, Q1301, Q1302, Q1303, Q1304, Q1305, Q1306, Q1307, Q1308, Q1309, Q1310, Q1311, Q1312, Q1313, Q1314, Q1315, Q1316, Q1317, Q1318, Q1319, Q1320, Q1321, Q1322, Q1323, Q1324, Q1325, Q1326, Q1327, Q1328, Q1329, Q1330, Q1331, Q1332, Q1333, Q1334, Q1335, Q1336, Q1337, Q1338, Q1339, Q1340, Q1341, Q1342, Q1343, Q1344, Q1345, Q1346, Q1347, Q1348, Q1349, Q1350, Q1351, Q1352, Q1353, Q1354, Q1355, Q1356, Q1357, Q1358, Q1359, Q1360, Q1361, Q1362, Q1363, Q1364, Q1365, Q1366, Q1367, Q1368, Q1369, Q1370, Q1371, Q1372, Q1373, Q1374, Q1375, Q1376, Q1377, Q1378, Q1379]), "radius" : 2 * mm, "tangentPropagation" : true, "allowEdgeOverflow" : false});
        }
    });
